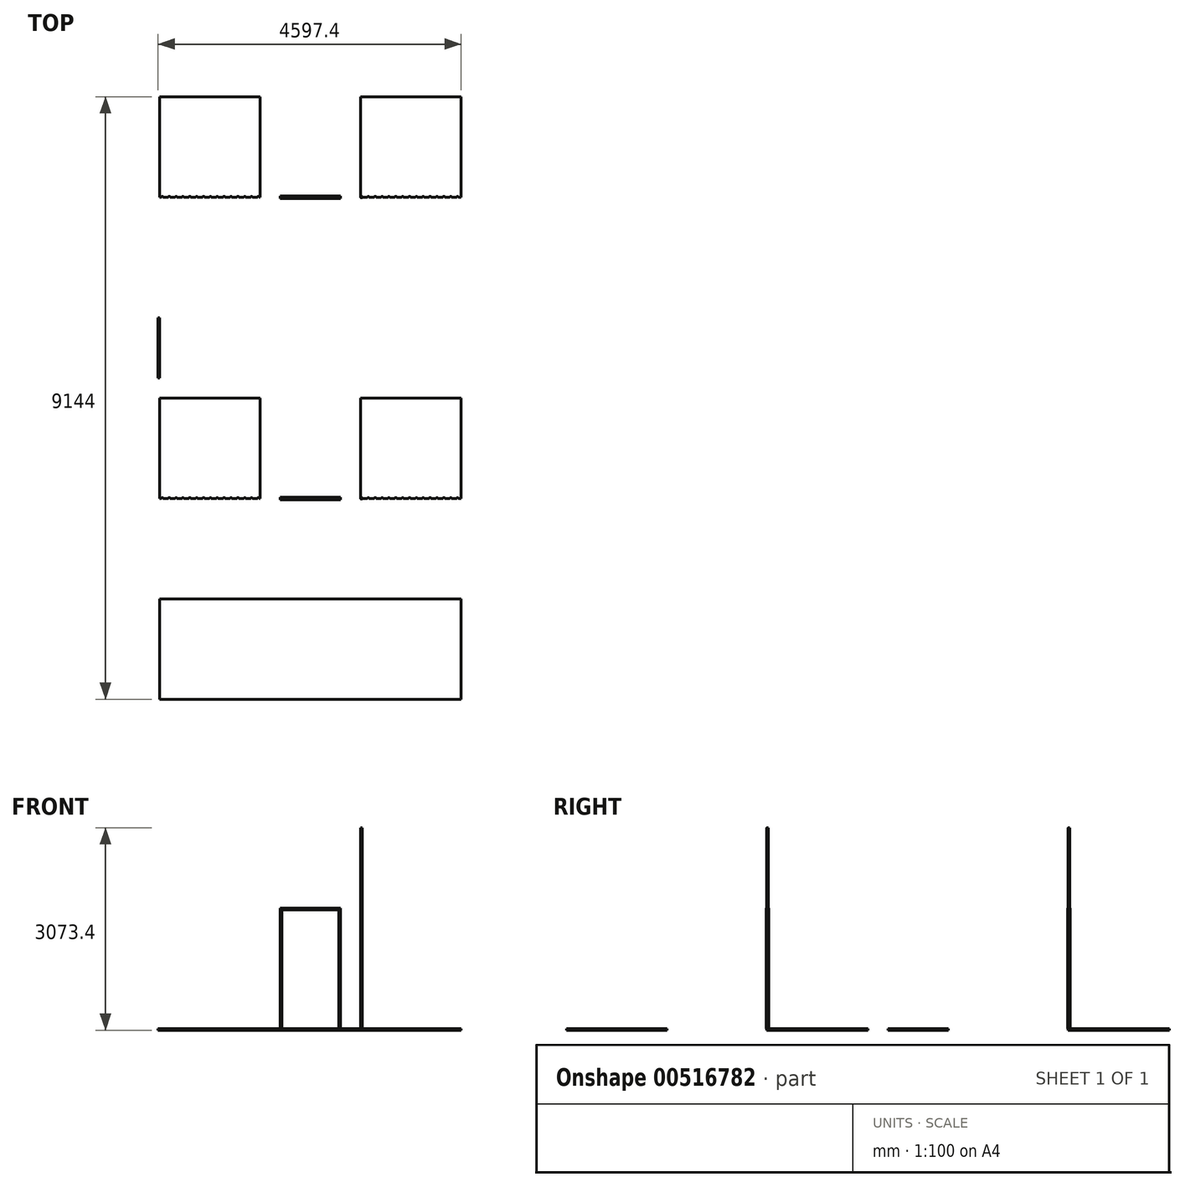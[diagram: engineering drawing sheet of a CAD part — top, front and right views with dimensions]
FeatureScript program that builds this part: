
annotation { "Feature Type Name" : "Feature", "Feature Type Description" : "" }
export const myFeature = defineFeature(function(context is Context, id is Id, definition is map)
    precondition{}
    {
        {
            var Q0;
            Q0=qCreatedBy(makeId("Top.planeOp"),FACE);
            var sketch = newSketch(context, id + "F0", { "sketchPlane" : qUnion([Q0])});
            skLineSegment(sketch, "E0.bottom", {"start": v(-766.53, 731.63) * mm, "end": v(757.47, 731.63) * mm});
            skLineSegment(sketch, "E0.top", {"start": v(-766.53, -792.37) * mm, "end": v(757.47, -792.37) * mm});
            skLineSegment(sketch, "E0.left", {"start": v(-766.53, 731.63) * mm, "end": v(-766.53, -792.37) * mm});
            skLineSegment(sketch, "E0.right", {"start": v(757.47, 731.63) * mm, "end": v(757.47, -792.37) * mm});
            skLineSegment(sketch, "E1.0.1.1", {"start": v(-766.53, 2255.63) * mm, "end": v(-766.53, 731.63) * mm});
            skLineSegment(sketch, "E1.0.1.2", {"start": v(757.47, 2255.63) * mm, "end": v(757.47, 731.63) * mm});
            skLineSegment(sketch, "E1.0.1.3", {"start": v(-766.53, 2255.63) * mm, "end": v(757.47, 2255.63) * mm});
            skLineSegment(sketch, "E1.0.2.0", {"start": v(-766.53, 2255.63) * mm, "end": v(757.47, 2255.63) * mm});
            skLineSegment(sketch, "E1.0.2.1", {"start": v(-766.53, 3779.63) * mm, "end": v(-766.53, 2255.63) * mm});
            skLineSegment(sketch, "E1.0.2.2", {"start": v(757.47, 3779.63) * mm, "end": v(757.47, 2255.63) * mm});
            skLineSegment(sketch, "E1.0.2.3", {"start": v(-766.53, 3779.63) * mm, "end": v(757.47, 3779.63) * mm});
            skLineSegment(sketch, "E1.0.3.0", {"start": v(-766.53, 3779.63) * mm, "end": v(757.47, 3779.63) * mm});
            skLineSegment(sketch, "E1.0.3.1", {"start": v(-766.53, 5303.63) * mm, "end": v(-766.53, 3779.63) * mm});
            skLineSegment(sketch, "E1.0.3.2", {"start": v(757.47, 5303.63) * mm, "end": v(757.47, 3779.63) * mm});
            skLineSegment(sketch, "E1.0.3.3", {"start": v(-766.53, 5303.63) * mm, "end": v(757.47, 5303.63) * mm});
            skLineSegment(sketch, "E1.0.4.0", {"start": v(-766.53, 5303.63) * mm, "end": v(757.47, 5303.63) * mm});
            skLineSegment(sketch, "E1.0.4.1", {"start": v(-766.53, 6827.63) * mm, "end": v(-766.53, 5303.63) * mm});
            skLineSegment(sketch, "E1.0.4.2", {"start": v(757.47, 6827.63) * mm, "end": v(757.47, 5303.63) * mm});
            skLineSegment(sketch, "E1.0.4.3", {"start": v(-766.53, 6827.63) * mm, "end": v(757.47, 6827.63) * mm});
            skLineSegment(sketch, "E1.0.5.0", {"start": v(-766.53, 6827.63) * mm, "end": v(757.47, 6827.63) * mm});
            skLineSegment(sketch, "E1.0.5.1", {"start": v(-766.53, 8351.63) * mm, "end": v(-766.53, 6827.63) * mm});
            skLineSegment(sketch, "E1.0.5.2", {"start": v(757.47, 8351.63) * mm, "end": v(757.47, 6827.63) * mm});
            skLineSegment(sketch, "E1.0.5.3", {"start": v(-766.53, 8351.63) * mm, "end": v(757.47, 8351.63) * mm});
            skLineSegment(sketch, "E1.0.6.0", {"start": v(-766.53, 8351.63) * mm, "end": v(757.47, 8351.63) * mm});
            skLineSegment(sketch, "E1.0.6.1", {"start": v(-766.53, 9875.63) * mm, "end": v(-766.53, 8351.63) * mm});
            skLineSegment(sketch, "E1.0.6.2", {"start": v(757.47, 9875.63) * mm, "end": v(757.47, 8351.63) * mm});
            skLineSegment(sketch, "E1.0.6.3", {"start": v(-766.53, 9875.63) * mm, "end": v(757.47, 9875.63) * mm});
            skLineSegment(sketch, "E1.1.0.0", {"start": v(757.47, -792.37) * mm, "end": v(2281.47, -792.37) * mm});
            skLineSegment(sketch, "E1.1.0.2", {"start": v(2281.47, 731.63) * mm, "end": v(2281.47, -792.37) * mm});
            skLineSegment(sketch, "E1.1.0.3", {"start": v(757.47, 731.63) * mm, "end": v(2281.47, 731.63) * mm});
            skLineSegment(sketch, "E1.1.1.0", {"start": v(757.47, 731.63) * mm, "end": v(2281.47, 731.63) * mm});
            skLineSegment(sketch, "E1.1.1.1", {"start": v(757.47, 2255.63) * mm, "end": v(757.47, 731.63) * mm});
            skLineSegment(sketch, "E1.1.1.2", {"start": v(2281.47, 2255.63) * mm, "end": v(2281.47, 731.63) * mm});
            skLineSegment(sketch, "E1.1.1.3", {"start": v(757.47, 2255.63) * mm, "end": v(2281.47, 2255.63) * mm});
            skLineSegment(sketch, "E1.1.2.0", {"start": v(757.47, 2255.63) * mm, "end": v(2281.47, 2255.63) * mm});
            skLineSegment(sketch, "E1.1.2.1", {"start": v(757.47, 3779.63) * mm, "end": v(757.47, 2255.63) * mm});
            skLineSegment(sketch, "E1.1.2.2", {"start": v(2281.47, 3779.63) * mm, "end": v(2281.47, 2255.63) * mm});
            skLineSegment(sketch, "E1.1.2.3", {"start": v(757.47, 3779.63) * mm, "end": v(2281.47, 3779.63) * mm});
            skLineSegment(sketch, "E1.1.3.0", {"start": v(757.47, 3779.63) * mm, "end": v(2281.47, 3779.63) * mm});
            skLineSegment(sketch, "E1.1.3.1", {"start": v(757.47, 5303.63) * mm, "end": v(757.47, 3779.63) * mm});
            skLineSegment(sketch, "E1.1.3.2", {"start": v(2281.47, 5303.63) * mm, "end": v(2281.47, 3779.63) * mm});
            skLineSegment(sketch, "E1.1.3.3", {"start": v(757.47, 5303.63) * mm, "end": v(2281.47, 5303.63) * mm});
            skLineSegment(sketch, "E1.1.4.0", {"start": v(757.47, 5303.63) * mm, "end": v(2281.47, 5303.63) * mm});
            skLineSegment(sketch, "E1.1.4.1", {"start": v(757.47, 6827.63) * mm, "end": v(757.47, 5303.63) * mm});
            skLineSegment(sketch, "E1.1.4.2", {"start": v(2281.47, 6827.63) * mm, "end": v(2281.47, 5303.63) * mm});
            skLineSegment(sketch, "E1.1.4.3", {"start": v(757.47, 6827.63) * mm, "end": v(2281.47, 6827.63) * mm});
            skLineSegment(sketch, "E1.1.5.0", {"start": v(757.47, 6827.63) * mm, "end": v(2281.47, 6827.63) * mm});
            skLineSegment(sketch, "E1.1.5.1", {"start": v(757.47, 8351.63) * mm, "end": v(757.47, 6827.63) * mm});
            skLineSegment(sketch, "E1.1.5.2", {"start": v(2281.47, 8351.63) * mm, "end": v(2281.47, 6827.63) * mm});
            skLineSegment(sketch, "E1.1.5.3", {"start": v(757.47, 8351.63) * mm, "end": v(2281.47, 8351.63) * mm});
            skLineSegment(sketch, "E1.1.6.0", {"start": v(757.47, 8351.63) * mm, "end": v(2281.47, 8351.63) * mm});
            skLineSegment(sketch, "E1.1.6.1", {"start": v(757.47, 9875.63) * mm, "end": v(757.47, 8351.63) * mm});
            skLineSegment(sketch, "E1.1.6.2", {"start": v(2281.47, 9875.63) * mm, "end": v(2281.47, 8351.63) * mm});
            skLineSegment(sketch, "E1.1.6.3", {"start": v(757.47, 9875.63) * mm, "end": v(2281.47, 9875.63) * mm});
            skLineSegment(sketch, "E1.2.0.0", {"start": v(2281.47, -792.37) * mm, "end": v(3805.47, -792.37) * mm});
            skLineSegment(sketch, "E1.2.0.1", {"start": v(2281.47, 731.63) * mm, "end": v(2281.47, -792.37) * mm});
            skLineSegment(sketch, "E1.2.0.2", {"start": v(3805.47, 731.63) * mm, "end": v(3805.47, -792.37) * mm});
            skLineSegment(sketch, "E1.2.0.3", {"start": v(2281.47, 731.63) * mm, "end": v(3805.47, 731.63) * mm});
            skLineSegment(sketch, "E1.2.1.0", {"start": v(2281.47, 731.63) * mm, "end": v(3805.47, 731.63) * mm});
            skLineSegment(sketch, "E1.2.1.1", {"start": v(2281.47, 2255.63) * mm, "end": v(2281.47, 731.63) * mm});
            skLineSegment(sketch, "E1.2.1.2", {"start": v(3805.47, 2255.63) * mm, "end": v(3805.47, 731.63) * mm});
            skLineSegment(sketch, "E1.2.1.3", {"start": v(2281.47, 2255.63) * mm, "end": v(3805.47, 2255.63) * mm});
            skLineSegment(sketch, "E1.2.2.0", {"start": v(2281.47, 2255.63) * mm, "end": v(3805.47, 2255.63) * mm});
            skLineSegment(sketch, "E1.2.2.1", {"start": v(2281.47, 3779.63) * mm, "end": v(2281.47, 2255.63) * mm});
            skLineSegment(sketch, "E1.2.2.2", {"start": v(3805.47, 3779.63) * mm, "end": v(3805.47, 2255.63) * mm});
            skLineSegment(sketch, "E1.2.2.3", {"start": v(2281.47, 3779.63) * mm, "end": v(3805.47, 3779.63) * mm});
            skLineSegment(sketch, "E1.2.3.0", {"start": v(2281.47, 3779.63) * mm, "end": v(3805.47, 3779.63) * mm});
            skLineSegment(sketch, "E1.2.3.1", {"start": v(2281.47, 5303.63) * mm, "end": v(2281.47, 3779.63) * mm});
            skLineSegment(sketch, "E1.2.3.2", {"start": v(3805.47, 5303.63) * mm, "end": v(3805.47, 3779.63) * mm});
            skLineSegment(sketch, "E1.2.3.3", {"start": v(2281.47, 5303.63) * mm, "end": v(3805.47, 5303.63) * mm});
            skLineSegment(sketch, "E1.2.4.0", {"start": v(2281.47, 5303.63) * mm, "end": v(3805.47, 5303.63) * mm});
            skLineSegment(sketch, "E1.2.4.1", {"start": v(2281.47, 6827.63) * mm, "end": v(2281.47, 5303.63) * mm});
            skLineSegment(sketch, "E1.2.4.2", {"start": v(3805.47, 6827.63) * mm, "end": v(3805.47, 5303.63) * mm});
            skLineSegment(sketch, "E1.2.4.3", {"start": v(2281.47, 6827.63) * mm, "end": v(3805.47, 6827.63) * mm});
            skLineSegment(sketch, "E1.2.5.0", {"start": v(2281.47, 6827.63) * mm, "end": v(3805.47, 6827.63) * mm});
            skLineSegment(sketch, "E1.2.5.1", {"start": v(2281.47, 8351.63) * mm, "end": v(2281.47, 6827.63) * mm});
            skLineSegment(sketch, "E1.2.5.2", {"start": v(3805.47, 8351.63) * mm, "end": v(3805.47, 6827.63) * mm});
            skLineSegment(sketch, "E1.2.5.3", {"start": v(2281.47, 8351.63) * mm, "end": v(3805.47, 8351.63) * mm});
            skLineSegment(sketch, "E1.2.6.0", {"start": v(2281.47, 8351.63) * mm, "end": v(3805.47, 8351.63) * mm});
            skLineSegment(sketch, "E1.2.6.1", {"start": v(2281.47, 9875.63) * mm, "end": v(2281.47, 8351.63) * mm});
            skLineSegment(sketch, "E1.2.6.2", {"start": v(3805.47, 9875.63) * mm, "end": v(3805.47, 8351.63) * mm});
            skLineSegment(sketch, "E1.2.6.3", {"start": v(2281.47, 9875.63) * mm, "end": v(3805.47, 9875.63) * mm});
            skLineSegment(sketch, "E1.direction1", {"start": v(-766.53, -792.37) * mm, "end": v(757.47, -792.37) * mm, "construction": true});
            skLineSegment(sketch, "E1.direction2", {"start": v(-766.53, -792.37) * mm, "end": v(-766.53, 731.63) * mm, "construction": true});
            skCircle(sketch, "E2", {"center": v(-728.43, 2255.63) * mm, "radius": 12.7 * mm});
            skCircle(sketch, "E3.0.1.0", {"center": v(-728.43, 6827.63) * mm, "radius": 12.7 * mm});
            skCircle(sketch, "E3.1.0.0", {"center": v(-624.29, 2255.63) * mm, "radius": 12.7 * mm});
            skCircle(sketch, "E3.1.1.0", {"center": v(-624.29, 6827.63) * mm, "radius": 12.7 * mm});
            skCircle(sketch, "E3.2.0.0", {"center": v(-520.15, 2255.63) * mm, "radius": 12.7 * mm});
            skCircle(sketch, "E3.2.1.0", {"center": v(-520.15, 6827.63) * mm, "radius": 12.7 * mm});
            skCircle(sketch, "E3.3.0.0", {"center": v(-416, 2255.63) * mm, "radius": 12.7 * mm});
            skCircle(sketch, "E3.3.1.0", {"center": v(-416, 6827.63) * mm, "radius": 12.7 * mm});
            skCircle(sketch, "E3.4.0.0", {"center": v(-311.87, 2255.63) * mm, "radius": 12.7 * mm});
            skCircle(sketch, "E3.4.1.0", {"center": v(-311.87, 6827.63) * mm, "radius": 12.7 * mm});
            skCircle(sketch, "E3.5.0.0", {"center": v(-207.73, 2255.63) * mm, "radius": 12.7 * mm});
            skCircle(sketch, "E3.5.1.0", {"center": v(-207.73, 6827.63) * mm, "radius": 12.7 * mm});
            skCircle(sketch, "E3.6.0.0", {"center": v(-103.59, 2255.63) * mm, "radius": 12.7 * mm});
            skCircle(sketch, "E3.6.1.0", {"center": v(-103.59, 6827.63) * mm, "radius": 12.7 * mm});
            skCircle(sketch, "E3.7.0.0", {"center": v(0.55, 2255.63) * mm, "radius": 12.7 * mm});
            skCircle(sketch, "E3.7.1.0", {"center": v(0.55, 6827.63) * mm, "radius": 12.7 * mm});
            skCircle(sketch, "E3.8.0.0", {"center": v(104.7, 2255.63) * mm, "radius": 12.7 * mm});
            skCircle(sketch, "E3.8.1.0", {"center": v(104.7, 6827.63) * mm, "radius": 12.7 * mm});
            skCircle(sketch, "E3.9.0.0", {"center": v(208.83, 2255.63) * mm, "radius": 12.7 * mm});
            skCircle(sketch, "E3.9.1.0", {"center": v(208.83, 6827.63) * mm, "radius": 12.7 * mm});
            skCircle(sketch, "E3.10.0.0", {"center": v(312.97, 2255.63) * mm, "radius": 12.7 * mm});
            skCircle(sketch, "E3.10.1.0", {"center": v(312.97, 6827.63) * mm, "radius": 12.7 * mm});
            skCircle(sketch, "E3.11.0.0", {"center": v(417.11, 2255.63) * mm, "radius": 12.7 * mm});
            skCircle(sketch, "E3.11.1.0", {"center": v(417.11, 6827.63) * mm, "radius": 12.7 * mm});
            skCircle(sketch, "E3.12.0.0", {"center": v(521.25, 2255.63) * mm, "radius": 12.7 * mm});
            skCircle(sketch, "E3.12.1.0", {"center": v(521.25, 6827.63) * mm, "radius": 12.7 * mm});
            skCircle(sketch, "E3.13.0.0", {"center": v(625.4, 2255.63) * mm, "radius": 12.7 * mm});
            skCircle(sketch, "E3.13.1.0", {"center": v(625.4, 6827.63) * mm, "radius": 12.7 * mm});
            skCircle(sketch, "E3.14.0.0", {"center": v(729.53, 2255.63) * mm, "radius": 12.7 * mm});
            skCircle(sketch, "E3.14.1.0", {"center": v(729.53, 6827.63) * mm, "radius": 12.7 * mm});
            skCircle(sketch, "E3.15.0.0", {"center": v(833.67, 2255.63) * mm, "radius": 12.7 * mm});
            skCircle(sketch, "E3.15.1.0", {"center": v(833.67, 6827.63) * mm, "radius": 12.7 * mm});
            skCircle(sketch, "E3.16.0.0", {"center": v(937.81, 2255.63) * mm, "radius": 12.7 * mm});
            skCircle(sketch, "E3.16.1.0", {"center": v(937.81, 6827.63) * mm, "radius": 12.7 * mm});
            skCircle(sketch, "E3.17.0.0", {"center": v(1041.95, 2255.63) * mm, "radius": 12.7 * mm});
            skCircle(sketch, "E3.17.1.0", {"center": v(1041.95, 6827.63) * mm, "radius": 12.7 * mm});
            skCircle(sketch, "E3.18.0.0", {"center": v(1146.1, 2255.63) * mm, "radius": 12.7 * mm});
            skCircle(sketch, "E3.18.1.0", {"center": v(1146.1, 6827.63) * mm, "radius": 12.7 * mm});
            skCircle(sketch, "E3.19.0.0", {"center": v(1250.23, 2255.63) * mm, "radius": 12.7 * mm});
            skCircle(sketch, "E3.19.1.0", {"center": v(1250.23, 6827.63) * mm, "radius": 12.7 * mm});
            skCircle(sketch, "E3.20.0.0", {"center": v(1354.37, 2255.63) * mm, "radius": 12.7 * mm});
            skCircle(sketch, "E3.20.1.0", {"center": v(1354.37, 6827.63) * mm, "radius": 12.7 * mm});
            skCircle(sketch, "E3.21.0.0", {"center": v(1458.51, 2255.63) * mm, "radius": 12.7 * mm});
            skCircle(sketch, "E3.21.1.0", {"center": v(1458.51, 6827.63) * mm, "radius": 12.7 * mm});
            skCircle(sketch, "E3.22.0.0", {"center": v(1562.65, 2255.63) * mm, "radius": 12.7 * mm});
            skCircle(sketch, "E3.22.1.0", {"center": v(1562.65, 6827.63) * mm, "radius": 12.7 * mm});
            skCircle(sketch, "E3.23.0.0", {"center": v(1666.8, 2255.63) * mm, "radius": 12.7 * mm});
            skCircle(sketch, "E3.23.1.0", {"center": v(1666.8, 6827.63) * mm, "radius": 12.7 * mm});
            skCircle(sketch, "E3.24.0.0", {"center": v(1770.93, 2255.63) * mm, "radius": 12.7 * mm});
            skCircle(sketch, "E3.24.1.0", {"center": v(1770.93, 6827.63) * mm, "radius": 12.7 * mm});
            skCircle(sketch, "E3.25.0.0", {"center": v(1875.07, 2255.63) * mm, "radius": 12.7 * mm});
            skCircle(sketch, "E3.25.1.0", {"center": v(1875.07, 6827.63) * mm, "radius": 12.7 * mm});
            skCircle(sketch, "E3.26.0.0", {"center": v(1979.21, 2255.63) * mm, "radius": 12.7 * mm});
            skCircle(sketch, "E3.26.1.0", {"center": v(1979.21, 6827.63) * mm, "radius": 12.7 * mm});
            skCircle(sketch, "E3.27.0.0", {"center": v(2083.35, 2255.63) * mm, "radius": 12.7 * mm});
            skCircle(sketch, "E3.27.1.0", {"center": v(2083.35, 6827.63) * mm, "radius": 12.7 * mm});
            skCircle(sketch, "E3.28.0.0", {"center": v(2187.5, 2255.63) * mm, "radius": 12.7 * mm});
            skCircle(sketch, "E3.28.1.0", {"center": v(2187.5, 6827.63) * mm, "radius": 12.7 * mm});
            skCircle(sketch, "E3.29.0.0", {"center": v(2291.63, 2255.63) * mm, "radius": 12.7 * mm});
            skCircle(sketch, "E3.29.1.0", {"center": v(2291.63, 6827.63) * mm, "radius": 12.7 * mm});
            skCircle(sketch, "E3.30.0.0", {"center": v(2395.77, 2255.63) * mm, "radius": 12.7 * mm});
            skCircle(sketch, "E3.30.1.0", {"center": v(2395.77, 6827.63) * mm, "radius": 12.7 * mm});
            skCircle(sketch, "E3.31.0.0", {"center": v(2499.91, 2255.63) * mm, "radius": 12.7 * mm});
            skCircle(sketch, "E3.31.1.0", {"center": v(2499.91, 6827.63) * mm, "radius": 12.7 * mm});
            skCircle(sketch, "E3.32.0.0", {"center": v(2604.05, 2255.63) * mm, "radius": 12.7 * mm});
            skCircle(sketch, "E3.32.1.0", {"center": v(2604.05, 6827.63) * mm, "radius": 12.7 * mm});
            skCircle(sketch, "E3.33.0.0", {"center": v(2708.2, 2255.63) * mm, "radius": 12.7 * mm});
            skCircle(sketch, "E3.33.1.0", {"center": v(2708.2, 6827.63) * mm, "radius": 12.7 * mm});
            skCircle(sketch, "E3.34.0.0", {"center": v(2812.33, 2255.63) * mm, "radius": 12.7 * mm});
            skCircle(sketch, "E3.34.1.0", {"center": v(2812.33, 6827.63) * mm, "radius": 12.7 * mm});
            skCircle(sketch, "E3.35.0.0", {"center": v(2916.47, 2255.63) * mm, "radius": 12.7 * mm});
            skCircle(sketch, "E3.35.1.0", {"center": v(2916.47, 6827.63) * mm, "radius": 12.7 * mm});
            skCircle(sketch, "E3.36.0.0", {"center": v(3020.61, 2255.63) * mm, "radius": 12.7 * mm});
            skCircle(sketch, "E3.36.1.0", {"center": v(3020.61, 6827.63) * mm, "radius": 12.7 * mm});
            skCircle(sketch, "E3.37.0.0", {"center": v(3124.75, 2255.63) * mm, "radius": 12.7 * mm});
            skCircle(sketch, "E3.37.1.0", {"center": v(3124.75, 6827.63) * mm, "radius": 12.7 * mm});
            skCircle(sketch, "E3.38.0.0", {"center": v(3228.9, 2255.63) * mm, "radius": 12.7 * mm});
            skCircle(sketch, "E3.38.1.0", {"center": v(3228.9, 6827.63) * mm, "radius": 12.7 * mm});
            skCircle(sketch, "E3.39.0.0", {"center": v(3333.03, 2255.63) * mm, "radius": 12.7 * mm});
            skCircle(sketch, "E3.39.1.0", {"center": v(3333.03, 6827.63) * mm, "radius": 12.7 * mm});
            skCircle(sketch, "E3.40.0.0", {"center": v(3437.17, 2255.63) * mm, "radius": 12.7 * mm});
            skCircle(sketch, "E3.40.1.0", {"center": v(3437.17, 6827.63) * mm, "radius": 12.7 * mm});
            skCircle(sketch, "E3.41.0.0", {"center": v(3541.31, 2255.63) * mm, "radius": 12.7 * mm});
            skCircle(sketch, "E3.41.1.0", {"center": v(3541.31, 6827.63) * mm, "radius": 12.7 * mm});
            skCircle(sketch, "E3.42.0.0", {"center": v(3645.45, 2255.63) * mm, "radius": 12.7 * mm});
            skCircle(sketch, "E3.42.1.0", {"center": v(3645.45, 6827.63) * mm, "radius": 12.7 * mm});
            skCircle(sketch, "E3.43.0.0", {"center": v(3749.6, 2255.63) * mm, "radius": 12.7 * mm});
            skCircle(sketch, "E3.43.1.0", {"center": v(3749.6, 6827.63) * mm, "radius": 12.7 * mm});
            skLineSegment(sketch, "E3.direction1", {"start": v(-728.43, 2255.63) * mm, "end": v(-624.29, 2255.63) * mm, "construction": true});
            skLineSegment(sketch, "E3.direction2", {"start": v(-728.43, 2255.63) * mm, "end": v(-728.43, 6827.63) * mm, "construction": true});
            skSolve(sketch);
        }
        {
            var Q0;
            {var subQ38=sQuery(id+"F0.wireOp",EDGE,"E1.1.4.0");Q0=makeQuery(id+"F0.imprint","IMPRINT",FACE,{"disambiguationData":[TD([[makeQuery(id+"F0.imprint","IMPRINT",EDGE,{"derivedFrom":subQ38}),1.0]])]});}
            var Q1;
            {var subQ8=sQuery(id+"F0.wireOp",EDGE,"E1.1.5.1");Q1=makeQuery(id+"F0.imprint","IMPRINT",FACE,{"disambiguationData":[TD([[makeQuery(id+"F0.imprint","IMPRINT",EDGE,{"derivedFrom":subQ8}),1.0]])]});}
            var Q2;
            {var subQ11=sQuery(id+"F0.wireOp",EDGE,"E1.2.5.2");Q2=makeQuery(id+"F0.imprint","IMPRINT",FACE,{"disambiguationData":[TD([[makeQuery(id+"F0.imprint","IMPRINT",EDGE,{"derivedFrom":subQ11}),-1.0]])]});}
            var Q3;
            Q3=makeQuery(id+"F0.imprint","IMPRINT",FACE,{"disambiguationData":[TD([[makeQuery(id+"F0.imprint","IMPRINT",EDGE,{"derivedFrom":sQuery(id+"F0.wireOp",EDGE,"E1.2.3.0")}),1.0]])]});
            var Q4;
            {var subQ18=sQuery(id+"F0.wireOp",EDGE,"E1.1.1.0");Q4=makeQuery(id+"F0.imprint","IMPRINT",FACE,{"disambiguationData":[TD([[makeQuery(id+"F0.imprint","IMPRINT",EDGE,{"derivedFrom":subQ18}),1.0]])]});}
            var Q5;
            {var subQ35=sQuery(id+"F0.wireOp",EDGE,"E1.2.4.0");Q5=makeQuery(id+"F0.imprint","IMPRINT",FACE,{"disambiguationData":[TD([[makeQuery(id+"F0.imprint","IMPRINT",EDGE,{"derivedFrom":subQ35}),1.0]])]});}
            var Q6;
            Q6=makeQuery(id+"F0.imprint","IMPRINT",FACE,{"disambiguationData":[TD([[makeQuery(id+"F0.imprint","IMPRINT",EDGE,{"derivedFrom":sQuery(id+"F0.wireOp",EDGE,"E0.top")}),1.0]])]});
            var Q7;
            Q7=makeQuery(id+"F0.imprint","IMPRINT",FACE,{"disambiguationData":[TD([[makeQuery(id+"F0.imprint","IMPRINT",EDGE,{"derivedFrom":sQuery(id+"F0.wireOp",EDGE,"E1.0.6.0")}),1.0]])]});
            var Q8;
            Q8=makeQuery(id+"F0.imprint","IMPRINT",FACE,{"disambiguationData":[TD([[makeQuery(id+"F0.imprint","IMPRINT",EDGE,{"derivedFrom":sQuery(id+"F0.wireOp",EDGE,"E1.2.0.0")}),1.0]])]});
            var Q9;
            Q9=makeQuery(id+"F0.imprint","IMPRINT",FACE,{"disambiguationData":[TD([[makeQuery(id+"F0.imprint","IMPRINT",EDGE,{"derivedFrom":sQuery(id+"F0.wireOp",EDGE,"E1.2.6.0")}),1.0]])]});
            var Q10;
            Q10=makeQuery(id+"F0.imprint","IMPRINT",FACE,{"disambiguationData":[TD([[makeQuery(id+"F0.imprint","IMPRINT",EDGE,{"derivedFrom":sQuery(id+"F0.wireOp",EDGE,"E0.bottom")}),1.0]])]});
            var Q11;
            {var subQ30=sQuery(id+"F0.wireOp",EDGE,"E1.0.2.1");Q11=makeQuery(id+"F0.imprint","IMPRINT",FACE,{"disambiguationData":[TD([[makeQuery(id+"F0.imprint","IMPRINT",EDGE,{"derivedFrom":subQ30}),1.0]])]});}
            var Q12;
            Q12=makeQuery(id+"F0.imprint","IMPRINT",FACE,{"disambiguationData":[TD([[makeQuery(id+"F0.imprint","IMPRINT",EDGE,{"derivedFrom":sQuery(id+"F0.wireOp",EDGE,"E1.0.3.0")}),1.0]])]});
            var Q13;
            Q13=makeQuery(id+"F0.imprint","IMPRINT",FACE,{"disambiguationData":[TD([[makeQuery(id+"F0.imprint","IMPRINT",EDGE,{"derivedFrom":sQuery(id+"F0.wireOp",EDGE,"E1.0.4.0")}),1.0]])]});
            var Q14;
            {var subQ39=sQuery(id+"F0.wireOp",EDGE,"E1.0.5.1");Q14=makeQuery(id+"F0.imprint","IMPRINT",FACE,{"disambiguationData":[TD([[makeQuery(id+"F0.imprint","IMPRINT",EDGE,{"derivedFrom":subQ39}),1.0]])]});}
            var Q15;
            Q15=makeQuery(id+"F0.imprint","IMPRINT",FACE,{"disambiguationData":[TD([[makeQuery(id+"F0.imprint","IMPRINT",EDGE,{"derivedFrom":sQuery(id+"F0.wireOp",EDGE,"E1.1.0.0")}),1.0]])]});
            var Q16;
            Q16=makeQuery(id+"F0.imprint","IMPRINT",FACE,{"disambiguationData":[TD([[makeQuery(id+"F0.imprint","IMPRINT",EDGE,{"derivedFrom":sQuery(id+"F0.wireOp",EDGE,"E1.1.6.0")}),1.0]])]});
            var Q17;
            {var subQ34=sQuery(id+"F0.wireOp",EDGE,"E1.2.1.0");Q17=makeQuery(id+"F0.imprint","IMPRINT",FACE,{"disambiguationData":[TD([[makeQuery(id+"F0.imprint","IMPRINT",EDGE,{"derivedFrom":subQ34}),1.0]])]});}
            var Q18;
            {var subQ5=sQuery(id+"F0.wireOp",EDGE,"E1.2.2.2");Q18=makeQuery(id+"F0.imprint","IMPRINT",FACE,{"disambiguationData":[TD([[makeQuery(id+"F0.imprint","IMPRINT",EDGE,{"derivedFrom":subQ5}),-1.0]])]});}
            var Q19;
            {var subQ0=sQuery(id+"F0.wireOp",EDGE,"E1.1.2.1");Q19=makeQuery(id+"F0.imprint","IMPRINT",FACE,{"disambiguationData":[TD([[makeQuery(id+"F0.imprint","IMPRINT",EDGE,{"derivedFrom":subQ0}),1.0]])]});}
            var Q20;
            Q20=makeQuery(id+"F0.imprint","IMPRINT",FACE,{"disambiguationData":[TD([[makeQuery(id+"F0.imprint","IMPRINT",EDGE,{"derivedFrom":sQuery(id+"F0.wireOp",EDGE,"E1.1.3.0")}),1.0]])]});
            var Q21;
            {var subQ0=sQuery(id+"F0.wireOp",EDGE,"E3.39.0.0");var subQ1=sQuery(id+"F0.wireOp",EDGE,"E1.2.2.0");var subQ2=makeQuery(id+"F0.imprint","INTERSECT",VERTEX,{"disambiguationData":[OD(0.0)],"derivedFrom":[subQ1,subQ0]});Q21=makeQuery(id+"F0.imprint","IMPRINT",FACE,{"disambiguationData":[TD([[makeQuery(id+"F0.imprint","IMPRINT",EDGE,{"disambiguationData":[TD([[subQ2,-1.0]])],"derivedFrom":subQ1}),-1.0]])]});}
            var Q22;
            {var subQ0=sQuery(id+"F0.wireOp",EDGE,"E3.33.1.0");var subQ1=sQuery(id+"F0.wireOp",EDGE,"E1.2.5.0");var subQ2=makeQuery(id+"F0.imprint","INTERSECT",VERTEX,{"disambiguationData":[OD(0.0)],"derivedFrom":[subQ1,subQ0]});Q22=makeQuery(id+"F0.imprint","IMPRINT",FACE,{"disambiguationData":[TD([[makeQuery(id+"F0.imprint","IMPRINT",EDGE,{"disambiguationData":[TD([[subQ2,-1.0]])],"derivedFrom":subQ1}),-1.0]])]});}
            var Q23;
            {var subQ0=sQuery(id+"F0.wireOp",EDGE,"E3.41.1.0");var subQ1=sQuery(id+"F0.wireOp",EDGE,"E1.2.5.0");var subQ2=makeQuery(id+"F0.imprint","INTERSECT",VERTEX,{"disambiguationData":[OD(0.0)],"derivedFrom":[subQ1,subQ0]});Q23=makeQuery(id+"F0.imprint","IMPRINT",FACE,{"disambiguationData":[TD([[makeQuery(id+"F0.imprint","IMPRINT",EDGE,{"disambiguationData":[TD([[subQ2,-1.0]])],"derivedFrom":subQ1}),-1.0]])]});}
            var Q24;
            {var subQ0=sQuery(id+"F0.wireOp",EDGE,"E3.35.0.0");var subQ1=sQuery(id+"F0.wireOp",EDGE,"E1.2.2.0");var subQ2=makeQuery(id+"F0.imprint","INTERSECT",VERTEX,{"disambiguationData":[OD(0.0)],"derivedFrom":[subQ1,subQ0]});Q24=makeQuery(id+"F0.imprint","IMPRINT",FACE,{"disambiguationData":[TD([[makeQuery(id+"F0.imprint","IMPRINT",EDGE,{"disambiguationData":[TD([[subQ2,-1.0]])],"derivedFrom":subQ1}),1.0]])]});}
            var Q25;
            {var subQ0=sQuery(id+"F0.wireOp",EDGE,"E3.32.0.0");var subQ1=sQuery(id+"F0.wireOp",EDGE,"E1.2.2.0");var subQ2=makeQuery(id+"F0.imprint","INTERSECT",VERTEX,{"disambiguationData":[OD(0.0)],"derivedFrom":[subQ1,subQ0]});Q25=makeQuery(id+"F0.imprint","IMPRINT",FACE,{"disambiguationData":[TD([[makeQuery(id+"F0.imprint","IMPRINT",EDGE,{"disambiguationData":[TD([[subQ2,-1.0]])],"derivedFrom":subQ1}),1.0]])]});}
            var Q26;
            {var subQ0=sQuery(id+"F0.wireOp",EDGE,"E3.37.1.0");var subQ1=sQuery(id+"F0.wireOp",EDGE,"E1.2.5.0");var subQ2=makeQuery(id+"F0.imprint","INTERSECT",VERTEX,{"disambiguationData":[OD(0.0)],"derivedFrom":[subQ1,subQ0]});Q26=makeQuery(id+"F0.imprint","IMPRINT",FACE,{"disambiguationData":[TD([[makeQuery(id+"F0.imprint","IMPRINT",EDGE,{"disambiguationData":[TD([[subQ2,-1.0]])],"derivedFrom":subQ1}),1.0]])]});}
            var Q27;
            {var subQ0=sQuery(id+"F0.wireOp",EDGE,"E3.38.1.0");var subQ1=sQuery(id+"F0.wireOp",EDGE,"E1.2.5.0");var subQ2=makeQuery(id+"F0.imprint","INTERSECT",VERTEX,{"disambiguationData":[OD(0.0)],"derivedFrom":[subQ1,subQ0]});Q27=makeQuery(id+"F0.imprint","IMPRINT",FACE,{"disambiguationData":[TD([[makeQuery(id+"F0.imprint","IMPRINT",EDGE,{"disambiguationData":[TD([[subQ2,-1.0]])],"derivedFrom":subQ1}),1.0]])]});}
            var Q28;
            {var subQ0=sQuery(id+"F0.wireOp",EDGE,"E3.35.1.0");var subQ1=sQuery(id+"F0.wireOp",EDGE,"E1.2.5.0");var subQ2=makeQuery(id+"F0.imprint","INTERSECT",VERTEX,{"disambiguationData":[OD(0.0)],"derivedFrom":[subQ1,subQ0]});Q28=makeQuery(id+"F0.imprint","IMPRINT",FACE,{"disambiguationData":[TD([[makeQuery(id+"F0.imprint","IMPRINT",EDGE,{"disambiguationData":[TD([[subQ2,-1.0]])],"derivedFrom":subQ1}),1.0]])]});}
            var Q29;
            {var subQ0=sQuery(id+"F0.wireOp",EDGE,"E3.34.0.0");var subQ1=sQuery(id+"F0.wireOp",EDGE,"E1.2.2.0");var subQ2=makeQuery(id+"F0.imprint","INTERSECT",VERTEX,{"disambiguationData":[OD(0.0)],"derivedFrom":[subQ1,subQ0]});Q29=makeQuery(id+"F0.imprint","IMPRINT",FACE,{"disambiguationData":[TD([[makeQuery(id+"F0.imprint","IMPRINT",EDGE,{"disambiguationData":[TD([[subQ2,-1.0]])],"derivedFrom":subQ1}),-1.0]])]});}
            var Q30;
            {var subQ0=sQuery(id+"F0.wireOp",EDGE,"E3.33.0.0");var subQ1=sQuery(id+"F0.wireOp",EDGE,"E1.2.2.0");var subQ2=makeQuery(id+"F0.imprint","INTERSECT",VERTEX,{"disambiguationData":[OD(0.0)],"derivedFrom":[subQ1,subQ0]});Q30=makeQuery(id+"F0.imprint","IMPRINT",FACE,{"disambiguationData":[TD([[makeQuery(id+"F0.imprint","IMPRINT",EDGE,{"disambiguationData":[TD([[subQ2,-1.0]])],"derivedFrom":subQ1}),1.0]])]});}
            var Q31;
            {var subQ0=sQuery(id+"F0.wireOp",EDGE,"E3.41.0.0");var subQ1=sQuery(id+"F0.wireOp",EDGE,"E1.2.2.0");var subQ2=makeQuery(id+"F0.imprint","INTERSECT",VERTEX,{"disambiguationData":[OD(0.0)],"derivedFrom":[subQ1,subQ0]});Q31=makeQuery(id+"F0.imprint","IMPRINT",FACE,{"disambiguationData":[TD([[makeQuery(id+"F0.imprint","IMPRINT",EDGE,{"disambiguationData":[TD([[subQ2,-1.0]])],"derivedFrom":subQ1}),1.0]])]});}
            var Q32;
            {var subQ0=sQuery(id+"F0.wireOp",EDGE,"E3.37.0.0");var subQ1=sQuery(id+"F0.wireOp",EDGE,"E1.2.2.0");var subQ2=makeQuery(id+"F0.imprint","INTERSECT",VERTEX,{"disambiguationData":[OD(0.0)],"derivedFrom":[subQ1,subQ0]});Q32=makeQuery(id+"F0.imprint","IMPRINT",FACE,{"disambiguationData":[TD([[makeQuery(id+"F0.imprint","IMPRINT",EDGE,{"disambiguationData":[TD([[subQ2,-1.0]])],"derivedFrom":subQ1}),1.0]])]});}
            var Q33;
            {var subQ0=sQuery(id+"F0.wireOp",EDGE,"E3.39.1.0");var subQ1=sQuery(id+"F0.wireOp",EDGE,"E1.2.5.0");var subQ2=makeQuery(id+"F0.imprint","INTERSECT",VERTEX,{"disambiguationData":[OD(0.0)],"derivedFrom":[subQ1,subQ0]});Q33=makeQuery(id+"F0.imprint","IMPRINT",FACE,{"disambiguationData":[TD([[makeQuery(id+"F0.imprint","IMPRINT",EDGE,{"disambiguationData":[TD([[subQ2,-1.0]])],"derivedFrom":subQ1}),1.0]])]});}
            var Q34;
            {var subQ0=sQuery(id+"F0.wireOp",EDGE,"E3.38.0.0");var subQ1=sQuery(id+"F0.wireOp",EDGE,"E1.2.2.0");var subQ2=makeQuery(id+"F0.imprint","INTERSECT",VERTEX,{"disambiguationData":[OD(0.0)],"derivedFrom":[subQ1,subQ0]});Q34=makeQuery(id+"F0.imprint","IMPRINT",FACE,{"disambiguationData":[TD([[makeQuery(id+"F0.imprint","IMPRINT",EDGE,{"disambiguationData":[TD([[subQ2,-1.0]])],"derivedFrom":subQ1}),1.0]])]});}
            var Q35;
            {var subQ0=sQuery(id+"F0.wireOp",EDGE,"E3.32.1.0");var subQ1=sQuery(id+"F0.wireOp",EDGE,"E1.2.5.0");var subQ2=makeQuery(id+"F0.imprint","INTERSECT",VERTEX,{"disambiguationData":[OD(0.0)],"derivedFrom":[subQ1,subQ0]});Q35=makeQuery(id+"F0.imprint","IMPRINT",FACE,{"disambiguationData":[TD([[makeQuery(id+"F0.imprint","IMPRINT",EDGE,{"disambiguationData":[TD([[subQ2,-1.0]])],"derivedFrom":subQ1}),-1.0]])]});}
            var Q36;
            {var subQ0=sQuery(id+"F0.wireOp",EDGE,"E3.20.1.0");var subQ1=sQuery(id+"F0.wireOp",EDGE,"E1.1.5.0");var subQ2=makeQuery(id+"F0.imprint","INTERSECT",VERTEX,{"disambiguationData":[OD(0.0)],"derivedFrom":[subQ1,subQ0]});Q36=makeQuery(id+"F0.imprint","IMPRINT",FACE,{"disambiguationData":[TD([[makeQuery(id+"F0.imprint","IMPRINT",EDGE,{"disambiguationData":[TD([[subQ2,-1.0]])],"derivedFrom":subQ1}),1.0]])]});}
            var Q37;
            {var subQ0=sQuery(id+"F0.wireOp",EDGE,"E3.26.1.0");var subQ1=sQuery(id+"F0.wireOp",EDGE,"E1.1.5.0");var subQ2=makeQuery(id+"F0.imprint","INTERSECT",VERTEX,{"disambiguationData":[OD(0.0)],"derivedFrom":[subQ1,subQ0]});Q37=makeQuery(id+"F0.imprint","IMPRINT",FACE,{"disambiguationData":[TD([[makeQuery(id+"F0.imprint","IMPRINT",EDGE,{"disambiguationData":[TD([[subQ2,-1.0]])],"derivedFrom":subQ1}),1.0]])]});}
            var Q38;
            {var subQ0=sQuery(id+"F0.wireOp",EDGE,"E3.42.1.0");var subQ1=sQuery(id+"F0.wireOp",EDGE,"E1.2.5.0");var subQ2=makeQuery(id+"F0.imprint","INTERSECT",VERTEX,{"disambiguationData":[OD(0.0)],"derivedFrom":[subQ1,subQ0]});Q38=makeQuery(id+"F0.imprint","IMPRINT",FACE,{"disambiguationData":[TD([[makeQuery(id+"F0.imprint","IMPRINT",EDGE,{"disambiguationData":[TD([[subQ2,-1.0]])],"derivedFrom":subQ1}),1.0]])]});}
            var Q39;
            {var subQ0=sQuery(id+"F0.wireOp",EDGE,"E3.26.0.0");var subQ1=sQuery(id+"F0.wireOp",EDGE,"E1.1.2.0");var subQ2=makeQuery(id+"F0.imprint","INTERSECT",VERTEX,{"disambiguationData":[OD(0.0)],"derivedFrom":[subQ1,subQ0]});Q39=makeQuery(id+"F0.imprint","IMPRINT",FACE,{"disambiguationData":[TD([[makeQuery(id+"F0.imprint","IMPRINT",EDGE,{"disambiguationData":[TD([[subQ2,-1.0]])],"derivedFrom":subQ1}),1.0]])]});}
            var Q40;
            {var subQ0=sQuery(id+"F0.wireOp",EDGE,"E3.32.0.0");var subQ1=sQuery(id+"F0.wireOp",EDGE,"E1.2.2.0");var subQ2=makeQuery(id+"F0.imprint","INTERSECT",VERTEX,{"disambiguationData":[OD(0.0)],"derivedFrom":[subQ1,subQ0]});Q40=makeQuery(id+"F0.imprint","IMPRINT",FACE,{"disambiguationData":[TD([[makeQuery(id+"F0.imprint","IMPRINT",EDGE,{"disambiguationData":[TD([[subQ2,-1.0]])],"derivedFrom":subQ1}),-1.0]])]});}
            var Q41;
            {var subQ0=sQuery(id+"F0.wireOp",EDGE,"E3.37.1.0");var subQ1=sQuery(id+"F0.wireOp",EDGE,"E1.2.5.0");var subQ2=makeQuery(id+"F0.imprint","INTERSECT",VERTEX,{"disambiguationData":[OD(0.0)],"derivedFrom":[subQ1,subQ0]});Q41=makeQuery(id+"F0.imprint","IMPRINT",FACE,{"disambiguationData":[TD([[makeQuery(id+"F0.imprint","IMPRINT",EDGE,{"disambiguationData":[TD([[subQ2,-1.0]])],"derivedFrom":subQ1}),-1.0]])]});}
            var Q42;
            {var subQ0=sQuery(id+"F0.wireOp",EDGE,"E3.35.1.0");var subQ1=sQuery(id+"F0.wireOp",EDGE,"E1.2.5.0");var subQ2=makeQuery(id+"F0.imprint","INTERSECT",VERTEX,{"disambiguationData":[OD(0.0)],"derivedFrom":[subQ1,subQ0]});Q42=makeQuery(id+"F0.imprint","IMPRINT",FACE,{"disambiguationData":[TD([[makeQuery(id+"F0.imprint","IMPRINT",EDGE,{"disambiguationData":[TD([[subQ2,-1.0]])],"derivedFrom":subQ1}),-1.0]])]});}
            var Q43;
            {var subQ0=sQuery(id+"F0.wireOp",EDGE,"E3.33.0.0");var subQ1=sQuery(id+"F0.wireOp",EDGE,"E1.2.2.0");var subQ2=makeQuery(id+"F0.imprint","INTERSECT",VERTEX,{"disambiguationData":[OD(0.0)],"derivedFrom":[subQ1,subQ0]});Q43=makeQuery(id+"F0.imprint","IMPRINT",FACE,{"disambiguationData":[TD([[makeQuery(id+"F0.imprint","IMPRINT",EDGE,{"disambiguationData":[TD([[subQ2,-1.0]])],"derivedFrom":subQ1}),-1.0]])]});}
            var Q44;
            {var subQ0=sQuery(id+"F0.wireOp",EDGE,"E3.35.0.0");var subQ1=sQuery(id+"F0.wireOp",EDGE,"E1.2.2.0");var subQ2=makeQuery(id+"F0.imprint","INTERSECT",VERTEX,{"disambiguationData":[OD(0.0)],"derivedFrom":[subQ1,subQ0]});Q44=makeQuery(id+"F0.imprint","IMPRINT",FACE,{"disambiguationData":[TD([[makeQuery(id+"F0.imprint","IMPRINT",EDGE,{"disambiguationData":[TD([[subQ2,-1.0]])],"derivedFrom":subQ1}),-1.0]])]});}
            var Q45;
            {var subQ0=sQuery(id+"F0.wireOp",EDGE,"E3.21.0.0");var subQ1=sQuery(id+"F0.wireOp",EDGE,"E1.1.2.0");var subQ2=makeQuery(id+"F0.imprint","INTERSECT",VERTEX,{"disambiguationData":[OD(0.0)],"derivedFrom":[subQ1,subQ0]});Q45=makeQuery(id+"F0.imprint","IMPRINT",FACE,{"disambiguationData":[TD([[makeQuery(id+"F0.imprint","IMPRINT",EDGE,{"disambiguationData":[TD([[subQ2,-1.0]])],"derivedFrom":subQ1}),1.0]])]});}
            var Q46;
            {var subQ0=sQuery(id+"F0.wireOp",EDGE,"E3.23.1.0");var subQ1=sQuery(id+"F0.wireOp",EDGE,"E1.1.5.0");var subQ2=makeQuery(id+"F0.imprint","INTERSECT",VERTEX,{"disambiguationData":[OD(0.0)],"derivedFrom":[subQ1,subQ0]});Q46=makeQuery(id+"F0.imprint","IMPRINT",FACE,{"disambiguationData":[TD([[makeQuery(id+"F0.imprint","IMPRINT",EDGE,{"disambiguationData":[TD([[subQ2,-1.0]])],"derivedFrom":subQ1}),1.0]])]});}
            var Q47;
            {var subQ0=sQuery(id+"F0.wireOp",EDGE,"E3.12.0.0");var subQ1=sQuery(id+"F0.wireOp",EDGE,"E1.0.2.0");var subQ2=makeQuery(id+"F0.imprint","INTERSECT",VERTEX,{"disambiguationData":[OD(0.0)],"derivedFrom":[subQ1,subQ0]});Q47=makeQuery(id+"F0.imprint","IMPRINT",FACE,{"disambiguationData":[TD([[makeQuery(id+"F0.imprint","IMPRINT",EDGE,{"disambiguationData":[TD([[subQ2,-1.0]])],"derivedFrom":subQ1}),-1.0]])]});}
            var Q48;
            {var subQ0=sQuery(id+"F0.wireOp",EDGE,"E3.22.0.0");var subQ1=sQuery(id+"F0.wireOp",EDGE,"E1.1.2.0");var subQ2=makeQuery(id+"F0.imprint","INTERSECT",VERTEX,{"disambiguationData":[OD(0.0)],"derivedFrom":[subQ1,subQ0]});Q48=makeQuery(id+"F0.imprint","IMPRINT",FACE,{"disambiguationData":[TD([[makeQuery(id+"F0.imprint","IMPRINT",EDGE,{"disambiguationData":[TD([[subQ2,-1.0]])],"derivedFrom":subQ1}),1.0]])]});}
            var Q49;
            {var subQ0=sQuery(id+"F0.wireOp",EDGE,"E3.7.1.0");var subQ1=sQuery(id+"F0.wireOp",EDGE,"E1.0.5.0");var subQ2=makeQuery(id+"F0.imprint","INTERSECT",VERTEX,{"disambiguationData":[OD(0.0)],"derivedFrom":[subQ1,subQ0]});Q49=makeQuery(id+"F0.imprint","IMPRINT",FACE,{"disambiguationData":[TD([[makeQuery(id+"F0.imprint","IMPRINT",EDGE,{"disambiguationData":[TD([[subQ2,-1.0]])],"derivedFrom":subQ1}),1.0]])]});}
            var Q50;
            {var subQ0=sQuery(id+"F0.wireOp",EDGE,"E3.18.0.0");var subQ1=sQuery(id+"F0.wireOp",EDGE,"E1.1.2.0");var subQ2=makeQuery(id+"F0.imprint","INTERSECT",VERTEX,{"disambiguationData":[OD(0.0)],"derivedFrom":[subQ1,subQ0]});Q50=makeQuery(id+"F0.imprint","IMPRINT",FACE,{"disambiguationData":[TD([[makeQuery(id+"F0.imprint","IMPRINT",EDGE,{"disambiguationData":[TD([[subQ2,-1.0]])],"derivedFrom":subQ1}),1.0]])]});}
            var Q51;
            {var subQ0=sQuery(id+"F0.wireOp",EDGE,"E3.38.1.0");var subQ1=sQuery(id+"F0.wireOp",EDGE,"E1.2.5.0");var subQ2=makeQuery(id+"F0.imprint","INTERSECT",VERTEX,{"disambiguationData":[OD(0.0)],"derivedFrom":[subQ1,subQ0]});Q51=makeQuery(id+"F0.imprint","IMPRINT",FACE,{"disambiguationData":[TD([[makeQuery(id+"F0.imprint","IMPRINT",EDGE,{"disambiguationData":[TD([[subQ2,-1.0]])],"derivedFrom":subQ1}),-1.0]])]});}
            var Q52;
            {var subQ0=sQuery(id+"F0.wireOp",EDGE,"E3.25.0.0");var subQ1=sQuery(id+"F0.wireOp",EDGE,"E1.1.2.0");var subQ2=makeQuery(id+"F0.imprint","INTERSECT",VERTEX,{"disambiguationData":[OD(0.0)],"derivedFrom":[subQ1,subQ0]});Q52=makeQuery(id+"F0.imprint","IMPRINT",FACE,{"disambiguationData":[TD([[makeQuery(id+"F0.imprint","IMPRINT",EDGE,{"disambiguationData":[TD([[subQ2,-1.0]])],"derivedFrom":subQ1}),1.0]])]});}
            var Q53;
            {var subQ0=sQuery(id+"F0.wireOp",EDGE,"E3.7.0.0");var subQ1=sQuery(id+"F0.wireOp",EDGE,"E1.0.2.0");var subQ2=makeQuery(id+"F0.imprint","INTERSECT",VERTEX,{"disambiguationData":[OD(0.0)],"derivedFrom":[subQ1,subQ0]});Q53=makeQuery(id+"F0.imprint","IMPRINT",FACE,{"disambiguationData":[TD([[makeQuery(id+"F0.imprint","IMPRINT",EDGE,{"disambiguationData":[TD([[subQ2,-1.0]])],"derivedFrom":subQ1}),-1.0]])]});}
            var Q54;
            {var subQ0=sQuery(id+"F0.wireOp",EDGE,"E3.9.0.0");var subQ1=sQuery(id+"F0.wireOp",EDGE,"E1.0.2.0");var subQ2=makeQuery(id+"F0.imprint","INTERSECT",VERTEX,{"disambiguationData":[OD(0.0)],"derivedFrom":[subQ1,subQ0]});Q54=makeQuery(id+"F0.imprint","IMPRINT",FACE,{"disambiguationData":[TD([[makeQuery(id+"F0.imprint","IMPRINT",EDGE,{"disambiguationData":[TD([[subQ2,-1.0]])],"derivedFrom":subQ1}),1.0]])]});}
            var Q55;
            {var subQ0=sQuery(id+"F0.wireOp",EDGE,"E3.10.1.0");var subQ1=sQuery(id+"F0.wireOp",EDGE,"E1.0.5.0");var subQ2=makeQuery(id+"F0.imprint","INTERSECT",VERTEX,{"disambiguationData":[OD(0.0)],"derivedFrom":[subQ1,subQ0]});Q55=makeQuery(id+"F0.imprint","IMPRINT",FACE,{"disambiguationData":[TD([[makeQuery(id+"F0.imprint","IMPRINT",EDGE,{"disambiguationData":[TD([[subQ2,-1.0]])],"derivedFrom":subQ1}),1.0]])]});}
            var Q56;
            {var subQ0=sQuery(id+"F0.wireOp",EDGE,"E3.43.1.0");var subQ1=sQuery(id+"F0.wireOp",EDGE,"E1.2.5.0");var subQ2=makeQuery(id+"F0.imprint","INTERSECT",VERTEX,{"disambiguationData":[OD(0.0)],"derivedFrom":[subQ1,subQ0]});Q56=makeQuery(id+"F0.imprint","IMPRINT",FACE,{"disambiguationData":[TD([[makeQuery(id+"F0.imprint","IMPRINT",EDGE,{"disambiguationData":[TD([[subQ2,-1.0]])],"derivedFrom":subQ1}),-1.0]])]});}
            var Q57;
            {var subQ0=sQuery(id+"F0.wireOp",EDGE,"E3.25.1.0");var subQ1=sQuery(id+"F0.wireOp",EDGE,"E1.1.5.0");var subQ2=makeQuery(id+"F0.imprint","INTERSECT",VERTEX,{"disambiguationData":[OD(0.0)],"derivedFrom":[subQ1,subQ0]});Q57=makeQuery(id+"F0.imprint","IMPRINT",FACE,{"disambiguationData":[TD([[makeQuery(id+"F0.imprint","IMPRINT",EDGE,{"disambiguationData":[TD([[subQ2,-1.0]])],"derivedFrom":subQ1}),1.0]])]});}
            var Q58;
            {var subQ0=sQuery(id+"F0.wireOp",EDGE,"E3.43.0.0");var subQ1=sQuery(id+"F0.wireOp",EDGE,"E1.2.2.0");var subQ2=makeQuery(id+"F0.imprint","INTERSECT",VERTEX,{"disambiguationData":[OD(0.0)],"derivedFrom":[subQ1,subQ0]});Q58=makeQuery(id+"F0.imprint","IMPRINT",FACE,{"disambiguationData":[TD([[makeQuery(id+"F0.imprint","IMPRINT",EDGE,{"disambiguationData":[TD([[subQ2,-1.0]])],"derivedFrom":subQ1}),1.0]])]});}
            var Q59;
            {var subQ0=sQuery(id+"F0.wireOp",EDGE,"E3.9.1.0");var subQ1=sQuery(id+"F0.wireOp",EDGE,"E1.0.5.0");var subQ2=makeQuery(id+"F0.imprint","INTERSECT",VERTEX,{"disambiguationData":[OD(0.0)],"derivedFrom":[subQ1,subQ0]});Q59=makeQuery(id+"F0.imprint","IMPRINT",FACE,{"disambiguationData":[TD([[makeQuery(id+"F0.imprint","IMPRINT",EDGE,{"disambiguationData":[TD([[subQ2,-1.0]])],"derivedFrom":subQ1}),1.0]])]});}
            var Q60;
            {var subQ0=sQuery(id+"F0.wireOp",EDGE,"E3.23.0.0");var subQ1=sQuery(id+"F0.wireOp",EDGE,"E1.1.2.0");var subQ2=makeQuery(id+"F0.imprint","INTERSECT",VERTEX,{"disambiguationData":[OD(0.0)],"derivedFrom":[subQ1,subQ0]});Q60=makeQuery(id+"F0.imprint","IMPRINT",FACE,{"disambiguationData":[TD([[makeQuery(id+"F0.imprint","IMPRINT",EDGE,{"disambiguationData":[TD([[subQ2,-1.0]])],"derivedFrom":subQ1}),1.0]])]});}
            var Q61;
            {var subQ0=sQuery(id+"F0.wireOp",EDGE,"E3.40.0.0");var subQ1=sQuery(id+"F0.wireOp",EDGE,"E1.2.2.0");var subQ2=makeQuery(id+"F0.imprint","INTERSECT",VERTEX,{"disambiguationData":[OD(0.0)],"derivedFrom":[subQ1,subQ0]});Q61=makeQuery(id+"F0.imprint","IMPRINT",FACE,{"disambiguationData":[TD([[makeQuery(id+"F0.imprint","IMPRINT",EDGE,{"disambiguationData":[TD([[subQ2,-1.0]])],"derivedFrom":subQ1}),1.0]])]});}
            var Q62;
            {var subQ0=sQuery(id+"F0.wireOp",EDGE,"E3.18.1.0");var subQ1=sQuery(id+"F0.wireOp",EDGE,"E1.1.5.0");var subQ2=makeQuery(id+"F0.imprint","INTERSECT",VERTEX,{"disambiguationData":[OD(0.0)],"derivedFrom":[subQ1,subQ0]});Q62=makeQuery(id+"F0.imprint","IMPRINT",FACE,{"disambiguationData":[TD([[makeQuery(id+"F0.imprint","IMPRINT",EDGE,{"disambiguationData":[TD([[subQ2,-1.0]])],"derivedFrom":subQ1}),1.0]])]});}
            var Q63;
            {var subQ0=sQuery(id+"F0.wireOp",EDGE,"E3.34.1.0");var subQ1=sQuery(id+"F0.wireOp",EDGE,"E1.2.5.0");var subQ2=makeQuery(id+"F0.imprint","INTERSECT",VERTEX,{"disambiguationData":[OD(0.0)],"derivedFrom":[subQ1,subQ0]});Q63=makeQuery(id+"F0.imprint","IMPRINT",FACE,{"disambiguationData":[TD([[makeQuery(id+"F0.imprint","IMPRINT",EDGE,{"disambiguationData":[TD([[subQ2,-1.0]])],"derivedFrom":subQ1}),1.0]])]});}
            var Q64;
            {var subQ0=sQuery(id+"F0.wireOp",EDGE,"E3.10.0.0");var subQ1=sQuery(id+"F0.wireOp",EDGE,"E1.0.2.0");var subQ2=makeQuery(id+"F0.imprint","INTERSECT",VERTEX,{"disambiguationData":[OD(0.0)],"derivedFrom":[subQ1,subQ0]});Q64=makeQuery(id+"F0.imprint","IMPRINT",FACE,{"disambiguationData":[TD([[makeQuery(id+"F0.imprint","IMPRINT",EDGE,{"disambiguationData":[TD([[subQ2,-1.0]])],"derivedFrom":subQ1}),1.0]])]});}
            var Q65;
            {var subQ0=sQuery(id+"F0.wireOp",EDGE,"E3.11.1.0");var subQ1=sQuery(id+"F0.wireOp",EDGE,"E1.0.5.0");var subQ2=makeQuery(id+"F0.imprint","INTERSECT",VERTEX,{"disambiguationData":[OD(0.0)],"derivedFrom":[subQ1,subQ0]});Q65=makeQuery(id+"F0.imprint","IMPRINT",FACE,{"disambiguationData":[TD([[makeQuery(id+"F0.imprint","IMPRINT",EDGE,{"disambiguationData":[TD([[subQ2,-1.0]])],"derivedFrom":subQ1}),1.0]])]});}
            var Q66;
            {var subQ0=sQuery(id+"F0.wireOp",EDGE,"E3.3.1.0");var subQ1=sQuery(id+"F0.wireOp",EDGE,"E1.0.5.0");var subQ2=makeQuery(id+"F0.imprint","INTERSECT",VERTEX,{"disambiguationData":[OD(0.0)],"derivedFrom":[subQ1,subQ0]});Q66=makeQuery(id+"F0.imprint","IMPRINT",FACE,{"disambiguationData":[TD([[makeQuery(id+"F0.imprint","IMPRINT",EDGE,{"disambiguationData":[TD([[subQ2,-1.0]])],"derivedFrom":subQ1}),1.0]])]});}
            var Q67;
            {var subQ0=sQuery(id+"F0.wireOp",EDGE,"E3.21.1.0");var subQ1=sQuery(id+"F0.wireOp",EDGE,"E1.1.5.0");var subQ2=makeQuery(id+"F0.imprint","INTERSECT",VERTEX,{"disambiguationData":[OD(0.0)],"derivedFrom":[subQ1,subQ0]});Q67=makeQuery(id+"F0.imprint","IMPRINT",FACE,{"disambiguationData":[TD([[makeQuery(id+"F0.imprint","IMPRINT",EDGE,{"disambiguationData":[TD([[subQ2,-1.0]])],"derivedFrom":subQ1}),1.0]])]});}
            var Q68;
            {var subQ0=sQuery(id+"F0.wireOp",EDGE,"E3.39.1.0");var subQ1=sQuery(id+"F0.wireOp",EDGE,"E1.2.5.0");var subQ2=makeQuery(id+"F0.imprint","INTERSECT",VERTEX,{"disambiguationData":[OD(0.0)],"derivedFrom":[subQ1,subQ0]});Q68=makeQuery(id+"F0.imprint","IMPRINT",FACE,{"disambiguationData":[TD([[makeQuery(id+"F0.imprint","IMPRINT",EDGE,{"disambiguationData":[TD([[subQ2,-1.0]])],"derivedFrom":subQ1}),-1.0]])]});}
            var Q69;
            {var subQ0=sQuery(id+"F0.wireOp",EDGE,"E3.37.0.0");var subQ1=sQuery(id+"F0.wireOp",EDGE,"E1.2.2.0");var subQ2=makeQuery(id+"F0.imprint","INTERSECT",VERTEX,{"disambiguationData":[OD(0.0)],"derivedFrom":[subQ1,subQ0]});Q69=makeQuery(id+"F0.imprint","IMPRINT",FACE,{"disambiguationData":[TD([[makeQuery(id+"F0.imprint","IMPRINT",EDGE,{"disambiguationData":[TD([[subQ2,-1.0]])],"derivedFrom":subQ1}),-1.0]])]});}
            var Q70;
            {var subQ0=sQuery(id+"F0.wireOp",EDGE,"E3.40.1.0");var subQ1=sQuery(id+"F0.wireOp",EDGE,"E1.2.5.0");var subQ2=makeQuery(id+"F0.imprint","INTERSECT",VERTEX,{"disambiguationData":[OD(0.0)],"derivedFrom":[subQ1,subQ0]});Q70=makeQuery(id+"F0.imprint","IMPRINT",FACE,{"disambiguationData":[TD([[makeQuery(id+"F0.imprint","IMPRINT",EDGE,{"disambiguationData":[TD([[subQ2,-1.0]])],"derivedFrom":subQ1}),1.0]])]});}
            var Q71;
            {var subQ0=sQuery(id+"F0.wireOp",EDGE,"E3.32.1.0");var subQ1=sQuery(id+"F0.wireOp",EDGE,"E1.2.5.0");var subQ2=makeQuery(id+"F0.imprint","INTERSECT",VERTEX,{"disambiguationData":[OD(0.0)],"derivedFrom":[subQ1,subQ0]});Q71=makeQuery(id+"F0.imprint","IMPRINT",FACE,{"disambiguationData":[TD([[makeQuery(id+"F0.imprint","IMPRINT",EDGE,{"disambiguationData":[TD([[subQ2,-1.0]])],"derivedFrom":subQ1}),1.0]])]});}
            var Q72;
            {var subQ0=sQuery(id+"F0.wireOp",EDGE,"E3.3.0.0");var subQ1=sQuery(id+"F0.wireOp",EDGE,"E1.0.2.0");var subQ2=makeQuery(id+"F0.imprint","INTERSECT",VERTEX,{"disambiguationData":[OD(0.0)],"derivedFrom":[subQ1,subQ0]});Q72=makeQuery(id+"F0.imprint","IMPRINT",FACE,{"disambiguationData":[TD([[makeQuery(id+"F0.imprint","IMPRINT",EDGE,{"disambiguationData":[TD([[subQ2,-1.0]])],"derivedFrom":subQ1}),1.0]])]});}
            var Q73;
            {var subQ0=sQuery(id+"F0.wireOp",EDGE,"E3.4.0.0");var subQ1=sQuery(id+"F0.wireOp",EDGE,"E1.0.2.0");var subQ2=makeQuery(id+"F0.imprint","INTERSECT",VERTEX,{"disambiguationData":[OD(0.0)],"derivedFrom":[subQ1,subQ0]});Q73=makeQuery(id+"F0.imprint","IMPRINT",FACE,{"disambiguationData":[TD([[makeQuery(id+"F0.imprint","IMPRINT",EDGE,{"disambiguationData":[TD([[subQ2,-1.0]])],"derivedFrom":subQ1}),1.0]])]});}
            var Q74;
            {var subQ0=sQuery(id+"F0.wireOp",EDGE,"E3.5.0.0");var subQ1=sQuery(id+"F0.wireOp",EDGE,"E1.0.2.0");var subQ2=makeQuery(id+"F0.imprint","INTERSECT",VERTEX,{"disambiguationData":[OD(0.0)],"derivedFrom":[subQ1,subQ0]});Q74=makeQuery(id+"F0.imprint","IMPRINT",FACE,{"disambiguationData":[TD([[makeQuery(id+"F0.imprint","IMPRINT",EDGE,{"disambiguationData":[TD([[subQ2,-1.0]])],"derivedFrom":subQ1}),1.0]])]});}
            var Q75;
            {var subQ0=sQuery(id+"F0.wireOp",EDGE,"E3.4.1.0");var subQ1=sQuery(id+"F0.wireOp",EDGE,"E1.0.5.0");var subQ2=makeQuery(id+"F0.imprint","INTERSECT",VERTEX,{"disambiguationData":[OD(0.0)],"derivedFrom":[subQ1,subQ0]});Q75=makeQuery(id+"F0.imprint","IMPRINT",FACE,{"disambiguationData":[TD([[makeQuery(id+"F0.imprint","IMPRINT",EDGE,{"disambiguationData":[TD([[subQ2,-1.0]])],"derivedFrom":subQ1}),1.0]])]});}
            var Q76;
            {var subQ0=sQuery(id+"F0.wireOp",EDGE,"E3.22.1.0");var subQ1=sQuery(id+"F0.wireOp",EDGE,"E1.1.5.0");var subQ2=makeQuery(id+"F0.imprint","INTERSECT",VERTEX,{"disambiguationData":[OD(0.0)],"derivedFrom":[subQ1,subQ0]});Q76=makeQuery(id+"F0.imprint","IMPRINT",FACE,{"disambiguationData":[TD([[makeQuery(id+"F0.imprint","IMPRINT",EDGE,{"disambiguationData":[TD([[subQ2,-1.0]])],"derivedFrom":subQ1}),1.0]])]});}
            var Q77;
            {var subQ0=sQuery(id+"F0.wireOp",EDGE,"E3.20.0.0");var subQ1=sQuery(id+"F0.wireOp",EDGE,"E1.1.2.0");var subQ2=makeQuery(id+"F0.imprint","INTERSECT",VERTEX,{"disambiguationData":[OD(0.0)],"derivedFrom":[subQ1,subQ0]});Q77=makeQuery(id+"F0.imprint","IMPRINT",FACE,{"disambiguationData":[TD([[makeQuery(id+"F0.imprint","IMPRINT",EDGE,{"disambiguationData":[TD([[subQ2,-1.0]])],"derivedFrom":subQ1}),1.0]])]});}
            var Q78;
            {var subQ0=sQuery(id+"F0.wireOp",EDGE,"E3.38.0.0");var subQ1=sQuery(id+"F0.wireOp",EDGE,"E1.2.2.0");var subQ2=makeQuery(id+"F0.imprint","INTERSECT",VERTEX,{"disambiguationData":[OD(0.0)],"derivedFrom":[subQ1,subQ0]});Q78=makeQuery(id+"F0.imprint","IMPRINT",FACE,{"disambiguationData":[TD([[makeQuery(id+"F0.imprint","IMPRINT",EDGE,{"disambiguationData":[TD([[subQ2,-1.0]])],"derivedFrom":subQ1}),-1.0]])]});}
            var Q79;
            {var subQ0=sQuery(id+"F0.wireOp",EDGE,"E3.5.1.0");var subQ1=sQuery(id+"F0.wireOp",EDGE,"E1.0.5.0");var subQ2=makeQuery(id+"F0.imprint","INTERSECT",VERTEX,{"disambiguationData":[OD(0.0)],"derivedFrom":[subQ1,subQ0]});Q79=makeQuery(id+"F0.imprint","IMPRINT",FACE,{"disambiguationData":[TD([[makeQuery(id+"F0.imprint","IMPRINT",EDGE,{"disambiguationData":[TD([[subQ2,-1.0]])],"derivedFrom":subQ1}),1.0]])]});}
            var Q80;
            {var subQ0=sQuery(id+"F0.wireOp",EDGE,"E3.8.1.0");var subQ1=sQuery(id+"F0.wireOp",EDGE,"E1.0.5.0");var subQ2=makeQuery(id+"F0.imprint","INTERSECT",VERTEX,{"disambiguationData":[OD(0.0)],"derivedFrom":[subQ1,subQ0]});Q80=makeQuery(id+"F0.imprint","IMPRINT",FACE,{"disambiguationData":[TD([[makeQuery(id+"F0.imprint","IMPRINT",EDGE,{"disambiguationData":[TD([[subQ2,-1.0]])],"derivedFrom":subQ1}),1.0]])]});}
            var Q81;
            {var subQ0=sQuery(id+"F0.wireOp",EDGE,"E3.42.0.0");var subQ1=sQuery(id+"F0.wireOp",EDGE,"E1.2.2.0");var subQ2=makeQuery(id+"F0.imprint","INTERSECT",VERTEX,{"disambiguationData":[OD(0.0)],"derivedFrom":[subQ1,subQ0]});Q81=makeQuery(id+"F0.imprint","IMPRINT",FACE,{"disambiguationData":[TD([[makeQuery(id+"F0.imprint","IMPRINT",EDGE,{"disambiguationData":[TD([[subQ2,-1.0]])],"derivedFrom":subQ1}),1.0]])]});}
            var Q82;
            {var subQ0=sQuery(id+"F0.wireOp",EDGE,"E3.33.1.0");var subQ1=sQuery(id+"F0.wireOp",EDGE,"E1.2.5.0");var subQ2=makeQuery(id+"F0.imprint","INTERSECT",VERTEX,{"disambiguationData":[OD(0.0)],"derivedFrom":[subQ1,subQ0]});Q82=makeQuery(id+"F0.imprint","IMPRINT",FACE,{"disambiguationData":[TD([[makeQuery(id+"F0.imprint","IMPRINT",EDGE,{"disambiguationData":[TD([[subQ2,-1.0]])],"derivedFrom":subQ1}),1.0]])]});}
            var Q83;
            {var subQ0=sQuery(id+"F0.wireOp",EDGE,"E3.42.1.0");var subQ1=sQuery(id+"F0.wireOp",EDGE,"E1.2.5.0");var subQ2=makeQuery(id+"F0.imprint","INTERSECT",VERTEX,{"disambiguationData":[OD(0.0)],"derivedFrom":[subQ1,subQ0]});Q83=makeQuery(id+"F0.imprint","IMPRINT",FACE,{"disambiguationData":[TD([[makeQuery(id+"F0.imprint","IMPRINT",EDGE,{"disambiguationData":[TD([[subQ2,-1.0]])],"derivedFrom":subQ1}),-1.0]])]});}
            var Q84;
            {var subQ0=sQuery(id+"F0.wireOp",EDGE,"E3.9.0.0");var subQ1=sQuery(id+"F0.wireOp",EDGE,"E1.0.2.0");var subQ2=makeQuery(id+"F0.imprint","INTERSECT",VERTEX,{"disambiguationData":[OD(0.0)],"derivedFrom":[subQ1,subQ0]});Q84=makeQuery(id+"F0.imprint","IMPRINT",FACE,{"disambiguationData":[TD([[makeQuery(id+"F0.imprint","IMPRINT",EDGE,{"disambiguationData":[TD([[subQ2,-1.0]])],"derivedFrom":subQ1}),-1.0]])]});}
            var Q85;
            {var subQ0=sQuery(id+"F0.wireOp",EDGE,"E3.40.0.0");var subQ1=sQuery(id+"F0.wireOp",EDGE,"E1.2.2.0");var subQ2=makeQuery(id+"F0.imprint","INTERSECT",VERTEX,{"disambiguationData":[OD(0.0)],"derivedFrom":[subQ1,subQ0]});Q85=makeQuery(id+"F0.imprint","IMPRINT",FACE,{"disambiguationData":[TD([[makeQuery(id+"F0.imprint","IMPRINT",EDGE,{"disambiguationData":[TD([[subQ2,-1.0]])],"derivedFrom":subQ1}),-1.0]])]});}
            var Q86;
            {var subQ0=sQuery(id+"F0.wireOp",EDGE,"E3.34.1.0");var subQ1=sQuery(id+"F0.wireOp",EDGE,"E1.2.5.0");var subQ2=makeQuery(id+"F0.imprint","INTERSECT",VERTEX,{"disambiguationData":[OD(0.0)],"derivedFrom":[subQ1,subQ0]});Q86=makeQuery(id+"F0.imprint","IMPRINT",FACE,{"disambiguationData":[TD([[makeQuery(id+"F0.imprint","IMPRINT",EDGE,{"disambiguationData":[TD([[subQ2,-1.0]])],"derivedFrom":subQ1}),-1.0]])]});}
            var Q87;
            {var subQ0=sQuery(id+"F0.wireOp",EDGE,"E3.17.0.0");var subQ1=sQuery(id+"F0.wireOp",EDGE,"E1.1.2.0");var subQ2=makeQuery(id+"F0.imprint","INTERSECT",VERTEX,{"disambiguationData":[OD(0.0)],"derivedFrom":[subQ1,subQ0]});Q87=makeQuery(id+"F0.imprint","IMPRINT",FACE,{"disambiguationData":[TD([[makeQuery(id+"F0.imprint","IMPRINT",EDGE,{"disambiguationData":[TD([[subQ2,-1.0]])],"derivedFrom":subQ1}),1.0]])]});}
            var Q88;
            {var subQ0=sQuery(id+"F0.wireOp",EDGE,"E3.43.0.0");var subQ1=sQuery(id+"F0.wireOp",EDGE,"E1.2.2.0");var subQ2=makeQuery(id+"F0.imprint","INTERSECT",VERTEX,{"disambiguationData":[OD(0.0)],"derivedFrom":[subQ1,subQ0]});Q88=makeQuery(id+"F0.imprint","IMPRINT",FACE,{"disambiguationData":[TD([[makeQuery(id+"F0.imprint","IMPRINT",EDGE,{"disambiguationData":[TD([[subQ2,-1.0]])],"derivedFrom":subQ1}),-1.0]])]});}
            var Q89;
            {var subQ0=sQuery(id+"F0.wireOp",EDGE,"E3.1.1.0");var subQ1=sQuery(id+"F0.wireOp",EDGE,"E1.0.5.0");var subQ2=makeQuery(id+"F0.imprint","INTERSECT",VERTEX,{"disambiguationData":[OD(0.0)],"derivedFrom":[subQ1,subQ0]});Q89=makeQuery(id+"F0.imprint","IMPRINT",FACE,{"disambiguationData":[TD([[makeQuery(id+"F0.imprint","IMPRINT",EDGE,{"disambiguationData":[TD([[subQ2,-1.0]])],"derivedFrom":subQ1}),1.0]])]});}
            var Q90;
            {var subQ0=sQuery(id+"F0.wireOp",EDGE,"E3.9.1.0");var subQ1=sQuery(id+"F0.wireOp",EDGE,"E1.0.5.0");var subQ2=makeQuery(id+"F0.imprint","INTERSECT",VERTEX,{"disambiguationData":[OD(0.0)],"derivedFrom":[subQ1,subQ0]});Q90=makeQuery(id+"F0.imprint","IMPRINT",FACE,{"disambiguationData":[TD([[makeQuery(id+"F0.imprint","IMPRINT",EDGE,{"disambiguationData":[TD([[subQ2,-1.0]])],"derivedFrom":subQ1}),-1.0]])]});}
            var Q91;
            {var subQ0=sQuery(id+"F0.wireOp",EDGE,"E3.42.0.0");var subQ1=sQuery(id+"F0.wireOp",EDGE,"E1.2.2.0");var subQ2=makeQuery(id+"F0.imprint","INTERSECT",VERTEX,{"disambiguationData":[OD(0.0)],"derivedFrom":[subQ1,subQ0]});Q91=makeQuery(id+"F0.imprint","IMPRINT",FACE,{"disambiguationData":[TD([[makeQuery(id+"F0.imprint","IMPRINT",EDGE,{"disambiguationData":[TD([[subQ2,-1.0]])],"derivedFrom":subQ1}),-1.0]])]});}
            var Q92;
            {var subQ0=sQuery(id+"F0.wireOp",EDGE,"E3.21.0.0");var subQ1=sQuery(id+"F0.wireOp",EDGE,"E1.1.2.0");var subQ2=makeQuery(id+"F0.imprint","INTERSECT",VERTEX,{"disambiguationData":[OD(0.0)],"derivedFrom":[subQ1,subQ0]});Q92=makeQuery(id+"F0.imprint","IMPRINT",FACE,{"disambiguationData":[TD([[makeQuery(id+"F0.imprint","IMPRINT",EDGE,{"disambiguationData":[TD([[subQ2,-1.0]])],"derivedFrom":subQ1}),-1.0]])]});}
            var Q93;
            {var subQ0=sQuery(id+"F0.wireOp",EDGE,"E3.22.0.0");var subQ1=sQuery(id+"F0.wireOp",EDGE,"E1.1.2.0");var subQ2=makeQuery(id+"F0.imprint","INTERSECT",VERTEX,{"disambiguationData":[OD(0.0)],"derivedFrom":[subQ1,subQ0]});Q93=makeQuery(id+"F0.imprint","IMPRINT",FACE,{"disambiguationData":[TD([[makeQuery(id+"F0.imprint","IMPRINT",EDGE,{"disambiguationData":[TD([[subQ2,-1.0]])],"derivedFrom":subQ1}),-1.0]])]});}
            var Q94;
            {var subQ0=sQuery(id+"F0.wireOp",EDGE,"E3.10.1.0");var subQ1=sQuery(id+"F0.wireOp",EDGE,"E1.0.5.0");var subQ2=makeQuery(id+"F0.imprint","INTERSECT",VERTEX,{"disambiguationData":[OD(0.0)],"derivedFrom":[subQ1,subQ0]});Q94=makeQuery(id+"F0.imprint","IMPRINT",FACE,{"disambiguationData":[TD([[makeQuery(id+"F0.imprint","IMPRINT",EDGE,{"disambiguationData":[TD([[subQ2,-1.0]])],"derivedFrom":subQ1}),-1.0]])]});}
            var Q95;
            {var subQ0=sQuery(id+"F0.wireOp",EDGE,"E3.8.0.0");var subQ1=sQuery(id+"F0.wireOp",EDGE,"E1.0.2.0");var subQ2=makeQuery(id+"F0.imprint","INTERSECT",VERTEX,{"disambiguationData":[OD(0.0)],"derivedFrom":[subQ1,subQ0]});Q95=makeQuery(id+"F0.imprint","IMPRINT",FACE,{"disambiguationData":[TD([[makeQuery(id+"F0.imprint","IMPRINT",EDGE,{"disambiguationData":[TD([[subQ2,-1.0]])],"derivedFrom":subQ1}),1.0]])]});}
            var Q96;
            {var subQ0=sQuery(id+"F0.wireOp",EDGE,"E3.5.1.0");var subQ1=sQuery(id+"F0.wireOp",EDGE,"E1.0.5.0");var subQ2=makeQuery(id+"F0.imprint","INTERSECT",VERTEX,{"disambiguationData":[OD(0.0)],"derivedFrom":[subQ1,subQ0]});Q96=makeQuery(id+"F0.imprint","IMPRINT",FACE,{"disambiguationData":[TD([[makeQuery(id+"F0.imprint","IMPRINT",EDGE,{"disambiguationData":[TD([[subQ2,-1.0]])],"derivedFrom":subQ1}),-1.0]])]});}
            var Q97;
            {var subQ0=sQuery(id+"F0.wireOp",EDGE,"E3.24.0.0");var subQ1=sQuery(id+"F0.wireOp",EDGE,"E1.1.2.0");var subQ2=makeQuery(id+"F0.imprint","INTERSECT",VERTEX,{"disambiguationData":[OD(0.0)],"derivedFrom":[subQ1,subQ0]});Q97=makeQuery(id+"F0.imprint","IMPRINT",FACE,{"disambiguationData":[TD([[makeQuery(id+"F0.imprint","IMPRINT",EDGE,{"disambiguationData":[TD([[subQ2,-1.0]])],"derivedFrom":subQ1}),1.0]])]});}
            var Q98;
            {var subQ0=sQuery(id+"F0.wireOp",EDGE,"E3.36.0.0");var subQ1=sQuery(id+"F0.wireOp",EDGE,"E1.2.2.0");var subQ2=makeQuery(id+"F0.imprint","INTERSECT",VERTEX,{"disambiguationData":[OD(0.0)],"derivedFrom":[subQ1,subQ0]});Q98=makeQuery(id+"F0.imprint","IMPRINT",FACE,{"disambiguationData":[TD([[makeQuery(id+"F0.imprint","IMPRINT",EDGE,{"disambiguationData":[TD([[subQ2,-1.0]])],"derivedFrom":subQ1}),1.0]])]});}
            var Q99;
            {var subQ0=sQuery(id+"F0.wireOp",EDGE,"E3.6.1.0");var subQ1=sQuery(id+"F0.wireOp",EDGE,"E1.0.5.0");var subQ2=makeQuery(id+"F0.imprint","INTERSECT",VERTEX,{"disambiguationData":[OD(0.0)],"derivedFrom":[subQ1,subQ0]});Q99=makeQuery(id+"F0.imprint","IMPRINT",FACE,{"disambiguationData":[TD([[makeQuery(id+"F0.imprint","IMPRINT",EDGE,{"disambiguationData":[TD([[subQ2,-1.0]])],"derivedFrom":subQ1}),1.0]])]});}
            var Q100;
            {var subQ0=sQuery(id+"F0.wireOp",EDGE,"E3.23.1.0");var subQ1=sQuery(id+"F0.wireOp",EDGE,"E1.1.5.0");var subQ2=makeQuery(id+"F0.imprint","INTERSECT",VERTEX,{"disambiguationData":[OD(0.0)],"derivedFrom":[subQ1,subQ0]});Q100=makeQuery(id+"F0.imprint","IMPRINT",FACE,{"disambiguationData":[TD([[makeQuery(id+"F0.imprint","IMPRINT",EDGE,{"disambiguationData":[TD([[subQ2,-1.0]])],"derivedFrom":subQ1}),-1.0]])]});}
            var Q101;
            {var subQ0=sQuery(id+"F0.wireOp",EDGE,"E3.43.1.0");var subQ1=sQuery(id+"F0.wireOp",EDGE,"E1.2.5.0");var subQ2=makeQuery(id+"F0.imprint","INTERSECT",VERTEX,{"disambiguationData":[OD(0.0)],"derivedFrom":[subQ1,subQ0]});Q101=makeQuery(id+"F0.imprint","IMPRINT",FACE,{"disambiguationData":[TD([[makeQuery(id+"F0.imprint","IMPRINT",EDGE,{"disambiguationData":[TD([[subQ2,-1.0]])],"derivedFrom":subQ1}),1.0]])]});}
            var Q102;
            {var subQ0=sQuery(id+"F0.wireOp",EDGE,"E3.17.1.0");var subQ1=sQuery(id+"F0.wireOp",EDGE,"E1.1.5.0");var subQ2=makeQuery(id+"F0.imprint","INTERSECT",VERTEX,{"disambiguationData":[OD(0.0)],"derivedFrom":[subQ1,subQ0]});Q102=makeQuery(id+"F0.imprint","IMPRINT",FACE,{"disambiguationData":[TD([[makeQuery(id+"F0.imprint","IMPRINT",EDGE,{"disambiguationData":[TD([[subQ2,-1.0]])],"derivedFrom":subQ1}),1.0]])]});}
            var Q103;
            {var subQ0=sQuery(id+"F0.wireOp",EDGE,"E3.41.0.0");var subQ1=sQuery(id+"F0.wireOp",EDGE,"E1.2.2.0");var subQ2=makeQuery(id+"F0.imprint","INTERSECT",VERTEX,{"disambiguationData":[OD(0.0)],"derivedFrom":[subQ1,subQ0]});Q103=makeQuery(id+"F0.imprint","IMPRINT",FACE,{"disambiguationData":[TD([[makeQuery(id+"F0.imprint","IMPRINT",EDGE,{"disambiguationData":[TD([[subQ2,-1.0]])],"derivedFrom":subQ1}),-1.0]])]});}
            var Q104;
            {var subQ0=sQuery(id+"F0.wireOp",EDGE,"E3.18.1.0");var subQ1=sQuery(id+"F0.wireOp",EDGE,"E1.1.5.0");var subQ2=makeQuery(id+"F0.imprint","INTERSECT",VERTEX,{"disambiguationData":[OD(0.0)],"derivedFrom":[subQ1,subQ0]});Q104=makeQuery(id+"F0.imprint","IMPRINT",FACE,{"disambiguationData":[TD([[makeQuery(id+"F0.imprint","IMPRINT",EDGE,{"disambiguationData":[TD([[subQ2,-1.0]])],"derivedFrom":subQ1}),-1.0]])]});}
            var Q105;
            {var subQ0=sQuery(id+"F0.wireOp",EDGE,"E3.26.1.0");var subQ1=sQuery(id+"F0.wireOp",EDGE,"E1.1.5.0");var subQ2=makeQuery(id+"F0.imprint","INTERSECT",VERTEX,{"disambiguationData":[OD(0.0)],"derivedFrom":[subQ1,subQ0]});Q105=makeQuery(id+"F0.imprint","IMPRINT",FACE,{"disambiguationData":[TD([[makeQuery(id+"F0.imprint","IMPRINT",EDGE,{"disambiguationData":[TD([[subQ2,-1.0]])],"derivedFrom":subQ1}),-1.0]])]});}
            var Q106;
            {var subQ0=sQuery(id+"F0.wireOp",EDGE,"E3.7.1.0");var subQ1=sQuery(id+"F0.wireOp",EDGE,"E1.0.5.0");var subQ2=makeQuery(id+"F0.imprint","INTERSECT",VERTEX,{"disambiguationData":[OD(0.0)],"derivedFrom":[subQ1,subQ0]});Q106=makeQuery(id+"F0.imprint","IMPRINT",FACE,{"disambiguationData":[TD([[makeQuery(id+"F0.imprint","IMPRINT",EDGE,{"disambiguationData":[TD([[subQ2,-1.0]])],"derivedFrom":subQ1}),-1.0]])]});}
            var Q107;
            {var subQ0=sQuery(id+"F0.wireOp",EDGE,"E3.36.1.0");var subQ1=sQuery(id+"F0.wireOp",EDGE,"E1.2.5.0");var subQ2=makeQuery(id+"F0.imprint","INTERSECT",VERTEX,{"disambiguationData":[OD(0.0)],"derivedFrom":[subQ1,subQ0]});Q107=makeQuery(id+"F0.imprint","IMPRINT",FACE,{"disambiguationData":[TD([[makeQuery(id+"F0.imprint","IMPRINT",EDGE,{"disambiguationData":[TD([[subQ2,-1.0]])],"derivedFrom":subQ1}),-1.0]])]});}
            var Q108;
            {var subQ0=sQuery(id+"F0.wireOp",EDGE,"E3.24.1.0");var subQ1=sQuery(id+"F0.wireOp",EDGE,"E1.1.5.0");var subQ2=makeQuery(id+"F0.imprint","INTERSECT",VERTEX,{"disambiguationData":[OD(0.0)],"derivedFrom":[subQ1,subQ0]});Q108=makeQuery(id+"F0.imprint","IMPRINT",FACE,{"disambiguationData":[TD([[makeQuery(id+"F0.imprint","IMPRINT",EDGE,{"disambiguationData":[TD([[subQ2,-1.0]])],"derivedFrom":subQ1}),-1.0]])]});}
            var Q109;
            {var subQ0=sQuery(id+"F0.wireOp",EDGE,"E3.26.0.0");var subQ1=sQuery(id+"F0.wireOp",EDGE,"E1.1.2.0");var subQ2=makeQuery(id+"F0.imprint","INTERSECT",VERTEX,{"disambiguationData":[OD(0.0)],"derivedFrom":[subQ1,subQ0]});Q109=makeQuery(id+"F0.imprint","IMPRINT",FACE,{"disambiguationData":[TD([[makeQuery(id+"F0.imprint","IMPRINT",EDGE,{"disambiguationData":[TD([[subQ2,-1.0]])],"derivedFrom":subQ1}),-1.0]])]});}
            var Q110;
            {var subQ0=sQuery(id+"F0.wireOp",EDGE,"E3.18.0.0");var subQ1=sQuery(id+"F0.wireOp",EDGE,"E1.1.2.0");var subQ2=makeQuery(id+"F0.imprint","INTERSECT",VERTEX,{"disambiguationData":[OD(0.0)],"derivedFrom":[subQ1,subQ0]});Q110=makeQuery(id+"F0.imprint","IMPRINT",FACE,{"disambiguationData":[TD([[makeQuery(id+"F0.imprint","IMPRINT",EDGE,{"disambiguationData":[TD([[subQ2,-1.0]])],"derivedFrom":subQ1}),-1.0]])]});}
            var Q111;
            {var subQ0=sQuery(id+"F0.wireOp",EDGE,"E3.20.1.0");var subQ1=sQuery(id+"F0.wireOp",EDGE,"E1.1.5.0");var subQ2=makeQuery(id+"F0.imprint","INTERSECT",VERTEX,{"disambiguationData":[OD(0.0)],"derivedFrom":[subQ1,subQ0]});Q111=makeQuery(id+"F0.imprint","IMPRINT",FACE,{"disambiguationData":[TD([[makeQuery(id+"F0.imprint","IMPRINT",EDGE,{"disambiguationData":[TD([[subQ2,-1.0]])],"derivedFrom":subQ1}),-1.0]])]});}
            var Q112;
            {var subQ0=sQuery(id+"F0.wireOp",EDGE,"E3.11.1.0");var subQ1=sQuery(id+"F0.wireOp",EDGE,"E1.0.5.0");var subQ2=makeQuery(id+"F0.imprint","INTERSECT",VERTEX,{"disambiguationData":[OD(0.0)],"derivedFrom":[subQ1,subQ0]});Q112=makeQuery(id+"F0.imprint","IMPRINT",FACE,{"disambiguationData":[TD([[makeQuery(id+"F0.imprint","IMPRINT",EDGE,{"disambiguationData":[TD([[subQ2,-1.0]])],"derivedFrom":subQ1}),-1.0]])]});}
            var Q113;
            {var subQ0=sQuery(id+"F0.wireOp",EDGE,"E3.3.1.0");var subQ1=sQuery(id+"F0.wireOp",EDGE,"E1.0.5.0");var subQ2=makeQuery(id+"F0.imprint","INTERSECT",VERTEX,{"disambiguationData":[OD(0.0)],"derivedFrom":[subQ1,subQ0]});Q113=makeQuery(id+"F0.imprint","IMPRINT",FACE,{"disambiguationData":[TD([[makeQuery(id+"F0.imprint","IMPRINT",EDGE,{"disambiguationData":[TD([[subQ2,-1.0]])],"derivedFrom":subQ1}),-1.0]])]});}
            var Q114;
            {var subQ0=sQuery(id+"F0.wireOp",EDGE,"E3.10.0.0");var subQ1=sQuery(id+"F0.wireOp",EDGE,"E1.0.2.0");var subQ2=makeQuery(id+"F0.imprint","INTERSECT",VERTEX,{"disambiguationData":[OD(0.0)],"derivedFrom":[subQ1,subQ0]});Q114=makeQuery(id+"F0.imprint","IMPRINT",FACE,{"disambiguationData":[TD([[makeQuery(id+"F0.imprint","IMPRINT",EDGE,{"disambiguationData":[TD([[subQ2,-1.0]])],"derivedFrom":subQ1}),-1.0]])]});}
            var Q115;
            {var subQ0=sQuery(id+"F0.wireOp",EDGE,"E3.7.0.0");var subQ1=sQuery(id+"F0.wireOp",EDGE,"E1.0.2.0");var subQ2=makeQuery(id+"F0.imprint","INTERSECT",VERTEX,{"disambiguationData":[OD(0.0)],"derivedFrom":[subQ1,subQ0]});Q115=makeQuery(id+"F0.imprint","IMPRINT",FACE,{"disambiguationData":[TD([[makeQuery(id+"F0.imprint","IMPRINT",EDGE,{"disambiguationData":[TD([[subQ2,-1.0]])],"derivedFrom":subQ1}),1.0]])]});}
            var Q116;
            {var subQ0=sQuery(id+"F0.wireOp",EDGE,"E3.3.0.0");var subQ1=sQuery(id+"F0.wireOp",EDGE,"E1.0.2.0");var subQ2=makeQuery(id+"F0.imprint","INTERSECT",VERTEX,{"disambiguationData":[OD(0.0)],"derivedFrom":[subQ1,subQ0]});Q116=makeQuery(id+"F0.imprint","IMPRINT",FACE,{"disambiguationData":[TD([[makeQuery(id+"F0.imprint","IMPRINT",EDGE,{"disambiguationData":[TD([[subQ2,-1.0]])],"derivedFrom":subQ1}),-1.0]])]});}
            var Q117;
            {var subQ0=sQuery(id+"F0.wireOp",EDGE,"E3.4.0.0");var subQ1=sQuery(id+"F0.wireOp",EDGE,"E1.0.2.0");var subQ2=makeQuery(id+"F0.imprint","INTERSECT",VERTEX,{"disambiguationData":[OD(0.0)],"derivedFrom":[subQ1,subQ0]});Q117=makeQuery(id+"F0.imprint","IMPRINT",FACE,{"disambiguationData":[TD([[makeQuery(id+"F0.imprint","IMPRINT",EDGE,{"disambiguationData":[TD([[subQ2,-1.0]])],"derivedFrom":subQ1}),-1.0]])]});}
            var Q118;
            {var subQ0=sQuery(id+"F0.wireOp",EDGE,"E3.5.0.0");var subQ1=sQuery(id+"F0.wireOp",EDGE,"E1.0.2.0");var subQ2=makeQuery(id+"F0.imprint","INTERSECT",VERTEX,{"disambiguationData":[OD(0.0)],"derivedFrom":[subQ1,subQ0]});Q118=makeQuery(id+"F0.imprint","IMPRINT",FACE,{"disambiguationData":[TD([[makeQuery(id+"F0.imprint","IMPRINT",EDGE,{"disambiguationData":[TD([[subQ2,-1.0]])],"derivedFrom":subQ1}),-1.0]])]});}
            var Q119;
            {var subQ0=sQuery(id+"F0.wireOp",EDGE,"E3.11.0.0");var subQ1=sQuery(id+"F0.wireOp",EDGE,"E1.0.2.0");var subQ2=makeQuery(id+"F0.imprint","INTERSECT",VERTEX,{"disambiguationData":[OD(0.0)],"derivedFrom":[subQ1,subQ0]});Q119=makeQuery(id+"F0.imprint","IMPRINT",FACE,{"disambiguationData":[TD([[makeQuery(id+"F0.imprint","IMPRINT",EDGE,{"disambiguationData":[TD([[subQ2,-1.0]])],"derivedFrom":subQ1}),1.0]])]});}
            var Q120;
            {var subQ0=sQuery(id+"F0.wireOp",EDGE,"E3.21.1.0");var subQ1=sQuery(id+"F0.wireOp",EDGE,"E1.1.5.0");var subQ2=makeQuery(id+"F0.imprint","INTERSECT",VERTEX,{"disambiguationData":[OD(0.0)],"derivedFrom":[subQ1,subQ0]});Q120=makeQuery(id+"F0.imprint","IMPRINT",FACE,{"disambiguationData":[TD([[makeQuery(id+"F0.imprint","IMPRINT",EDGE,{"disambiguationData":[TD([[subQ2,-1.0]])],"derivedFrom":subQ1}),-1.0]])]});}
            var Q121;
            {var subQ0=sQuery(id+"F0.wireOp",EDGE,"E3.4.1.0");var subQ1=sQuery(id+"F0.wireOp",EDGE,"E1.0.5.0");var subQ2=makeQuery(id+"F0.imprint","INTERSECT",VERTEX,{"disambiguationData":[OD(0.0)],"derivedFrom":[subQ1,subQ0]});Q121=makeQuery(id+"F0.imprint","IMPRINT",FACE,{"disambiguationData":[TD([[makeQuery(id+"F0.imprint","IMPRINT",EDGE,{"disambiguationData":[TD([[subQ2,-1.0]])],"derivedFrom":subQ1}),-1.0]])]});}
            var Q122;
            {var subQ0=sQuery(id+"F0.wireOp",EDGE,"E3.40.1.0");var subQ1=sQuery(id+"F0.wireOp",EDGE,"E1.2.5.0");var subQ2=makeQuery(id+"F0.imprint","INTERSECT",VERTEX,{"disambiguationData":[OD(0.0)],"derivedFrom":[subQ1,subQ0]});Q122=makeQuery(id+"F0.imprint","IMPRINT",FACE,{"disambiguationData":[TD([[makeQuery(id+"F0.imprint","IMPRINT",EDGE,{"disambiguationData":[TD([[subQ2,-1.0]])],"derivedFrom":subQ1}),-1.0]])]});}
            var Q123;
            {var subQ0=sQuery(id+"F0.wireOp",EDGE,"E3.20.0.0");var subQ1=sQuery(id+"F0.wireOp",EDGE,"E1.1.2.0");var subQ2=makeQuery(id+"F0.imprint","INTERSECT",VERTEX,{"disambiguationData":[OD(0.0)],"derivedFrom":[subQ1,subQ0]});Q123=makeQuery(id+"F0.imprint","IMPRINT",FACE,{"disambiguationData":[TD([[makeQuery(id+"F0.imprint","IMPRINT",EDGE,{"disambiguationData":[TD([[subQ2,-1.0]])],"derivedFrom":subQ1}),-1.0]])]});}
            var Q124;
            {var subQ0=sQuery(id+"F0.wireOp",EDGE,"E3.34.0.0");var subQ1=sQuery(id+"F0.wireOp",EDGE,"E1.2.2.0");var subQ2=makeQuery(id+"F0.imprint","INTERSECT",VERTEX,{"disambiguationData":[OD(0.0)],"derivedFrom":[subQ1,subQ0]});Q124=makeQuery(id+"F0.imprint","IMPRINT",FACE,{"disambiguationData":[TD([[makeQuery(id+"F0.imprint","IMPRINT",EDGE,{"disambiguationData":[TD([[subQ2,-1.0]])],"derivedFrom":subQ1}),1.0]])]});}
            var Q125;
            {var subQ0=sQuery(id+"F0.wireOp",EDGE,"E3.36.0.0");var subQ1=sQuery(id+"F0.wireOp",EDGE,"E1.2.2.0");var subQ2=makeQuery(id+"F0.imprint","INTERSECT",VERTEX,{"disambiguationData":[OD(0.0)],"derivedFrom":[subQ1,subQ0]});Q125=makeQuery(id+"F0.imprint","IMPRINT",FACE,{"disambiguationData":[TD([[makeQuery(id+"F0.imprint","IMPRINT",EDGE,{"disambiguationData":[TD([[subQ2,-1.0]])],"derivedFrom":subQ1}),-1.0]])]});}
            var Q126;
            {var subQ0=sQuery(id+"F0.wireOp",EDGE,"E3.1.1.0");var subQ1=sQuery(id+"F0.wireOp",EDGE,"E1.0.5.0");var subQ2=makeQuery(id+"F0.imprint","INTERSECT",VERTEX,{"disambiguationData":[OD(0.0)],"derivedFrom":[subQ1,subQ0]});Q126=makeQuery(id+"F0.imprint","IMPRINT",FACE,{"disambiguationData":[TD([[makeQuery(id+"F0.imprint","IMPRINT",EDGE,{"disambiguationData":[TD([[subQ2,-1.0]])],"derivedFrom":subQ1}),-1.0]])]});}
            var Q127;
            {var subQ0=sQuery(id+"F0.wireOp",EDGE,"E3.24.1.0");var subQ1=sQuery(id+"F0.wireOp",EDGE,"E1.1.5.0");var subQ2=makeQuery(id+"F0.imprint","INTERSECT",VERTEX,{"disambiguationData":[OD(0.0)],"derivedFrom":[subQ1,subQ0]});Q127=makeQuery(id+"F0.imprint","IMPRINT",FACE,{"disambiguationData":[TD([[makeQuery(id+"F0.imprint","IMPRINT",EDGE,{"disambiguationData":[TD([[subQ2,-1.0]])],"derivedFrom":subQ1}),1.0]])]});}
            var Q128;
            {var subQ0=sQuery(id+"F0.wireOp",EDGE,"E3.6.1.0");var subQ1=sQuery(id+"F0.wireOp",EDGE,"E1.0.5.0");var subQ2=makeQuery(id+"F0.imprint","INTERSECT",VERTEX,{"disambiguationData":[OD(0.0)],"derivedFrom":[subQ1,subQ0]});Q128=makeQuery(id+"F0.imprint","IMPRINT",FACE,{"disambiguationData":[TD([[makeQuery(id+"F0.imprint","IMPRINT",EDGE,{"disambiguationData":[TD([[subQ2,-1.0]])],"derivedFrom":subQ1}),-1.0]])]});}
            var Q129;
            {var subQ0=sQuery(id+"F0.wireOp",EDGE,"E3.19.1.0");var subQ1=sQuery(id+"F0.wireOp",EDGE,"E1.1.5.0");var subQ2=makeQuery(id+"F0.imprint","INTERSECT",VERTEX,{"disambiguationData":[OD(0.0)],"derivedFrom":[subQ1,subQ0]});Q129=makeQuery(id+"F0.imprint","IMPRINT",FACE,{"disambiguationData":[TD([[makeQuery(id+"F0.imprint","IMPRINT",EDGE,{"disambiguationData":[TD([[subQ2,-1.0]])],"derivedFrom":subQ1}),1.0]])]});}
            var Q130;
            {var subQ0=sQuery(id+"F0.wireOp",EDGE,"E3.24.0.0");var subQ1=sQuery(id+"F0.wireOp",EDGE,"E1.1.2.0");var subQ2=makeQuery(id+"F0.imprint","INTERSECT",VERTEX,{"disambiguationData":[OD(0.0)],"derivedFrom":[subQ1,subQ0]});Q130=makeQuery(id+"F0.imprint","IMPRINT",FACE,{"disambiguationData":[TD([[makeQuery(id+"F0.imprint","IMPRINT",EDGE,{"disambiguationData":[TD([[subQ2,-1.0]])],"derivedFrom":subQ1}),-1.0]])]});}
            var Q131;
            {var subQ0=sQuery(id+"F0.wireOp",EDGE,"E3.8.0.0");var subQ1=sQuery(id+"F0.wireOp",EDGE,"E1.0.2.0");var subQ2=makeQuery(id+"F0.imprint","INTERSECT",VERTEX,{"disambiguationData":[OD(0.0)],"derivedFrom":[subQ1,subQ0]});Q131=makeQuery(id+"F0.imprint","IMPRINT",FACE,{"disambiguationData":[TD([[makeQuery(id+"F0.imprint","IMPRINT",EDGE,{"disambiguationData":[TD([[subQ2,-1.0]])],"derivedFrom":subQ1}),-1.0]])]});}
            var Q132;
            {var subQ0=sQuery(id+"F0.wireOp",EDGE,"E3.17.0.0");var subQ1=sQuery(id+"F0.wireOp",EDGE,"E1.1.2.0");var subQ2=makeQuery(id+"F0.imprint","INTERSECT",VERTEX,{"disambiguationData":[OD(0.0)],"derivedFrom":[subQ1,subQ0]});Q132=makeQuery(id+"F0.imprint","IMPRINT",FACE,{"disambiguationData":[TD([[makeQuery(id+"F0.imprint","IMPRINT",EDGE,{"disambiguationData":[TD([[subQ2,-1.0]])],"derivedFrom":subQ1}),-1.0]])]});}
            var Q133;
            {var subQ0=sQuery(id+"F0.wireOp",EDGE,"E3.8.1.0");var subQ1=sQuery(id+"F0.wireOp",EDGE,"E1.0.5.0");var subQ2=makeQuery(id+"F0.imprint","INTERSECT",VERTEX,{"disambiguationData":[OD(0.0)],"derivedFrom":[subQ1,subQ0]});Q133=makeQuery(id+"F0.imprint","IMPRINT",FACE,{"disambiguationData":[TD([[makeQuery(id+"F0.imprint","IMPRINT",EDGE,{"disambiguationData":[TD([[subQ2,-1.0]])],"derivedFrom":subQ1}),-1.0]])]});}
            var Q134;
            {var subQ0=sQuery(id+"F0.wireOp",EDGE,"E3.0.1.0");var subQ1=sQuery(id+"F0.wireOp",EDGE,"E1.0.5.0");var subQ2=makeQuery(id+"F0.imprint","INTERSECT",VERTEX,{"disambiguationData":[OD(0.0)],"derivedFrom":[subQ1,subQ0]});Q134=makeQuery(id+"F0.imprint","IMPRINT",FACE,{"disambiguationData":[TD([[makeQuery(id+"F0.imprint","IMPRINT",EDGE,{"disambiguationData":[TD([[subQ2,-1.0]])],"derivedFrom":subQ1}),-1.0]])]});}
            var Q135;
            {var subQ0=sQuery(id+"F0.wireOp",EDGE,"E3.19.0.0");var subQ1=sQuery(id+"F0.wireOp",EDGE,"E1.1.2.0");var subQ2=makeQuery(id+"F0.imprint","INTERSECT",VERTEX,{"disambiguationData":[OD(0.0)],"derivedFrom":[subQ1,subQ0]});Q135=makeQuery(id+"F0.imprint","IMPRINT",FACE,{"disambiguationData":[TD([[makeQuery(id+"F0.imprint","IMPRINT",EDGE,{"disambiguationData":[TD([[subQ2,-1.0]])],"derivedFrom":subQ1}),1.0]])]});}
            var Q136;
            {var subQ0=sQuery(id+"F0.wireOp",EDGE,"E3.6.0.0");var subQ1=sQuery(id+"F0.wireOp",EDGE,"E1.0.2.0");var subQ2=makeQuery(id+"F0.imprint","INTERSECT",VERTEX,{"disambiguationData":[OD(0.0)],"derivedFrom":[subQ1,subQ0]});Q136=makeQuery(id+"F0.imprint","IMPRINT",FACE,{"disambiguationData":[TD([[makeQuery(id+"F0.imprint","IMPRINT",EDGE,{"disambiguationData":[TD([[subQ2,-1.0]])],"derivedFrom":subQ1}),1.0]])]});}
            var Q137;
            {var subQ0=sQuery(id+"F0.wireOp",EDGE,"E3.1.0.0");var subQ1=sQuery(id+"F0.wireOp",EDGE,"E1.0.2.0");var subQ2=makeQuery(id+"F0.imprint","INTERSECT",VERTEX,{"disambiguationData":[OD(0.0)],"derivedFrom":[subQ1,subQ0]});Q137=makeQuery(id+"F0.imprint","IMPRINT",FACE,{"disambiguationData":[TD([[makeQuery(id+"F0.imprint","IMPRINT",EDGE,{"disambiguationData":[TD([[subQ2,-1.0]])],"derivedFrom":subQ1}),1.0]])]});}
            var Q138;
            {var subQ0=sQuery(id+"F0.wireOp",EDGE,"E3.12.1.0");var subQ1=sQuery(id+"F0.wireOp",EDGE,"E1.0.5.0");var subQ2=makeQuery(id+"F0.imprint","INTERSECT",VERTEX,{"disambiguationData":[OD(0.0)],"derivedFrom":[subQ1,subQ0]});Q138=makeQuery(id+"F0.imprint","IMPRINT",FACE,{"disambiguationData":[TD([[makeQuery(id+"F0.imprint","IMPRINT",EDGE,{"disambiguationData":[TD([[subQ2,-1.0]])],"derivedFrom":subQ1}),1.0]])]});}
            var Q139;
            {var subQ0=sQuery(id+"F0.wireOp",EDGE,"E3.11.0.0");var subQ1=sQuery(id+"F0.wireOp",EDGE,"E1.0.2.0");var subQ2=makeQuery(id+"F0.imprint","INTERSECT",VERTEX,{"disambiguationData":[OD(0.0)],"derivedFrom":[subQ1,subQ0]});Q139=makeQuery(id+"F0.imprint","IMPRINT",FACE,{"disambiguationData":[TD([[makeQuery(id+"F0.imprint","IMPRINT",EDGE,{"disambiguationData":[TD([[subQ2,-1.0]])],"derivedFrom":subQ1}),-1.0]])]});}
            var Q140;
            {var subQ0=sQuery(id+"F0.wireOp",EDGE,"E3.17.1.0");var subQ1=sQuery(id+"F0.wireOp",EDGE,"E1.1.5.0");var subQ2=makeQuery(id+"F0.imprint","INTERSECT",VERTEX,{"disambiguationData":[OD(0.0)],"derivedFrom":[subQ1,subQ0]});Q140=makeQuery(id+"F0.imprint","IMPRINT",FACE,{"disambiguationData":[TD([[makeQuery(id+"F0.imprint","IMPRINT",EDGE,{"disambiguationData":[TD([[subQ2,-1.0]])],"derivedFrom":subQ1}),-1.0]])]});}
            var Q141;
            {var subQ0=sQuery(id+"F0.wireOp",EDGE,"E3.23.0.0");var subQ1=sQuery(id+"F0.wireOp",EDGE,"E1.1.2.0");var subQ2=makeQuery(id+"F0.imprint","INTERSECT",VERTEX,{"disambiguationData":[OD(0.0)],"derivedFrom":[subQ1,subQ0]});Q141=makeQuery(id+"F0.imprint","IMPRINT",FACE,{"disambiguationData":[TD([[makeQuery(id+"F0.imprint","IMPRINT",EDGE,{"disambiguationData":[TD([[subQ2,-1.0]])],"derivedFrom":subQ1}),-1.0]])]});}
            var Q142;
            {var subQ0=sQuery(id+"F0.wireOp",EDGE,"E3.22.1.0");var subQ1=sQuery(id+"F0.wireOp",EDGE,"E1.1.5.0");var subQ2=makeQuery(id+"F0.imprint","INTERSECT",VERTEX,{"disambiguationData":[OD(0.0)],"derivedFrom":[subQ1,subQ0]});Q142=makeQuery(id+"F0.imprint","IMPRINT",FACE,{"disambiguationData":[TD([[makeQuery(id+"F0.imprint","IMPRINT",EDGE,{"disambiguationData":[TD([[subQ2,-1.0]])],"derivedFrom":subQ1}),-1.0]])]});}
            var Q143;
            {var subQ0=sQuery(id+"F0.wireOp",EDGE,"E3.36.1.0");var subQ1=sQuery(id+"F0.wireOp",EDGE,"E1.2.5.0");var subQ2=makeQuery(id+"F0.imprint","INTERSECT",VERTEX,{"disambiguationData":[OD(0.0)],"derivedFrom":[subQ1,subQ0]});Q143=makeQuery(id+"F0.imprint","IMPRINT",FACE,{"disambiguationData":[TD([[makeQuery(id+"F0.imprint","IMPRINT",EDGE,{"disambiguationData":[TD([[subQ2,-1.0]])],"derivedFrom":subQ1}),1.0]])]});}
            var Q144;
            {var subQ0=sQuery(id+"F0.wireOp",EDGE,"E3.41.1.0");var subQ1=sQuery(id+"F0.wireOp",EDGE,"E1.2.5.0");var subQ2=makeQuery(id+"F0.imprint","INTERSECT",VERTEX,{"disambiguationData":[OD(0.0)],"derivedFrom":[subQ1,subQ0]});Q144=makeQuery(id+"F0.imprint","IMPRINT",FACE,{"disambiguationData":[TD([[makeQuery(id+"F0.imprint","IMPRINT",EDGE,{"disambiguationData":[TD([[subQ2,-1.0]])],"derivedFrom":subQ1}),1.0]])]});}
            var Q145;
            {var subQ0=sQuery(id+"F0.wireOp",EDGE,"E3.39.0.0");var subQ1=sQuery(id+"F0.wireOp",EDGE,"E1.2.2.0");var subQ2=makeQuery(id+"F0.imprint","INTERSECT",VERTEX,{"disambiguationData":[OD(0.0)],"derivedFrom":[subQ1,subQ0]});Q145=makeQuery(id+"F0.imprint","IMPRINT",FACE,{"disambiguationData":[TD([[makeQuery(id+"F0.imprint","IMPRINT",EDGE,{"disambiguationData":[TD([[subQ2,-1.0]])],"derivedFrom":subQ1}),1.0]])]});}
            var Q146;
            {var subQ0=sQuery(id+"F0.wireOp",EDGE,"E3.25.0.0");var subQ1=sQuery(id+"F0.wireOp",EDGE,"E1.1.2.0");var subQ2=makeQuery(id+"F0.imprint","INTERSECT",VERTEX,{"disambiguationData":[OD(0.0)],"derivedFrom":[subQ1,subQ0]});Q146=makeQuery(id+"F0.imprint","IMPRINT",FACE,{"disambiguationData":[TD([[makeQuery(id+"F0.imprint","IMPRINT",EDGE,{"disambiguationData":[TD([[subQ2,-1.0]])],"derivedFrom":subQ1}),-1.0]])]});}
            var Q147;
            {var subQ0=sQuery(id+"F0.wireOp",EDGE,"E3.2.1.0");var subQ1=sQuery(id+"F0.wireOp",EDGE,"E1.0.5.0");var subQ2=makeQuery(id+"F0.imprint","INTERSECT",VERTEX,{"disambiguationData":[OD(0.0)],"derivedFrom":[subQ1,subQ0]});Q147=makeQuery(id+"F0.imprint","IMPRINT",FACE,{"disambiguationData":[TD([[makeQuery(id+"F0.imprint","IMPRINT",EDGE,{"disambiguationData":[TD([[subQ2,-1.0]])],"derivedFrom":subQ1}),1.0]])]});}
            var Q148;
            {var subQ0=sQuery(id+"F0.wireOp",EDGE,"E3.19.1.0");var subQ1=sQuery(id+"F0.wireOp",EDGE,"E1.1.5.0");var subQ2=makeQuery(id+"F0.imprint","INTERSECT",VERTEX,{"disambiguationData":[OD(0.0)],"derivedFrom":[subQ1,subQ0]});Q148=makeQuery(id+"F0.imprint","IMPRINT",FACE,{"disambiguationData":[TD([[makeQuery(id+"F0.imprint","IMPRINT",EDGE,{"disambiguationData":[TD([[subQ2,-1.0]])],"derivedFrom":subQ1}),-1.0]])]});}
            var Q149;
            {var subQ0=sQuery(id+"F0.wireOp",EDGE,"E3.6.0.0");var subQ1=sQuery(id+"F0.wireOp",EDGE,"E1.0.2.0");var subQ2=makeQuery(id+"F0.imprint","INTERSECT",VERTEX,{"disambiguationData":[OD(0.0)],"derivedFrom":[subQ1,subQ0]});Q149=makeQuery(id+"F0.imprint","IMPRINT",FACE,{"disambiguationData":[TD([[makeQuery(id+"F0.imprint","IMPRINT",EDGE,{"disambiguationData":[TD([[subQ2,-1.0]])],"derivedFrom":subQ1}),-1.0]])]});}
            var Q150;
            {var subQ0=sQuery(id+"F0.wireOp",EDGE,"E3.1.0.0");var subQ1=sQuery(id+"F0.wireOp",EDGE,"E1.0.2.0");var subQ2=makeQuery(id+"F0.imprint","INTERSECT",VERTEX,{"disambiguationData":[OD(0.0)],"derivedFrom":[subQ1,subQ0]});Q150=makeQuery(id+"F0.imprint","IMPRINT",FACE,{"disambiguationData":[TD([[makeQuery(id+"F0.imprint","IMPRINT",EDGE,{"disambiguationData":[TD([[subQ2,-1.0]])],"derivedFrom":subQ1}),-1.0]])]});}
            var Q151;
            {var subQ0=sQuery(id+"F0.wireOp",EDGE,"E3.19.0.0");var subQ1=sQuery(id+"F0.wireOp",EDGE,"E1.1.2.0");var subQ2=makeQuery(id+"F0.imprint","INTERSECT",VERTEX,{"disambiguationData":[OD(0.0)],"derivedFrom":[subQ1,subQ0]});Q151=makeQuery(id+"F0.imprint","IMPRINT",FACE,{"disambiguationData":[TD([[makeQuery(id+"F0.imprint","IMPRINT",EDGE,{"disambiguationData":[TD([[subQ2,-1.0]])],"derivedFrom":subQ1}),-1.0]])]});}
            var Q152;
            {var subQ0=sQuery(id+"F0.wireOp",EDGE,"E3.12.1.0");var subQ1=sQuery(id+"F0.wireOp",EDGE,"E1.0.5.0");var subQ2=makeQuery(id+"F0.imprint","INTERSECT",VERTEX,{"disambiguationData":[OD(0.0)],"derivedFrom":[subQ1,subQ0]});Q152=makeQuery(id+"F0.imprint","IMPRINT",FACE,{"disambiguationData":[TD([[makeQuery(id+"F0.imprint","IMPRINT",EDGE,{"disambiguationData":[TD([[subQ2,-1.0]])],"derivedFrom":subQ1}),-1.0]])]});}
            var Q153;
            {var subQ0=sQuery(id+"F0.wireOp",EDGE,"E3.0.1.0");var subQ1=sQuery(id+"F0.wireOp",EDGE,"E1.0.5.0");var subQ2=makeQuery(id+"F0.imprint","INTERSECT",VERTEX,{"disambiguationData":[OD(0.0)],"derivedFrom":[subQ1,subQ0]});Q153=makeQuery(id+"F0.imprint","IMPRINT",FACE,{"disambiguationData":[TD([[makeQuery(id+"F0.imprint","IMPRINT",EDGE,{"disambiguationData":[TD([[subQ2,-1.0]])],"derivedFrom":subQ1}),1.0]])]});}
            var Q154;
            {var subQ0=sQuery(id+"F0.wireOp",EDGE,"E3.12.0.0");var subQ1=sQuery(id+"F0.wireOp",EDGE,"E1.0.2.0");var subQ2=makeQuery(id+"F0.imprint","INTERSECT",VERTEX,{"disambiguationData":[OD(0.0)],"derivedFrom":[subQ1,subQ0]});Q154=makeQuery(id+"F0.imprint","IMPRINT",FACE,{"disambiguationData":[TD([[makeQuery(id+"F0.imprint","IMPRINT",EDGE,{"disambiguationData":[TD([[subQ2,-1.0]])],"derivedFrom":subQ1}),1.0]])]});}
            var Q155;
            {var subQ0=sQuery(id+"F0.wireOp",EDGE,"E3.25.1.0");var subQ1=sQuery(id+"F0.wireOp",EDGE,"E1.1.5.0");var subQ2=makeQuery(id+"F0.imprint","INTERSECT",VERTEX,{"disambiguationData":[OD(0.0)],"derivedFrom":[subQ1,subQ0]});Q155=makeQuery(id+"F0.imprint","IMPRINT",FACE,{"disambiguationData":[TD([[makeQuery(id+"F0.imprint","IMPRINT",EDGE,{"disambiguationData":[TD([[subQ2,-1.0]])],"derivedFrom":subQ1}),-1.0]])]});}
            var Q156;
            {var subQ0=sQuery(id+"F0.wireOp",EDGE,"E3.27.1.0");var subQ1=sQuery(id+"F0.wireOp",EDGE,"E1.1.5.0");var subQ2=makeQuery(id+"F0.imprint","INTERSECT",VERTEX,{"disambiguationData":[OD(0.0)],"derivedFrom":[subQ1,subQ0]});Q156=makeQuery(id+"F0.imprint","IMPRINT",FACE,{"disambiguationData":[TD([[makeQuery(id+"F0.imprint","IMPRINT",EDGE,{"disambiguationData":[TD([[subQ2,-1.0]])],"derivedFrom":subQ1}),1.0]])]});}
            var Q157;
            {var subQ0=sQuery(id+"F0.wireOp",EDGE,"E3.31.0.0");var subQ1=sQuery(id+"F0.wireOp",EDGE,"E1.2.2.0");var subQ2=makeQuery(id+"F0.imprint","INTERSECT",VERTEX,{"disambiguationData":[OD(0.0)],"derivedFrom":[subQ1,subQ0]});Q157=makeQuery(id+"F0.imprint","IMPRINT",FACE,{"disambiguationData":[TD([[makeQuery(id+"F0.imprint","IMPRINT",EDGE,{"disambiguationData":[TD([[subQ2,-1.0]])],"derivedFrom":subQ1}),-1.0]])]});}
            var Q158;
            {var subQ0=sQuery(id+"F0.wireOp",EDGE,"E3.2.1.0");var subQ1=sQuery(id+"F0.wireOp",EDGE,"E1.0.5.0");var subQ2=makeQuery(id+"F0.imprint","INTERSECT",VERTEX,{"disambiguationData":[OD(0.0)],"derivedFrom":[subQ1,subQ0]});Q158=makeQuery(id+"F0.imprint","IMPRINT",FACE,{"disambiguationData":[TD([[makeQuery(id+"F0.imprint","IMPRINT",EDGE,{"disambiguationData":[TD([[subQ2,-1.0]])],"derivedFrom":subQ1}),-1.0]])]});}
            var Q159;
            {var subQ0=sQuery(id+"F0.wireOp",EDGE,"E3.15.1.0");var subQ1=sQuery(id+"F0.wireOp",EDGE,"E1.1.5.0");var subQ2=makeQuery(id+"F0.imprint","INTERSECT",VERTEX,{"disambiguationData":[OD(0.0)],"derivedFrom":[subQ1,subQ0]});Q159=makeQuery(id+"F0.imprint","IMPRINT",FACE,{"disambiguationData":[TD([[makeQuery(id+"F0.imprint","IMPRINT",EDGE,{"disambiguationData":[TD([[subQ2,-1.0]])],"derivedFrom":subQ1}),-1.0]])]});}
            var Q160;
            {var subQ0=sQuery(id+"F0.wireOp",EDGE,"E3.13.1.0");var subQ1=sQuery(id+"F0.wireOp",EDGE,"E1.0.5.0");var subQ2=makeQuery(id+"F0.imprint","INTERSECT",VERTEX,{"disambiguationData":[OD(0.0)],"derivedFrom":[subQ1,subQ0]});Q160=makeQuery(id+"F0.imprint","IMPRINT",FACE,{"disambiguationData":[TD([[makeQuery(id+"F0.imprint","IMPRINT",EDGE,{"disambiguationData":[TD([[subQ2,-1.0]])],"derivedFrom":subQ1}),-1.0]])]});}
            var Q161;
            {var subQ0=sQuery(id+"F0.wireOp",EDGE,"E3.13.0.0");var subQ1=sQuery(id+"F0.wireOp",EDGE,"E1.0.2.0");var subQ2=makeQuery(id+"F0.imprint","INTERSECT",VERTEX,{"disambiguationData":[OD(0.0)],"derivedFrom":[subQ1,subQ0]});Q161=makeQuery(id+"F0.imprint","IMPRINT",FACE,{"disambiguationData":[TD([[makeQuery(id+"F0.imprint","IMPRINT",EDGE,{"disambiguationData":[TD([[subQ2,-1.0]])],"derivedFrom":subQ1}),1.0]])]});}
            var Q162;
            {var subQ0=sQuery(id+"F0.wireOp",EDGE,"E3.16.0.0");var subQ1=sQuery(id+"F0.wireOp",EDGE,"E1.1.2.0");var subQ2=makeQuery(id+"F0.imprint","INTERSECT",VERTEX,{"disambiguationData":[OD(0.0)],"derivedFrom":[subQ1,subQ0]});Q162=makeQuery(id+"F0.imprint","IMPRINT",FACE,{"disambiguationData":[TD([[makeQuery(id+"F0.imprint","IMPRINT",EDGE,{"disambiguationData":[TD([[subQ2,-1.0]])],"derivedFrom":subQ1}),1.0]])]});}
            var Q163;
            {var subQ0=sQuery(id+"F0.wireOp",EDGE,"E3.14.1.0");var subQ1=sQuery(id+"F0.wireOp",EDGE,"E1.0.5.0");var subQ2=makeQuery(id+"F0.imprint","INTERSECT",VERTEX,{"disambiguationData":[OD(0.0)],"derivedFrom":[subQ1,subQ0]});Q163=makeQuery(id+"F0.imprint","IMPRINT",FACE,{"disambiguationData":[TD([[makeQuery(id+"F0.imprint","IMPRINT",EDGE,{"disambiguationData":[TD([[subQ2,-1.0]])],"derivedFrom":subQ1}),1.0]])]});}
            var Q164;
            {var subQ0=sQuery(id+"F0.wireOp",EDGE,"E3.16.1.0");var subQ1=sQuery(id+"F0.wireOp",EDGE,"E1.1.5.0");var subQ2=makeQuery(id+"F0.imprint","INTERSECT",VERTEX,{"disambiguationData":[OD(0.0)],"derivedFrom":[subQ1,subQ0]});Q164=makeQuery(id+"F0.imprint","IMPRINT",FACE,{"disambiguationData":[TD([[makeQuery(id+"F0.imprint","IMPRINT",EDGE,{"disambiguationData":[TD([[subQ2,-1.0]])],"derivedFrom":subQ1}),-1.0]])]});}
            var Q165;
            {var subQ0=sQuery(id+"F0.wireOp",EDGE,"E3.15.0.0");var subQ1=sQuery(id+"F0.wireOp",EDGE,"E1.1.2.0");var subQ2=makeQuery(id+"F0.imprint","INTERSECT",VERTEX,{"disambiguationData":[OD(0.0)],"derivedFrom":[subQ1,subQ0]});Q165=makeQuery(id+"F0.imprint","IMPRINT",FACE,{"disambiguationData":[TD([[makeQuery(id+"F0.imprint","IMPRINT",EDGE,{"disambiguationData":[TD([[subQ2,-1.0]])],"derivedFrom":subQ1}),1.0]])]});}
            var Q166;
            {var subQ0=sQuery(id+"F0.wireOp",EDGE,"E3.14.0.0");var subQ1=sQuery(id+"F0.wireOp",EDGE,"E1.0.2.0");var subQ2=makeQuery(id+"F0.imprint","INTERSECT",VERTEX,{"disambiguationData":[OD(0.0)],"derivedFrom":[subQ1,subQ0]});Q166=makeQuery(id+"F0.imprint","IMPRINT",FACE,{"disambiguationData":[TD([[makeQuery(id+"F0.imprint","IMPRINT",EDGE,{"disambiguationData":[TD([[subQ2,-1.0]])],"derivedFrom":subQ1}),1.0]])]});}
            var Q167;
            {var subQ0=sQuery(id+"F0.wireOp",EDGE,"E3.31.1.0");var subQ1=sQuery(id+"F0.wireOp",EDGE,"E1.2.5.0");var subQ2=makeQuery(id+"F0.imprint","INTERSECT",VERTEX,{"disambiguationData":[OD(0.0)],"derivedFrom":[subQ1,subQ0]});Q167=makeQuery(id+"F0.imprint","IMPRINT",FACE,{"disambiguationData":[TD([[makeQuery(id+"F0.imprint","IMPRINT",EDGE,{"disambiguationData":[TD([[subQ2,-1.0]])],"derivedFrom":subQ1}),1.0]])]});}
            var Q168;
            {var subQ0=sQuery(id+"F0.wireOp",EDGE,"E3.27.0.0");var subQ1=sQuery(id+"F0.wireOp",EDGE,"E1.1.2.0");var subQ2=makeQuery(id+"F0.imprint","INTERSECT",VERTEX,{"disambiguationData":[OD(0.0)],"derivedFrom":[subQ1,subQ0]});Q168=makeQuery(id+"F0.imprint","IMPRINT",FACE,{"disambiguationData":[TD([[makeQuery(id+"F0.imprint","IMPRINT",EDGE,{"disambiguationData":[TD([[subQ2,-1.0]])],"derivedFrom":subQ1}),1.0]])]});}
            var Q169;
            {var subQ0=sQuery(id+"F0.wireOp",EDGE,"E2");var subQ1=sQuery(id+"F0.wireOp",EDGE,"E1.0.2.0");var subQ2=makeQuery(id+"F0.imprint","INTERSECT",VERTEX,{"disambiguationData":[OD(0.0)],"derivedFrom":[subQ1,subQ0]});Q169=makeQuery(id+"F0.imprint","IMPRINT",FACE,{"disambiguationData":[TD([[makeQuery(id+"F0.imprint","IMPRINT",EDGE,{"disambiguationData":[TD([[subQ2,-1.0]])],"derivedFrom":subQ1}),1.0]])]});}
            var Q170;
            {var subQ0=sQuery(id+"F0.wireOp",EDGE,"E3.2.0.0");var subQ1=sQuery(id+"F0.wireOp",EDGE,"E1.0.2.0");var subQ2=makeQuery(id+"F0.imprint","INTERSECT",VERTEX,{"disambiguationData":[OD(0.0)],"derivedFrom":[subQ1,subQ0]});Q170=makeQuery(id+"F0.imprint","IMPRINT",FACE,{"disambiguationData":[TD([[makeQuery(id+"F0.imprint","IMPRINT",EDGE,{"disambiguationData":[TD([[subQ2,-1.0]])],"derivedFrom":subQ1}),1.0]])]});}
            var Q171;
            {var subQ1=sQuery(id+"F0.wireOp",EDGE,"E1.2.2.0");var subQ3=sQuery(id+"F0.wireOp",EDGE,"E3.29.0.0");var subQ4=makeQuery(id+"F0.imprint","INTERSECT",VERTEX,{"derivedFrom":[subQ1,subQ3]});Q171=makeQuery(id+"F0.imprint","IMPRINT",FACE,{"disambiguationData":[TD([[makeQuery(id+"F0.imprint","IMPRINT",EDGE,{"disambiguationData":[TD([[subQ4,-1.0]])],"derivedFrom":subQ3}),1.0]])]});}
            var Q172;
            {var subQ1=sQuery(id+"F0.wireOp",EDGE,"E1.2.4.1");var subQ3=sQuery(id+"F0.wireOp",EDGE,"E3.29.1.0");var subQ4=makeQuery(id+"F0.imprint","INTERSECT",VERTEX,{"derivedFrom":[subQ1,subQ3]});Q172=makeQuery(id+"F0.imprint","IMPRINT",FACE,{"disambiguationData":[TD([[makeQuery(id+"F0.imprint","IMPRINT",EDGE,{"disambiguationData":[TD([[subQ4,-1.0]])],"derivedFrom":subQ3}),1.0]])]});}
            var Q173;
            {var subQ0=sQuery(id+"F0.wireOp",EDGE,"E3.16.0.0");var subQ1=sQuery(id+"F0.wireOp",EDGE,"E1.1.2.0");var subQ2=makeQuery(id+"F0.imprint","INTERSECT",VERTEX,{"disambiguationData":[OD(0.0)],"derivedFrom":[subQ1,subQ0]});Q173=makeQuery(id+"F0.imprint","IMPRINT",FACE,{"disambiguationData":[TD([[makeQuery(id+"F0.imprint","IMPRINT",EDGE,{"disambiguationData":[TD([[subQ2,-1.0]])],"derivedFrom":subQ1}),-1.0]])]});}
            var Q174;
            {var subQ0=sQuery(id+"F0.wireOp",EDGE,"E3.15.1.0");var subQ1=sQuery(id+"F0.wireOp",EDGE,"E1.1.5.0");var subQ2=makeQuery(id+"F0.imprint","INTERSECT",VERTEX,{"disambiguationData":[OD(0.0)],"derivedFrom":[subQ1,subQ0]});Q174=makeQuery(id+"F0.imprint","IMPRINT",FACE,{"disambiguationData":[TD([[makeQuery(id+"F0.imprint","IMPRINT",EDGE,{"disambiguationData":[TD([[subQ2,-1.0]])],"derivedFrom":subQ1}),1.0]])]});}
            var Q175;
            {var subQ0=sQuery(id+"F0.wireOp",EDGE,"E3.16.1.0");var subQ1=sQuery(id+"F0.wireOp",EDGE,"E1.1.5.0");var subQ2=makeQuery(id+"F0.imprint","INTERSECT",VERTEX,{"disambiguationData":[OD(0.0)],"derivedFrom":[subQ1,subQ0]});Q175=makeQuery(id+"F0.imprint","IMPRINT",FACE,{"disambiguationData":[TD([[makeQuery(id+"F0.imprint","IMPRINT",EDGE,{"disambiguationData":[TD([[subQ2,-1.0]])],"derivedFrom":subQ1}),1.0]])]});}
            var Q176;
            {var subQ0=sQuery(id+"F0.wireOp",EDGE,"E3.13.0.0");var subQ1=sQuery(id+"F0.wireOp",EDGE,"E1.0.2.0");var subQ2=makeQuery(id+"F0.imprint","INTERSECT",VERTEX,{"disambiguationData":[OD(0.0)],"derivedFrom":[subQ1,subQ0]});Q176=makeQuery(id+"F0.imprint","IMPRINT",FACE,{"disambiguationData":[TD([[makeQuery(id+"F0.imprint","IMPRINT",EDGE,{"disambiguationData":[TD([[subQ2,-1.0]])],"derivedFrom":subQ1}),-1.0]])]});}
            var Q177;
            {var subQ1=sQuery(id+"F0.wireOp",EDGE,"E1.1.2.0");var subQ3=sQuery(id+"F0.wireOp",EDGE,"E3.29.0.0");var subQ4=makeQuery(id+"F0.imprint","INTERSECT",VERTEX,{"derivedFrom":[subQ1,subQ3]});Q177=makeQuery(id+"F0.imprint","IMPRINT",FACE,{"disambiguationData":[TD([[makeQuery(id+"F0.imprint","IMPRINT",EDGE,{"disambiguationData":[TD([[subQ4,-1.0]])],"derivedFrom":subQ3}),1.0]])]});}
            var Q178;
            {var subQ0=sQuery(id+"F0.wireOp",EDGE,"E3.14.1.0");var subQ1=sQuery(id+"F0.wireOp",EDGE,"E1.0.5.0");var subQ2=makeQuery(id+"F0.imprint","INTERSECT",VERTEX,{"disambiguationData":[OD(0.0)],"derivedFrom":[subQ1,subQ0]});Q178=makeQuery(id+"F0.imprint","IMPRINT",FACE,{"disambiguationData":[TD([[makeQuery(id+"F0.imprint","IMPRINT",EDGE,{"disambiguationData":[TD([[subQ2,-1.0]])],"derivedFrom":subQ1}),-1.0]])]});}
            var Q179;
            {var subQ0=sQuery(id+"F0.wireOp",EDGE,"E3.27.1.0");var subQ1=sQuery(id+"F0.wireOp",EDGE,"E1.1.5.0");var subQ2=makeQuery(id+"F0.imprint","INTERSECT",VERTEX,{"disambiguationData":[OD(0.0)],"derivedFrom":[subQ1,subQ0]});Q179=makeQuery(id+"F0.imprint","IMPRINT",FACE,{"disambiguationData":[TD([[makeQuery(id+"F0.imprint","IMPRINT",EDGE,{"disambiguationData":[TD([[subQ2,-1.0]])],"derivedFrom":subQ1}),-1.0]])]});}
            var Q180;
            {var subQ0=sQuery(id+"F0.wireOp",EDGE,"E3.14.0.0");var subQ1=sQuery(id+"F0.wireOp",EDGE,"E1.0.2.0");var subQ2=makeQuery(id+"F0.imprint","INTERSECT",VERTEX,{"disambiguationData":[OD(0.0)],"derivedFrom":[subQ1,subQ0]});Q180=makeQuery(id+"F0.imprint","IMPRINT",FACE,{"disambiguationData":[TD([[makeQuery(id+"F0.imprint","IMPRINT",EDGE,{"disambiguationData":[TD([[subQ2,-1.0]])],"derivedFrom":subQ1}),-1.0]])]});}
            var Q181;
            {var subQ0=sQuery(id+"F0.wireOp",EDGE,"E3.31.1.0");var subQ1=sQuery(id+"F0.wireOp",EDGE,"E1.2.5.0");var subQ2=makeQuery(id+"F0.imprint","INTERSECT",VERTEX,{"disambiguationData":[OD(0.0)],"derivedFrom":[subQ1,subQ0]});Q181=makeQuery(id+"F0.imprint","IMPRINT",FACE,{"disambiguationData":[TD([[makeQuery(id+"F0.imprint","IMPRINT",EDGE,{"disambiguationData":[TD([[subQ2,-1.0]])],"derivedFrom":subQ1}),-1.0]])]});}
            var Q182;
            {var subQ0=sQuery(id+"F0.wireOp",EDGE,"E2");var subQ1=sQuery(id+"F0.wireOp",EDGE,"E1.0.2.0");var subQ2=makeQuery(id+"F0.imprint","INTERSECT",VERTEX,{"disambiguationData":[OD(0.0)],"derivedFrom":[subQ1,subQ0]});Q182=makeQuery(id+"F0.imprint","IMPRINT",FACE,{"disambiguationData":[TD([[makeQuery(id+"F0.imprint","IMPRINT",EDGE,{"disambiguationData":[TD([[subQ2,-1.0]])],"derivedFrom":subQ1}),-1.0]])]});}
            var Q183;
            {var subQ1=sQuery(id+"F0.wireOp",EDGE,"E1.2.1.1");var subQ3=sQuery(id+"F0.wireOp",EDGE,"E3.29.0.0");var subQ4=makeQuery(id+"F0.imprint","INTERSECT",VERTEX,{"derivedFrom":[subQ1,subQ3]});Q183=makeQuery(id+"F0.imprint","IMPRINT",FACE,{"disambiguationData":[TD([[makeQuery(id+"F0.imprint","IMPRINT",EDGE,{"disambiguationData":[TD([[subQ4,-1.0]])],"derivedFrom":subQ3}),1.0]])]});}
            var Q184;
            {var subQ0=sQuery(id+"F0.wireOp",EDGE,"E3.2.0.0");var subQ1=sQuery(id+"F0.wireOp",EDGE,"E1.0.2.0");var subQ2=makeQuery(id+"F0.imprint","INTERSECT",VERTEX,{"disambiguationData":[OD(0.0)],"derivedFrom":[subQ1,subQ0]});Q184=makeQuery(id+"F0.imprint","IMPRINT",FACE,{"disambiguationData":[TD([[makeQuery(id+"F0.imprint","IMPRINT",EDGE,{"disambiguationData":[TD([[subQ2,-1.0]])],"derivedFrom":subQ1}),-1.0]])]});}
            var Q185;
            {var subQ0=sQuery(id+"F0.wireOp",EDGE,"E3.27.0.0");var subQ1=sQuery(id+"F0.wireOp",EDGE,"E1.1.2.0");var subQ2=makeQuery(id+"F0.imprint","INTERSECT",VERTEX,{"disambiguationData":[OD(0.0)],"derivedFrom":[subQ1,subQ0]});Q185=makeQuery(id+"F0.imprint","IMPRINT",FACE,{"disambiguationData":[TD([[makeQuery(id+"F0.imprint","IMPRINT",EDGE,{"disambiguationData":[TD([[subQ2,-1.0]])],"derivedFrom":subQ1}),-1.0]])]});}
            var Q186;
            {var subQ0=sQuery(id+"F0.wireOp",EDGE,"E3.13.1.0");var subQ1=sQuery(id+"F0.wireOp",EDGE,"E1.0.5.0");var subQ2=makeQuery(id+"F0.imprint","INTERSECT",VERTEX,{"disambiguationData":[OD(0.0)],"derivedFrom":[subQ1,subQ0]});Q186=makeQuery(id+"F0.imprint","IMPRINT",FACE,{"disambiguationData":[TD([[makeQuery(id+"F0.imprint","IMPRINT",EDGE,{"disambiguationData":[TD([[subQ2,-1.0]])],"derivedFrom":subQ1}),1.0]])]});}
            var Q187;
            {var subQ0=sQuery(id+"F0.wireOp",EDGE,"E3.31.0.0");var subQ1=sQuery(id+"F0.wireOp",EDGE,"E1.2.2.0");var subQ2=makeQuery(id+"F0.imprint","INTERSECT",VERTEX,{"disambiguationData":[OD(0.0)],"derivedFrom":[subQ1,subQ0]});Q187=makeQuery(id+"F0.imprint","IMPRINT",FACE,{"disambiguationData":[TD([[makeQuery(id+"F0.imprint","IMPRINT",EDGE,{"disambiguationData":[TD([[subQ2,-1.0]])],"derivedFrom":subQ1}),1.0]])]});}
            var Q188;
            {var subQ0=sQuery(id+"F0.wireOp",EDGE,"E3.15.0.0");var subQ1=sQuery(id+"F0.wireOp",EDGE,"E1.1.2.0");var subQ2=makeQuery(id+"F0.imprint","INTERSECT",VERTEX,{"disambiguationData":[OD(0.0)],"derivedFrom":[subQ1,subQ0]});Q188=makeQuery(id+"F0.imprint","IMPRINT",FACE,{"disambiguationData":[TD([[makeQuery(id+"F0.imprint","IMPRINT",EDGE,{"disambiguationData":[TD([[subQ2,-1.0]])],"derivedFrom":subQ1}),-1.0]])]});}
            var Q189;
            {var subQ1=sQuery(id+"F0.wireOp",EDGE,"E1.2.5.0");var subQ3=sQuery(id+"F0.wireOp",EDGE,"E3.29.1.0");var subQ4=makeQuery(id+"F0.imprint","INTERSECT",VERTEX,{"derivedFrom":[subQ1,subQ3]});Q189=makeQuery(id+"F0.imprint","IMPRINT",FACE,{"disambiguationData":[TD([[makeQuery(id+"F0.imprint","IMPRINT",EDGE,{"disambiguationData":[TD([[subQ4,-1.0]])],"derivedFrom":subQ3}),1.0]])]});}
            var Q190;
            {var subQ1=sQuery(id+"F0.wireOp",EDGE,"E1.1.2.0");var subQ3=sQuery(id+"F0.wireOp",EDGE,"E3.29.0.0");var subQ4=makeQuery(id+"F0.imprint","INTERSECT",VERTEX,{"derivedFrom":[subQ1,subQ3]});Q190=makeQuery(id+"F0.imprint","IMPRINT",FACE,{"disambiguationData":[TD([[makeQuery(id+"F0.imprint","IMPRINT",EDGE,{"disambiguationData":[TD([[subQ4,1.0]])],"derivedFrom":subQ3}),1.0]])]});}
            var Q191;
            {var subQ0=sQuery(id+"F0.wireOp",EDGE,"E3.30.0.0");var subQ1=sQuery(id+"F0.wireOp",EDGE,"E1.2.2.0");var subQ2=makeQuery(id+"F0.imprint","INTERSECT",VERTEX,{"disambiguationData":[OD(0.0)],"derivedFrom":[subQ1,subQ0]});Q191=makeQuery(id+"F0.imprint","IMPRINT",FACE,{"disambiguationData":[TD([[makeQuery(id+"F0.imprint","IMPRINT",EDGE,{"disambiguationData":[TD([[subQ2,-1.0]])],"derivedFrom":subQ1}),1.0]])]});}
            var Q192;
            {var subQ1=sQuery(id+"F0.wireOp",EDGE,"E1.1.5.0");var subQ3=sQuery(id+"F0.wireOp",EDGE,"E3.29.1.0");var subQ4=makeQuery(id+"F0.imprint","INTERSECT",VERTEX,{"derivedFrom":[subQ1,subQ3]});Q192=makeQuery(id+"F0.imprint","IMPRINT",FACE,{"disambiguationData":[TD([[makeQuery(id+"F0.imprint","IMPRINT",EDGE,{"disambiguationData":[TD([[subQ4,-1.0]])],"derivedFrom":subQ3}),1.0]])]});}
            var Q193;
            {var subQ0=sQuery(id+"F0.wireOp",EDGE,"E3.30.1.0");var subQ1=sQuery(id+"F0.wireOp",EDGE,"E1.2.5.0");var subQ2=makeQuery(id+"F0.imprint","INTERSECT",VERTEX,{"disambiguationData":[OD(0.0)],"derivedFrom":[subQ1,subQ0]});Q193=makeQuery(id+"F0.imprint","IMPRINT",FACE,{"disambiguationData":[TD([[makeQuery(id+"F0.imprint","IMPRINT",EDGE,{"disambiguationData":[TD([[subQ2,-1.0]])],"derivedFrom":subQ1}),1.0]])]});}
            var Q194;
            {var subQ0=sQuery(id+"F0.wireOp",EDGE,"E3.30.0.0");var subQ1=sQuery(id+"F0.wireOp",EDGE,"E1.2.2.0");var subQ2=makeQuery(id+"F0.imprint","INTERSECT",VERTEX,{"disambiguationData":[OD(0.0)],"derivedFrom":[subQ1,subQ0]});Q194=makeQuery(id+"F0.imprint","IMPRINT",FACE,{"disambiguationData":[TD([[makeQuery(id+"F0.imprint","IMPRINT",EDGE,{"disambiguationData":[TD([[subQ2,-1.0]])],"derivedFrom":subQ1}),-1.0]])]});}
            var Q195;
            {var subQ0=sQuery(id+"F0.wireOp",EDGE,"E3.28.0.0");var subQ1=sQuery(id+"F0.wireOp",EDGE,"E1.1.2.0");var subQ2=makeQuery(id+"F0.imprint","INTERSECT",VERTEX,{"disambiguationData":[OD(0.0)],"derivedFrom":[subQ1,subQ0]});Q195=makeQuery(id+"F0.imprint","IMPRINT",FACE,{"disambiguationData":[TD([[makeQuery(id+"F0.imprint","IMPRINT",EDGE,{"disambiguationData":[TD([[subQ2,-1.0]])],"derivedFrom":subQ1}),1.0]])]});}
            var Q196;
            {var subQ0=sQuery(id+"F0.wireOp",EDGE,"E3.30.1.0");var subQ1=sQuery(id+"F0.wireOp",EDGE,"E1.2.5.0");var subQ2=makeQuery(id+"F0.imprint","INTERSECT",VERTEX,{"disambiguationData":[OD(0.0)],"derivedFrom":[subQ1,subQ0]});Q196=makeQuery(id+"F0.imprint","IMPRINT",FACE,{"disambiguationData":[TD([[makeQuery(id+"F0.imprint","IMPRINT",EDGE,{"disambiguationData":[TD([[subQ2,-1.0]])],"derivedFrom":subQ1}),-1.0]])]});}
            var Q197;
            {var subQ1=sQuery(id+"F0.wireOp",EDGE,"E1.1.5.0");var subQ3=sQuery(id+"F0.wireOp",EDGE,"E3.29.1.0");var subQ4=makeQuery(id+"F0.imprint","INTERSECT",VERTEX,{"derivedFrom":[subQ1,subQ3]});Q197=makeQuery(id+"F0.imprint","IMPRINT",FACE,{"disambiguationData":[TD([[makeQuery(id+"F0.imprint","IMPRINT",EDGE,{"disambiguationData":[TD([[subQ4,1.0]])],"derivedFrom":subQ3}),1.0]])]});}
            var Q198;
            {var subQ0=sQuery(id+"F0.wireOp",EDGE,"E3.28.0.0");var subQ1=sQuery(id+"F0.wireOp",EDGE,"E1.1.2.0");var subQ2=makeQuery(id+"F0.imprint","INTERSECT",VERTEX,{"disambiguationData":[OD(0.0)],"derivedFrom":[subQ1,subQ0]});Q198=makeQuery(id+"F0.imprint","IMPRINT",FACE,{"disambiguationData":[TD([[makeQuery(id+"F0.imprint","IMPRINT",EDGE,{"disambiguationData":[TD([[subQ2,-1.0]])],"derivedFrom":subQ1}),-1.0]])]});}
            var Q199;
            {var subQ0=sQuery(id+"F0.wireOp",EDGE,"E3.28.1.0");var subQ1=sQuery(id+"F0.wireOp",EDGE,"E1.1.5.0");var subQ2=makeQuery(id+"F0.imprint","INTERSECT",VERTEX,{"disambiguationData":[OD(0.0)],"derivedFrom":[subQ1,subQ0]});Q199=makeQuery(id+"F0.imprint","IMPRINT",FACE,{"disambiguationData":[TD([[makeQuery(id+"F0.imprint","IMPRINT",EDGE,{"disambiguationData":[TD([[subQ2,-1.0]])],"derivedFrom":subQ1}),1.0]])]});}
            var Q200;
            {var subQ0=sQuery(id+"F0.wireOp",EDGE,"E3.28.1.0");var subQ1=sQuery(id+"F0.wireOp",EDGE,"E1.1.5.0");var subQ2=makeQuery(id+"F0.imprint","INTERSECT",VERTEX,{"disambiguationData":[OD(0.0)],"derivedFrom":[subQ1,subQ0]});Q200=makeQuery(id+"F0.imprint","IMPRINT",FACE,{"disambiguationData":[TD([[makeQuery(id+"F0.imprint","IMPRINT",EDGE,{"disambiguationData":[TD([[subQ2,-1.0]])],"derivedFrom":subQ1}),-1.0]])]});}
            extrude(context, id + "F1", {"entities" : qUnion([Q0, Q1, Q2, Q3, Q4, Q5, Q6, Q7, Q8, Q9, Q10, Q11, Q12, Q13, Q14, Q15, Q16, Q17, Q18, Q19, Q20, Q21, Q22, Q23, Q24, Q25, Q26, Q27, Q28, Q29, Q30, Q31, Q32, Q33, Q34, Q35, Q36, Q37, Q38, Q39, Q40, Q41, Q42, Q43, Q44, Q45, Q46, Q47, Q48, Q49, Q50, Q51, Q52, Q53, Q54, Q55, Q56, Q57, Q58, Q59, Q60, Q61, Q62, Q63, Q64, Q65, Q66, Q67, Q68, Q69, Q70, Q71, Q72, Q73, Q74, Q75, Q76, Q77, Q78, Q79, Q80, Q81, Q82, Q83, Q84, Q85, Q86, Q87, Q88, Q89, Q90, Q91, Q92, Q93, Q94, Q95, Q96, Q97, Q98, Q99, Q100, Q101, Q102, Q103, Q104, Q105, Q106, Q107, Q108, Q109, Q110, Q111, Q112, Q113, Q114, Q115, Q116, Q117, Q118, Q119, Q120, Q121, Q122, Q123, Q124, Q125, Q126, Q127, Q128, Q129, Q130, Q131, Q132, Q133, Q134, Q135, Q136, Q137, Q138, Q139, Q140, Q141, Q142, Q143, Q144, Q145, Q146, Q147, Q148, Q149, Q150, Q151, Q152, Q153, Q154, Q155, Q156, Q157, Q158, Q159, Q160, Q161, Q162, Q163, Q164, Q165, Q166, Q167, Q168, Q169, Q170, Q171, Q172, Q173, Q174, Q175, Q176, Q177, Q178, Q179, Q180, Q181, Q182, Q183, Q184, Q185, Q186, Q187, Q188, Q189, Q190, Q191, Q192, Q193, Q194, Q195, Q196, Q197, Q198, Q199, Q200]), "depth" : -25.4 * mm, "offsetDistance" : 25.4 * mm});
        }
        {
            var Q0;
            {var subQ0=sQuery(id+"F0.wireOp",EDGE,"E3.37.0.0");var subQ1=sQuery(id+"F0.wireOp",EDGE,"E1.2.2.0");var subQ2=makeQuery(id+"F0.imprint","INTERSECT",VERTEX,{"disambiguationData":[OD(0.0)],"derivedFrom":[subQ1,subQ0]});Q0=makeQuery(id+"F0.imprint","IMPRINT",FACE,{"disambiguationData":[TD([[makeQuery(id+"F0.imprint","IMPRINT",EDGE,{"disambiguationData":[TD([[subQ2,-1.0]])],"derivedFrom":subQ1}),-1.0]])]});}
            var Q1;
            {var subQ0=sQuery(id+"F0.wireOp",EDGE,"E3.19.0.0");var subQ1=sQuery(id+"F0.wireOp",EDGE,"E1.1.2.0");var subQ2=makeQuery(id+"F0.imprint","INTERSECT",VERTEX,{"disambiguationData":[OD(0.0)],"derivedFrom":[subQ1,subQ0]});Q1=makeQuery(id+"F0.imprint","IMPRINT",FACE,{"disambiguationData":[TD([[makeQuery(id+"F0.imprint","IMPRINT",EDGE,{"disambiguationData":[TD([[subQ2,-1.0]])],"derivedFrom":subQ1}),1.0]])]});}
            var Q2;
            {var subQ0=sQuery(id+"F0.wireOp",EDGE,"E3.3.0.0");var subQ1=sQuery(id+"F0.wireOp",EDGE,"E1.0.2.0");var subQ2=makeQuery(id+"F0.imprint","INTERSECT",VERTEX,{"disambiguationData":[OD(0.0)],"derivedFrom":[subQ1,subQ0]});Q2=makeQuery(id+"F0.imprint","IMPRINT",FACE,{"disambiguationData":[TD([[makeQuery(id+"F0.imprint","IMPRINT",EDGE,{"disambiguationData":[TD([[subQ2,-1.0]])],"derivedFrom":subQ1}),-1.0]])]});}
            var Q3;
            {var subQ0=sQuery(id+"F0.wireOp",EDGE,"E3.27.0.0");var subQ1=sQuery(id+"F0.wireOp",EDGE,"E1.1.2.0");var subQ2=makeQuery(id+"F0.imprint","INTERSECT",VERTEX,{"disambiguationData":[OD(0.0)],"derivedFrom":[subQ1,subQ0]});Q3=makeQuery(id+"F0.imprint","IMPRINT",FACE,{"disambiguationData":[TD([[makeQuery(id+"F0.imprint","IMPRINT",EDGE,{"disambiguationData":[TD([[subQ2,-1.0]])],"derivedFrom":subQ1}),1.0]])]});}
            var Q4;
            {var subQ0=sQuery(id+"F0.wireOp",EDGE,"E3.34.0.0");var subQ1=sQuery(id+"F0.wireOp",EDGE,"E1.2.2.0");var subQ2=makeQuery(id+"F0.imprint","INTERSECT",VERTEX,{"disambiguationData":[OD(0.0)],"derivedFrom":[subQ1,subQ0]});Q4=makeQuery(id+"F0.imprint","IMPRINT",FACE,{"disambiguationData":[TD([[makeQuery(id+"F0.imprint","IMPRINT",EDGE,{"disambiguationData":[TD([[subQ2,-1.0]])],"derivedFrom":subQ1}),1.0]])]});}
            var Q5;
            {var subQ0=sQuery(id+"F0.wireOp",EDGE,"E3.4.0.0");var subQ1=sQuery(id+"F0.wireOp",EDGE,"E1.0.2.0");var subQ2=makeQuery(id+"F0.imprint","INTERSECT",VERTEX,{"disambiguationData":[OD(0.0)],"derivedFrom":[subQ1,subQ0]});Q5=makeQuery(id+"F0.imprint","IMPRINT",FACE,{"disambiguationData":[TD([[makeQuery(id+"F0.imprint","IMPRINT",EDGE,{"disambiguationData":[TD([[subQ2,-1.0]])],"derivedFrom":subQ1}),-1.0]])]});}
            var Q6;
            {var subQ0=sQuery(id+"F0.wireOp",EDGE,"E3.6.0.0");var subQ1=sQuery(id+"F0.wireOp",EDGE,"E1.0.2.0");var subQ2=makeQuery(id+"F0.imprint","INTERSECT",VERTEX,{"disambiguationData":[OD(0.0)],"derivedFrom":[subQ1,subQ0]});Q6=makeQuery(id+"F0.imprint","IMPRINT",FACE,{"disambiguationData":[TD([[makeQuery(id+"F0.imprint","IMPRINT",EDGE,{"disambiguationData":[TD([[subQ2,-1.0]])],"derivedFrom":subQ1}),-1.0]])]});}
            var Q7;
            {var subQ0=sQuery(id+"F0.wireOp",EDGE,"E3.25.0.0");var subQ1=sQuery(id+"F0.wireOp",EDGE,"E1.1.2.0");var subQ2=makeQuery(id+"F0.imprint","INTERSECT",VERTEX,{"disambiguationData":[OD(0.0)],"derivedFrom":[subQ1,subQ0]});Q7=makeQuery(id+"F0.imprint","IMPRINT",FACE,{"disambiguationData":[TD([[makeQuery(id+"F0.imprint","IMPRINT",EDGE,{"disambiguationData":[TD([[subQ2,-1.0]])],"derivedFrom":subQ1}),-1.0]])]});}
            var Q8;
            {var subQ0=sQuery(id+"F0.wireOp",EDGE,"E3.17.0.0");var subQ1=sQuery(id+"F0.wireOp",EDGE,"E1.1.2.0");var subQ2=makeQuery(id+"F0.imprint","INTERSECT",VERTEX,{"disambiguationData":[OD(0.0)],"derivedFrom":[subQ1,subQ0]});Q8=makeQuery(id+"F0.imprint","IMPRINT",FACE,{"disambiguationData":[TD([[makeQuery(id+"F0.imprint","IMPRINT",EDGE,{"disambiguationData":[TD([[subQ2,-1.0]])],"derivedFrom":subQ1}),-1.0]])]});}
            var Q9;
            {var subQ0=sQuery(id+"F0.wireOp",EDGE,"E3.11.0.0");var subQ1=sQuery(id+"F0.wireOp",EDGE,"E1.0.2.0");var subQ2=makeQuery(id+"F0.imprint","INTERSECT",VERTEX,{"disambiguationData":[OD(0.0)],"derivedFrom":[subQ1,subQ0]});Q9=makeQuery(id+"F0.imprint","IMPRINT",FACE,{"disambiguationData":[TD([[makeQuery(id+"F0.imprint","IMPRINT",EDGE,{"disambiguationData":[TD([[subQ2,-1.0]])],"derivedFrom":subQ1}),-1.0]])]});}
            var Q10;
            {var subQ0=sQuery(id+"F0.wireOp",EDGE,"E3.30.0.0");var subQ1=sQuery(id+"F0.wireOp",EDGE,"E1.2.2.0");var subQ2=makeQuery(id+"F0.imprint","INTERSECT",VERTEX,{"disambiguationData":[OD(0.0)],"derivedFrom":[subQ1,subQ0]});Q10=makeQuery(id+"F0.imprint","IMPRINT",FACE,{"disambiguationData":[TD([[makeQuery(id+"F0.imprint","IMPRINT",EDGE,{"disambiguationData":[TD([[subQ2,-1.0]])],"derivedFrom":subQ1}),-1.0]])]});}
            var Q11;
            {var subQ0=sQuery(id+"F0.wireOp",EDGE,"E3.28.0.0");var subQ1=sQuery(id+"F0.wireOp",EDGE,"E1.1.2.0");var subQ2=makeQuery(id+"F0.imprint","INTERSECT",VERTEX,{"disambiguationData":[OD(0.0)],"derivedFrom":[subQ1,subQ0]});Q11=makeQuery(id+"F0.imprint","IMPRINT",FACE,{"disambiguationData":[TD([[makeQuery(id+"F0.imprint","IMPRINT",EDGE,{"disambiguationData":[TD([[subQ2,-1.0]])],"derivedFrom":subQ1}),1.0]])]});}
            var Q12;
            {var subQ0=sQuery(id+"F0.wireOp",EDGE,"E3.36.0.0");var subQ1=sQuery(id+"F0.wireOp",EDGE,"E1.2.2.0");var subQ2=makeQuery(id+"F0.imprint","INTERSECT",VERTEX,{"disambiguationData":[OD(0.0)],"derivedFrom":[subQ1,subQ0]});Q12=makeQuery(id+"F0.imprint","IMPRINT",FACE,{"disambiguationData":[TD([[makeQuery(id+"F0.imprint","IMPRINT",EDGE,{"disambiguationData":[TD([[subQ2,-1.0]])],"derivedFrom":subQ1}),1.0]])]});}
            var Q13;
            {var subQ0=sQuery(id+"F0.wireOp",EDGE,"E3.6.0.0");var subQ1=sQuery(id+"F0.wireOp",EDGE,"E1.0.2.0");var subQ2=makeQuery(id+"F0.imprint","INTERSECT",VERTEX,{"disambiguationData":[OD(0.0)],"derivedFrom":[subQ1,subQ0]});Q13=makeQuery(id+"F0.imprint","IMPRINT",FACE,{"disambiguationData":[TD([[makeQuery(id+"F0.imprint","IMPRINT",EDGE,{"disambiguationData":[TD([[subQ2,-1.0]])],"derivedFrom":subQ1}),1.0]])]});}
            var Q14;
            {var subQ0=sQuery(id+"F0.wireOp",EDGE,"E3.10.0.0");var subQ1=sQuery(id+"F0.wireOp",EDGE,"E1.0.2.0");var subQ2=makeQuery(id+"F0.imprint","INTERSECT",VERTEX,{"disambiguationData":[OD(0.0)],"derivedFrom":[subQ1,subQ0]});Q14=makeQuery(id+"F0.imprint","IMPRINT",FACE,{"disambiguationData":[TD([[makeQuery(id+"F0.imprint","IMPRINT",EDGE,{"disambiguationData":[TD([[subQ2,-1.0]])],"derivedFrom":subQ1}),1.0]])]});}
            var Q15;
            {var subQ0=sQuery(id+"F0.wireOp",EDGE,"E3.37.0.0");var subQ1=sQuery(id+"F0.wireOp",EDGE,"E1.2.2.0");var subQ2=makeQuery(id+"F0.imprint","INTERSECT",VERTEX,{"disambiguationData":[OD(0.0)],"derivedFrom":[subQ1,subQ0]});Q15=makeQuery(id+"F0.imprint","IMPRINT",FACE,{"disambiguationData":[TD([[makeQuery(id+"F0.imprint","IMPRINT",EDGE,{"disambiguationData":[TD([[subQ2,-1.0]])],"derivedFrom":subQ1}),1.0]])]});}
            var Q16;
            {var subQ0=sQuery(id+"F0.wireOp",EDGE,"E3.1.0.0");var subQ1=sQuery(id+"F0.wireOp",EDGE,"E1.0.2.0");var subQ2=makeQuery(id+"F0.imprint","INTERSECT",VERTEX,{"disambiguationData":[OD(0.0)],"derivedFrom":[subQ1,subQ0]});Q16=makeQuery(id+"F0.imprint","IMPRINT",FACE,{"disambiguationData":[TD([[makeQuery(id+"F0.imprint","IMPRINT",EDGE,{"disambiguationData":[TD([[subQ2,-1.0]])],"derivedFrom":subQ1}),1.0]])]});}
            var Q17;
            {var subQ0=sQuery(id+"F0.wireOp",EDGE,"E3.20.0.0");var subQ1=sQuery(id+"F0.wireOp",EDGE,"E1.1.2.0");var subQ2=makeQuery(id+"F0.imprint","INTERSECT",VERTEX,{"disambiguationData":[OD(0.0)],"derivedFrom":[subQ1,subQ0]});Q17=makeQuery(id+"F0.imprint","IMPRINT",FACE,{"disambiguationData":[TD([[makeQuery(id+"F0.imprint","IMPRINT",EDGE,{"disambiguationData":[TD([[subQ2,-1.0]])],"derivedFrom":subQ1}),-1.0]])]});}
            var Q18;
            {var subQ1=sQuery(id+"F0.wireOp",EDGE,"E1.2.2.0");var subQ3=sQuery(id+"F0.wireOp",EDGE,"E3.29.0.0");var subQ4=makeQuery(id+"F0.imprint","INTERSECT",VERTEX,{"derivedFrom":[subQ1,subQ3]});Q18=makeQuery(id+"F0.imprint","IMPRINT",FACE,{"disambiguationData":[TD([[makeQuery(id+"F0.imprint","IMPRINT",EDGE,{"disambiguationData":[TD([[subQ4,-1.0]])],"derivedFrom":subQ3}),1.0]])]});}
            var Q19;
            {var subQ0=sQuery(id+"F0.wireOp",EDGE,"E3.26.0.0");var subQ1=sQuery(id+"F0.wireOp",EDGE,"E1.1.2.0");var subQ2=makeQuery(id+"F0.imprint","INTERSECT",VERTEX,{"disambiguationData":[OD(0.0)],"derivedFrom":[subQ1,subQ0]});Q19=makeQuery(id+"F0.imprint","IMPRINT",FACE,{"disambiguationData":[TD([[makeQuery(id+"F0.imprint","IMPRINT",EDGE,{"disambiguationData":[TD([[subQ2,-1.0]])],"derivedFrom":subQ1}),-1.0]])]});}
            var Q20;
            {var subQ0=sQuery(id+"F0.wireOp",EDGE,"E3.18.0.0");var subQ1=sQuery(id+"F0.wireOp",EDGE,"E1.1.2.0");var subQ2=makeQuery(id+"F0.imprint","INTERSECT",VERTEX,{"disambiguationData":[OD(0.0)],"derivedFrom":[subQ1,subQ0]});Q20=makeQuery(id+"F0.imprint","IMPRINT",FACE,{"disambiguationData":[TD([[makeQuery(id+"F0.imprint","IMPRINT",EDGE,{"disambiguationData":[TD([[subQ2,-1.0]])],"derivedFrom":subQ1}),-1.0]])]});}
            var Q21;
            {var subQ0=sQuery(id+"F0.wireOp",EDGE,"E3.26.0.0");var subQ1=sQuery(id+"F0.wireOp",EDGE,"E1.1.2.0");var subQ2=makeQuery(id+"F0.imprint","INTERSECT",VERTEX,{"disambiguationData":[OD(0.0)],"derivedFrom":[subQ1,subQ0]});Q21=makeQuery(id+"F0.imprint","IMPRINT",FACE,{"disambiguationData":[TD([[makeQuery(id+"F0.imprint","IMPRINT",EDGE,{"disambiguationData":[TD([[subQ2,-1.0]])],"derivedFrom":subQ1}),1.0]])]});}
            var Q22;
            {var subQ0=sQuery(id+"F0.wireOp",EDGE,"E3.9.0.0");var subQ1=sQuery(id+"F0.wireOp",EDGE,"E1.0.2.0");var subQ2=makeQuery(id+"F0.imprint","INTERSECT",VERTEX,{"disambiguationData":[OD(0.0)],"derivedFrom":[subQ1,subQ0]});Q22=makeQuery(id+"F0.imprint","IMPRINT",FACE,{"disambiguationData":[TD([[makeQuery(id+"F0.imprint","IMPRINT",EDGE,{"disambiguationData":[TD([[subQ2,-1.0]])],"derivedFrom":subQ1}),-1.0]])]});}
            var Q23;
            {var subQ0=sQuery(id+"F0.wireOp",EDGE,"E3.38.0.0");var subQ1=sQuery(id+"F0.wireOp",EDGE,"E1.2.2.0");var subQ2=makeQuery(id+"F0.imprint","INTERSECT",VERTEX,{"disambiguationData":[OD(0.0)],"derivedFrom":[subQ1,subQ0]});Q23=makeQuery(id+"F0.imprint","IMPRINT",FACE,{"disambiguationData":[TD([[makeQuery(id+"F0.imprint","IMPRINT",EDGE,{"disambiguationData":[TD([[subQ2,-1.0]])],"derivedFrom":subQ1}),-1.0]])]});}
            var Q24;
            {var subQ0=sQuery(id+"F0.wireOp",EDGE,"E3.9.0.0");var subQ1=sQuery(id+"F0.wireOp",EDGE,"E1.0.2.0");var subQ2=makeQuery(id+"F0.imprint","INTERSECT",VERTEX,{"disambiguationData":[OD(0.0)],"derivedFrom":[subQ1,subQ0]});Q24=makeQuery(id+"F0.imprint","IMPRINT",FACE,{"disambiguationData":[TD([[makeQuery(id+"F0.imprint","IMPRINT",EDGE,{"disambiguationData":[TD([[subQ2,-1.0]])],"derivedFrom":subQ1}),1.0]])]});}
            var Q25;
            {var subQ0=sQuery(id+"F0.wireOp",EDGE,"E3.10.0.0");var subQ1=sQuery(id+"F0.wireOp",EDGE,"E1.0.2.0");var subQ2=makeQuery(id+"F0.imprint","INTERSECT",VERTEX,{"disambiguationData":[OD(0.0)],"derivedFrom":[subQ1,subQ0]});Q25=makeQuery(id+"F0.imprint","IMPRINT",FACE,{"disambiguationData":[TD([[makeQuery(id+"F0.imprint","IMPRINT",EDGE,{"disambiguationData":[TD([[subQ2,-1.0]])],"derivedFrom":subQ1}),-1.0]])]});}
            var Q26;
            {var subQ0=sQuery(id+"F0.wireOp",EDGE,"E3.7.0.0");var subQ1=sQuery(id+"F0.wireOp",EDGE,"E1.0.2.0");var subQ2=makeQuery(id+"F0.imprint","INTERSECT",VERTEX,{"disambiguationData":[OD(0.0)],"derivedFrom":[subQ1,subQ0]});Q26=makeQuery(id+"F0.imprint","IMPRINT",FACE,{"disambiguationData":[TD([[makeQuery(id+"F0.imprint","IMPRINT",EDGE,{"disambiguationData":[TD([[subQ2,-1.0]])],"derivedFrom":subQ1}),1.0]])]});}
            var Q27;
            {var subQ0=sQuery(id+"F0.wireOp",EDGE,"E3.20.0.0");var subQ1=sQuery(id+"F0.wireOp",EDGE,"E1.1.2.0");var subQ2=makeQuery(id+"F0.imprint","INTERSECT",VERTEX,{"disambiguationData":[OD(0.0)],"derivedFrom":[subQ1,subQ0]});Q27=makeQuery(id+"F0.imprint","IMPRINT",FACE,{"disambiguationData":[TD([[makeQuery(id+"F0.imprint","IMPRINT",EDGE,{"disambiguationData":[TD([[subQ2,-1.0]])],"derivedFrom":subQ1}),1.0]])]});}
            var Q28;
            {var subQ0=sQuery(id+"F0.wireOp",EDGE,"E3.42.0.0");var subQ1=sQuery(id+"F0.wireOp",EDGE,"E1.2.2.0");var subQ2=makeQuery(id+"F0.imprint","INTERSECT",VERTEX,{"disambiguationData":[OD(0.0)],"derivedFrom":[subQ1,subQ0]});Q28=makeQuery(id+"F0.imprint","IMPRINT",FACE,{"disambiguationData":[TD([[makeQuery(id+"F0.imprint","IMPRINT",EDGE,{"disambiguationData":[TD([[subQ2,-1.0]])],"derivedFrom":subQ1}),1.0]])]});}
            var Q29;
            {var subQ0=sQuery(id+"F0.wireOp",EDGE,"E3.18.0.0");var subQ1=sQuery(id+"F0.wireOp",EDGE,"E1.1.2.0");var subQ2=makeQuery(id+"F0.imprint","INTERSECT",VERTEX,{"disambiguationData":[OD(0.0)],"derivedFrom":[subQ1,subQ0]});Q29=makeQuery(id+"F0.imprint","IMPRINT",FACE,{"disambiguationData":[TD([[makeQuery(id+"F0.imprint","IMPRINT",EDGE,{"disambiguationData":[TD([[subQ2,-1.0]])],"derivedFrom":subQ1}),1.0]])]});}
            var Q30;
            {var subQ0=sQuery(id+"F0.wireOp",EDGE,"E3.39.0.0");var subQ1=sQuery(id+"F0.wireOp",EDGE,"E1.2.2.0");var subQ2=makeQuery(id+"F0.imprint","INTERSECT",VERTEX,{"disambiguationData":[OD(0.0)],"derivedFrom":[subQ1,subQ0]});Q30=makeQuery(id+"F0.imprint","IMPRINT",FACE,{"disambiguationData":[TD([[makeQuery(id+"F0.imprint","IMPRINT",EDGE,{"disambiguationData":[TD([[subQ2,-1.0]])],"derivedFrom":subQ1}),1.0]])]});}
            var Q31;
            {var subQ0=sQuery(id+"F0.wireOp",EDGE,"E3.11.0.0");var subQ1=sQuery(id+"F0.wireOp",EDGE,"E1.0.2.0");var subQ2=makeQuery(id+"F0.imprint","INTERSECT",VERTEX,{"disambiguationData":[OD(0.0)],"derivedFrom":[subQ1,subQ0]});Q31=makeQuery(id+"F0.imprint","IMPRINT",FACE,{"disambiguationData":[TD([[makeQuery(id+"F0.imprint","IMPRINT",EDGE,{"disambiguationData":[TD([[subQ2,-1.0]])],"derivedFrom":subQ1}),1.0]])]});}
            var Q32;
            {var subQ0=sQuery(id+"F0.wireOp",EDGE,"E3.30.0.0");var subQ1=sQuery(id+"F0.wireOp",EDGE,"E1.2.2.0");var subQ2=makeQuery(id+"F0.imprint","INTERSECT",VERTEX,{"disambiguationData":[OD(0.0)],"derivedFrom":[subQ1,subQ0]});Q32=makeQuery(id+"F0.imprint","IMPRINT",FACE,{"disambiguationData":[TD([[makeQuery(id+"F0.imprint","IMPRINT",EDGE,{"disambiguationData":[TD([[subQ2,-1.0]])],"derivedFrom":subQ1}),1.0]])]});}
            var Q33;
            {var subQ0=sQuery(id+"F0.wireOp",EDGE,"E3.27.0.0");var subQ1=sQuery(id+"F0.wireOp",EDGE,"E1.1.2.0");var subQ2=makeQuery(id+"F0.imprint","INTERSECT",VERTEX,{"disambiguationData":[OD(0.0)],"derivedFrom":[subQ1,subQ0]});Q33=makeQuery(id+"F0.imprint","IMPRINT",FACE,{"disambiguationData":[TD([[makeQuery(id+"F0.imprint","IMPRINT",EDGE,{"disambiguationData":[TD([[subQ2,-1.0]])],"derivedFrom":subQ1}),-1.0]])]});}
            var Q34;
            {var subQ0=sQuery(id+"F0.wireOp",EDGE,"E3.36.0.0");var subQ1=sQuery(id+"F0.wireOp",EDGE,"E1.2.2.0");var subQ2=makeQuery(id+"F0.imprint","INTERSECT",VERTEX,{"disambiguationData":[OD(0.0)],"derivedFrom":[subQ1,subQ0]});Q34=makeQuery(id+"F0.imprint","IMPRINT",FACE,{"disambiguationData":[TD([[makeQuery(id+"F0.imprint","IMPRINT",EDGE,{"disambiguationData":[TD([[subQ2,-1.0]])],"derivedFrom":subQ1}),-1.0]])]});}
            var Q35;
            {var subQ0=sQuery(id+"F0.wireOp",EDGE,"E3.19.0.0");var subQ1=sQuery(id+"F0.wireOp",EDGE,"E1.1.2.0");var subQ2=makeQuery(id+"F0.imprint","INTERSECT",VERTEX,{"disambiguationData":[OD(0.0)],"derivedFrom":[subQ1,subQ0]});Q35=makeQuery(id+"F0.imprint","IMPRINT",FACE,{"disambiguationData":[TD([[makeQuery(id+"F0.imprint","IMPRINT",EDGE,{"disambiguationData":[TD([[subQ2,-1.0]])],"derivedFrom":subQ1}),-1.0]])]});}
            var Q36;
            {var subQ0=sQuery(id+"F0.wireOp",EDGE,"E3.12.0.0");var subQ1=sQuery(id+"F0.wireOp",EDGE,"E1.0.2.0");var subQ2=makeQuery(id+"F0.imprint","INTERSECT",VERTEX,{"disambiguationData":[OD(0.0)],"derivedFrom":[subQ1,subQ0]});Q36=makeQuery(id+"F0.imprint","IMPRINT",FACE,{"disambiguationData":[TD([[makeQuery(id+"F0.imprint","IMPRINT",EDGE,{"disambiguationData":[TD([[subQ2,-1.0]])],"derivedFrom":subQ1}),1.0]])]});}
            var Q37;
            {var subQ0=sQuery(id+"F0.wireOp",EDGE,"E3.2.0.0");var subQ1=sQuery(id+"F0.wireOp",EDGE,"E1.0.2.0");var subQ2=makeQuery(id+"F0.imprint","INTERSECT",VERTEX,{"disambiguationData":[OD(0.0)],"derivedFrom":[subQ1,subQ0]});Q37=makeQuery(id+"F0.imprint","IMPRINT",FACE,{"disambiguationData":[TD([[makeQuery(id+"F0.imprint","IMPRINT",EDGE,{"disambiguationData":[TD([[subQ2,-1.0]])],"derivedFrom":subQ1}),1.0]])]});}
            var Q38;
            {var subQ1=sQuery(id+"F0.wireOp",EDGE,"E1.2.1.1");var subQ3=sQuery(id+"F0.wireOp",EDGE,"E3.29.0.0");var subQ4=makeQuery(id+"F0.imprint","INTERSECT",VERTEX,{"derivedFrom":[subQ1,subQ3]});Q38=makeQuery(id+"F0.imprint","IMPRINT",FACE,{"disambiguationData":[TD([[makeQuery(id+"F0.imprint","IMPRINT",EDGE,{"disambiguationData":[TD([[subQ4,-1.0]])],"derivedFrom":subQ3}),1.0]])]});}
            var Q39;
            {var subQ0=sQuery(id+"F0.wireOp",EDGE,"E3.38.0.0");var subQ1=sQuery(id+"F0.wireOp",EDGE,"E1.2.2.0");var subQ2=makeQuery(id+"F0.imprint","INTERSECT",VERTEX,{"disambiguationData":[OD(0.0)],"derivedFrom":[subQ1,subQ0]});Q39=makeQuery(id+"F0.imprint","IMPRINT",FACE,{"disambiguationData":[TD([[makeQuery(id+"F0.imprint","IMPRINT",EDGE,{"disambiguationData":[TD([[subQ2,-1.0]])],"derivedFrom":subQ1}),1.0]])]});}
            var Q40;
            {var subQ0=sQuery(id+"F0.wireOp",EDGE,"E3.2.0.0");var subQ1=sQuery(id+"F0.wireOp",EDGE,"E1.0.2.0");var subQ2=makeQuery(id+"F0.imprint","INTERSECT",VERTEX,{"disambiguationData":[OD(0.0)],"derivedFrom":[subQ1,subQ0]});Q40=makeQuery(id+"F0.imprint","IMPRINT",FACE,{"disambiguationData":[TD([[makeQuery(id+"F0.imprint","IMPRINT",EDGE,{"disambiguationData":[TD([[subQ2,-1.0]])],"derivedFrom":subQ1}),-1.0]])]});}
            var Q41;
            {var subQ0=sQuery(id+"F0.wireOp",EDGE,"E3.3.0.0");var subQ1=sQuery(id+"F0.wireOp",EDGE,"E1.0.2.0");var subQ2=makeQuery(id+"F0.imprint","INTERSECT",VERTEX,{"disambiguationData":[OD(0.0)],"derivedFrom":[subQ1,subQ0]});Q41=makeQuery(id+"F0.imprint","IMPRINT",FACE,{"disambiguationData":[TD([[makeQuery(id+"F0.imprint","IMPRINT",EDGE,{"disambiguationData":[TD([[subQ2,-1.0]])],"derivedFrom":subQ1}),1.0]])]});}
            var Q42;
            {var subQ0=sQuery(id+"F0.wireOp",EDGE,"E3.4.0.0");var subQ1=sQuery(id+"F0.wireOp",EDGE,"E1.0.2.0");var subQ2=makeQuery(id+"F0.imprint","INTERSECT",VERTEX,{"disambiguationData":[OD(0.0)],"derivedFrom":[subQ1,subQ0]});Q42=makeQuery(id+"F0.imprint","IMPRINT",FACE,{"disambiguationData":[TD([[makeQuery(id+"F0.imprint","IMPRINT",EDGE,{"disambiguationData":[TD([[subQ2,-1.0]])],"derivedFrom":subQ1}),1.0]])]});}
            var Q43;
            {var subQ0=sQuery(id+"F0.wireOp",EDGE,"E3.5.0.0");var subQ1=sQuery(id+"F0.wireOp",EDGE,"E1.0.2.0");var subQ2=makeQuery(id+"F0.imprint","INTERSECT",VERTEX,{"disambiguationData":[OD(0.0)],"derivedFrom":[subQ1,subQ0]});Q43=makeQuery(id+"F0.imprint","IMPRINT",FACE,{"disambiguationData":[TD([[makeQuery(id+"F0.imprint","IMPRINT",EDGE,{"disambiguationData":[TD([[subQ2,-1.0]])],"derivedFrom":subQ1}),1.0]])]});}
            var Q44;
            {var subQ0=sQuery(id+"F0.wireOp",EDGE,"E3.5.0.0");var subQ1=sQuery(id+"F0.wireOp",EDGE,"E1.0.2.0");var subQ2=makeQuery(id+"F0.imprint","INTERSECT",VERTEX,{"disambiguationData":[OD(0.0)],"derivedFrom":[subQ1,subQ0]});Q44=makeQuery(id+"F0.imprint","IMPRINT",FACE,{"disambiguationData":[TD([[makeQuery(id+"F0.imprint","IMPRINT",EDGE,{"disambiguationData":[TD([[subQ2,-1.0]])],"derivedFrom":subQ1}),-1.0]])]});}
            var Q45;
            {var subQ0=sQuery(id+"F0.wireOp",EDGE,"E3.31.0.0");var subQ1=sQuery(id+"F0.wireOp",EDGE,"E1.2.2.0");var subQ2=makeQuery(id+"F0.imprint","INTERSECT",VERTEX,{"disambiguationData":[OD(0.0)],"derivedFrom":[subQ1,subQ0]});Q45=makeQuery(id+"F0.imprint","IMPRINT",FACE,{"disambiguationData":[TD([[makeQuery(id+"F0.imprint","IMPRINT",EDGE,{"disambiguationData":[TD([[subQ2,-1.0]])],"derivedFrom":subQ1}),1.0]])]});}
            var Q46;
            {var subQ0=sQuery(id+"F0.wireOp",EDGE,"E3.15.0.0");var subQ1=sQuery(id+"F0.wireOp",EDGE,"E1.1.2.0");var subQ2=makeQuery(id+"F0.imprint","INTERSECT",VERTEX,{"disambiguationData":[OD(0.0)],"derivedFrom":[subQ1,subQ0]});Q46=makeQuery(id+"F0.imprint","IMPRINT",FACE,{"disambiguationData":[TD([[makeQuery(id+"F0.imprint","IMPRINT",EDGE,{"disambiguationData":[TD([[subQ2,-1.0]])],"derivedFrom":subQ1}),-1.0]])]});}
            var Q47;
            {var subQ0=sQuery(id+"F0.wireOp",EDGE,"E3.23.0.0");var subQ1=sQuery(id+"F0.wireOp",EDGE,"E1.1.2.0");var subQ2=makeQuery(id+"F0.imprint","INTERSECT",VERTEX,{"disambiguationData":[OD(0.0)],"derivedFrom":[subQ1,subQ0]});Q47=makeQuery(id+"F0.imprint","IMPRINT",FACE,{"disambiguationData":[TD([[makeQuery(id+"F0.imprint","IMPRINT",EDGE,{"disambiguationData":[TD([[subQ2,-1.0]])],"derivedFrom":subQ1}),-1.0]])]});}
            var Q48;
            {var subQ0=sQuery(id+"F0.wireOp",EDGE,"E3.28.0.0");var subQ1=sQuery(id+"F0.wireOp",EDGE,"E1.1.2.0");var subQ2=makeQuery(id+"F0.imprint","INTERSECT",VERTEX,{"disambiguationData":[OD(0.0)],"derivedFrom":[subQ1,subQ0]});Q48=makeQuery(id+"F0.imprint","IMPRINT",FACE,{"disambiguationData":[TD([[makeQuery(id+"F0.imprint","IMPRINT",EDGE,{"disambiguationData":[TD([[subQ2,-1.0]])],"derivedFrom":subQ1}),-1.0]])]});}
            var Q49;
            {var subQ0=sQuery(id+"F0.wireOp",EDGE,"E3.35.0.0");var subQ1=sQuery(id+"F0.wireOp",EDGE,"E1.2.2.0");var subQ2=makeQuery(id+"F0.imprint","INTERSECT",VERTEX,{"disambiguationData":[OD(0.0)],"derivedFrom":[subQ1,subQ0]});Q49=makeQuery(id+"F0.imprint","IMPRINT",FACE,{"disambiguationData":[TD([[makeQuery(id+"F0.imprint","IMPRINT",EDGE,{"disambiguationData":[TD([[subQ2,-1.0]])],"derivedFrom":subQ1}),-1.0]])]});}
            var Q50;
            {var subQ0=sQuery(id+"F0.wireOp",EDGE,"E3.43.0.0");var subQ1=sQuery(id+"F0.wireOp",EDGE,"E1.2.2.0");var subQ2=makeQuery(id+"F0.imprint","INTERSECT",VERTEX,{"disambiguationData":[OD(0.0)],"derivedFrom":[subQ1,subQ0]});Q50=makeQuery(id+"F0.imprint","IMPRINT",FACE,{"disambiguationData":[TD([[makeQuery(id+"F0.imprint","IMPRINT",EDGE,{"disambiguationData":[TD([[subQ2,-1.0]])],"derivedFrom":subQ1}),-1.0]])]});}
            var Q51;
            {var subQ0=sQuery(id+"F0.wireOp",EDGE,"E3.17.0.0");var subQ1=sQuery(id+"F0.wireOp",EDGE,"E1.1.2.0");var subQ2=makeQuery(id+"F0.imprint","INTERSECT",VERTEX,{"disambiguationData":[OD(0.0)],"derivedFrom":[subQ1,subQ0]});Q51=makeQuery(id+"F0.imprint","IMPRINT",FACE,{"disambiguationData":[TD([[makeQuery(id+"F0.imprint","IMPRINT",EDGE,{"disambiguationData":[TD([[subQ2,-1.0]])],"derivedFrom":subQ1}),1.0]])]});}
            var Q52;
            {var subQ0=sQuery(id+"F0.wireOp",EDGE,"E3.25.0.0");var subQ1=sQuery(id+"F0.wireOp",EDGE,"E1.1.2.0");var subQ2=makeQuery(id+"F0.imprint","INTERSECT",VERTEX,{"disambiguationData":[OD(0.0)],"derivedFrom":[subQ1,subQ0]});Q52=makeQuery(id+"F0.imprint","IMPRINT",FACE,{"disambiguationData":[TD([[makeQuery(id+"F0.imprint","IMPRINT",EDGE,{"disambiguationData":[TD([[subQ2,-1.0]])],"derivedFrom":subQ1}),1.0]])]});}
            var Q53;
            {var subQ0=sQuery(id+"F0.wireOp",EDGE,"E3.8.0.0");var subQ1=sQuery(id+"F0.wireOp",EDGE,"E1.0.2.0");var subQ2=makeQuery(id+"F0.imprint","INTERSECT",VERTEX,{"disambiguationData":[OD(0.0)],"derivedFrom":[subQ1,subQ0]});Q53=makeQuery(id+"F0.imprint","IMPRINT",FACE,{"disambiguationData":[TD([[makeQuery(id+"F0.imprint","IMPRINT",EDGE,{"disambiguationData":[TD([[subQ2,-1.0]])],"derivedFrom":subQ1}),-1.0]])]});}
            var Q54;
            {var subQ0=sQuery(id+"F0.wireOp",EDGE,"E3.35.0.0");var subQ1=sQuery(id+"F0.wireOp",EDGE,"E1.2.2.0");var subQ2=makeQuery(id+"F0.imprint","INTERSECT",VERTEX,{"disambiguationData":[OD(0.0)],"derivedFrom":[subQ1,subQ0]});Q54=makeQuery(id+"F0.imprint","IMPRINT",FACE,{"disambiguationData":[TD([[makeQuery(id+"F0.imprint","IMPRINT",EDGE,{"disambiguationData":[TD([[subQ2,-1.0]])],"derivedFrom":subQ1}),1.0]])]});}
            var Q55;
            {var subQ0=sQuery(id+"F0.wireOp",EDGE,"E3.43.0.0");var subQ1=sQuery(id+"F0.wireOp",EDGE,"E1.2.2.0");var subQ2=makeQuery(id+"F0.imprint","INTERSECT",VERTEX,{"disambiguationData":[OD(0.0)],"derivedFrom":[subQ1,subQ0]});Q55=makeQuery(id+"F0.imprint","IMPRINT",FACE,{"disambiguationData":[TD([[makeQuery(id+"F0.imprint","IMPRINT",EDGE,{"disambiguationData":[TD([[subQ2,-1.0]])],"derivedFrom":subQ1}),1.0]])]});}
            var Q56;
            {var subQ0=sQuery(id+"F0.wireOp",EDGE,"E3.16.0.0");var subQ1=sQuery(id+"F0.wireOp",EDGE,"E1.1.2.0");var subQ2=makeQuery(id+"F0.imprint","INTERSECT",VERTEX,{"disambiguationData":[OD(0.0)],"derivedFrom":[subQ1,subQ0]});Q56=makeQuery(id+"F0.imprint","IMPRINT",FACE,{"disambiguationData":[TD([[makeQuery(id+"F0.imprint","IMPRINT",EDGE,{"disambiguationData":[TD([[subQ2,-1.0]])],"derivedFrom":subQ1}),-1.0]])]});}
            var Q57;
            {var subQ0=sQuery(id+"F0.wireOp",EDGE,"E3.24.0.0");var subQ1=sQuery(id+"F0.wireOp",EDGE,"E1.1.2.0");var subQ2=makeQuery(id+"F0.imprint","INTERSECT",VERTEX,{"disambiguationData":[OD(0.0)],"derivedFrom":[subQ1,subQ0]});Q57=makeQuery(id+"F0.imprint","IMPRINT",FACE,{"disambiguationData":[TD([[makeQuery(id+"F0.imprint","IMPRINT",EDGE,{"disambiguationData":[TD([[subQ2,-1.0]])],"derivedFrom":subQ1}),-1.0]])]});}
            var Q58;
            {var subQ0=sQuery(id+"F0.wireOp",EDGE,"E3.8.0.0");var subQ1=sQuery(id+"F0.wireOp",EDGE,"E1.0.2.0");var subQ2=makeQuery(id+"F0.imprint","INTERSECT",VERTEX,{"disambiguationData":[OD(0.0)],"derivedFrom":[subQ1,subQ0]});Q58=makeQuery(id+"F0.imprint","IMPRINT",FACE,{"disambiguationData":[TD([[makeQuery(id+"F0.imprint","IMPRINT",EDGE,{"disambiguationData":[TD([[subQ2,-1.0]])],"derivedFrom":subQ1}),1.0]])]});}
            var Q59;
            {var subQ0=sQuery(id+"F0.wireOp",EDGE,"E3.34.0.0");var subQ1=sQuery(id+"F0.wireOp",EDGE,"E1.2.2.0");var subQ2=makeQuery(id+"F0.imprint","INTERSECT",VERTEX,{"disambiguationData":[OD(0.0)],"derivedFrom":[subQ1,subQ0]});Q59=makeQuery(id+"F0.imprint","IMPRINT",FACE,{"disambiguationData":[TD([[makeQuery(id+"F0.imprint","IMPRINT",EDGE,{"disambiguationData":[TD([[subQ2,-1.0]])],"derivedFrom":subQ1}),-1.0]])]});}
            var Q60;
            {var subQ0=sQuery(id+"F0.wireOp",EDGE,"E3.42.0.0");var subQ1=sQuery(id+"F0.wireOp",EDGE,"E1.2.2.0");var subQ2=makeQuery(id+"F0.imprint","INTERSECT",VERTEX,{"disambiguationData":[OD(0.0)],"derivedFrom":[subQ1,subQ0]});Q60=makeQuery(id+"F0.imprint","IMPRINT",FACE,{"disambiguationData":[TD([[makeQuery(id+"F0.imprint","IMPRINT",EDGE,{"disambiguationData":[TD([[subQ2,-1.0]])],"derivedFrom":subQ1}),-1.0]])]});}
            var Q61;
            {var subQ0=sQuery(id+"F0.wireOp",EDGE,"E3.16.0.0");var subQ1=sQuery(id+"F0.wireOp",EDGE,"E1.1.2.0");var subQ2=makeQuery(id+"F0.imprint","INTERSECT",VERTEX,{"disambiguationData":[OD(0.0)],"derivedFrom":[subQ1,subQ0]});Q61=makeQuery(id+"F0.imprint","IMPRINT",FACE,{"disambiguationData":[TD([[makeQuery(id+"F0.imprint","IMPRINT",EDGE,{"disambiguationData":[TD([[subQ2,-1.0]])],"derivedFrom":subQ1}),1.0]])]});}
            var Q62;
            {var subQ0=sQuery(id+"F0.wireOp",EDGE,"E3.24.0.0");var subQ1=sQuery(id+"F0.wireOp",EDGE,"E1.1.2.0");var subQ2=makeQuery(id+"F0.imprint","INTERSECT",VERTEX,{"disambiguationData":[OD(0.0)],"derivedFrom":[subQ1,subQ0]});Q62=makeQuery(id+"F0.imprint","IMPRINT",FACE,{"disambiguationData":[TD([[makeQuery(id+"F0.imprint","IMPRINT",EDGE,{"disambiguationData":[TD([[subQ2,-1.0]])],"derivedFrom":subQ1}),1.0]])]});}
            var Q63;
            {var subQ0=sQuery(id+"F0.wireOp",EDGE,"E3.7.0.0");var subQ1=sQuery(id+"F0.wireOp",EDGE,"E1.0.2.0");var subQ2=makeQuery(id+"F0.imprint","INTERSECT",VERTEX,{"disambiguationData":[OD(0.0)],"derivedFrom":[subQ1,subQ0]});Q63=makeQuery(id+"F0.imprint","IMPRINT",FACE,{"disambiguationData":[TD([[makeQuery(id+"F0.imprint","IMPRINT",EDGE,{"disambiguationData":[TD([[subQ2,-1.0]])],"derivedFrom":subQ1}),-1.0]])]});}
            var Q64;
            {var subQ0=sQuery(id+"F0.wireOp",EDGE,"E3.40.0.0");var subQ1=sQuery(id+"F0.wireOp",EDGE,"E1.2.2.0");var subQ2=makeQuery(id+"F0.imprint","INTERSECT",VERTEX,{"disambiguationData":[OD(0.0)],"derivedFrom":[subQ1,subQ0]});Q64=makeQuery(id+"F0.imprint","IMPRINT",FACE,{"disambiguationData":[TD([[makeQuery(id+"F0.imprint","IMPRINT",EDGE,{"disambiguationData":[TD([[subQ2,-1.0]])],"derivedFrom":subQ1}),-1.0]])]});}
            var Q65;
            {var subQ0=sQuery(id+"F0.wireOp",EDGE,"E3.22.0.0");var subQ1=sQuery(id+"F0.wireOp",EDGE,"E1.1.2.0");var subQ2=makeQuery(id+"F0.imprint","INTERSECT",VERTEX,{"disambiguationData":[OD(0.0)],"derivedFrom":[subQ1,subQ0]});Q65=makeQuery(id+"F0.imprint","IMPRINT",FACE,{"disambiguationData":[TD([[makeQuery(id+"F0.imprint","IMPRINT",EDGE,{"disambiguationData":[TD([[subQ2,-1.0]])],"derivedFrom":subQ1}),1.0]])]});}
            var Q66;
            {var subQ0=sQuery(id+"F0.wireOp",EDGE,"E3.32.0.0");var subQ1=sQuery(id+"F0.wireOp",EDGE,"E1.2.2.0");var subQ2=makeQuery(id+"F0.imprint","INTERSECT",VERTEX,{"disambiguationData":[OD(0.0)],"derivedFrom":[subQ1,subQ0]});Q66=makeQuery(id+"F0.imprint","IMPRINT",FACE,{"disambiguationData":[TD([[makeQuery(id+"F0.imprint","IMPRINT",EDGE,{"disambiguationData":[TD([[subQ2,-1.0]])],"derivedFrom":subQ1}),-1.0]])]});}
            var Q67;
            {var subQ0=sQuery(id+"F0.wireOp",EDGE,"E3.13.0.0");var subQ1=sQuery(id+"F0.wireOp",EDGE,"E1.0.2.0");var subQ2=makeQuery(id+"F0.imprint","INTERSECT",VERTEX,{"disambiguationData":[OD(0.0)],"derivedFrom":[subQ1,subQ0]});Q67=makeQuery(id+"F0.imprint","IMPRINT",FACE,{"disambiguationData":[TD([[makeQuery(id+"F0.imprint","IMPRINT",EDGE,{"disambiguationData":[TD([[subQ2,-1.0]])],"derivedFrom":subQ1}),-1.0]])]});}
            var Q68;
            {var subQ0=sQuery(id+"F0.wireOp",EDGE,"E3.33.0.0");var subQ1=sQuery(id+"F0.wireOp",EDGE,"E1.2.2.0");var subQ2=makeQuery(id+"F0.imprint","INTERSECT",VERTEX,{"disambiguationData":[OD(0.0)],"derivedFrom":[subQ1,subQ0]});Q68=makeQuery(id+"F0.imprint","IMPRINT",FACE,{"disambiguationData":[TD([[makeQuery(id+"F0.imprint","IMPRINT",EDGE,{"disambiguationData":[TD([[subQ2,-1.0]])],"derivedFrom":subQ1}),-1.0]])]});}
            var Q69;
            {var subQ0=sQuery(id+"F0.wireOp",EDGE,"E3.41.0.0");var subQ1=sQuery(id+"F0.wireOp",EDGE,"E1.2.2.0");var subQ2=makeQuery(id+"F0.imprint","INTERSECT",VERTEX,{"disambiguationData":[OD(0.0)],"derivedFrom":[subQ1,subQ0]});Q69=makeQuery(id+"F0.imprint","IMPRINT",FACE,{"disambiguationData":[TD([[makeQuery(id+"F0.imprint","IMPRINT",EDGE,{"disambiguationData":[TD([[subQ2,-1.0]])],"derivedFrom":subQ1}),-1.0]])]});}
            var Q70;
            {var subQ0=sQuery(id+"F0.wireOp",EDGE,"E3.14.0.0");var subQ1=sQuery(id+"F0.wireOp",EDGE,"E1.0.2.0");var subQ2=makeQuery(id+"F0.imprint","INTERSECT",VERTEX,{"disambiguationData":[OD(0.0)],"derivedFrom":[subQ1,subQ0]});Q70=makeQuery(id+"F0.imprint","IMPRINT",FACE,{"disambiguationData":[TD([[makeQuery(id+"F0.imprint","IMPRINT",EDGE,{"disambiguationData":[TD([[subQ2,-1.0]])],"derivedFrom":subQ1}),-1.0]])]});}
            var Q71;
            {var subQ0=sQuery(id+"F0.wireOp",EDGE,"E3.15.0.0");var subQ1=sQuery(id+"F0.wireOp",EDGE,"E1.1.2.0");var subQ2=makeQuery(id+"F0.imprint","INTERSECT",VERTEX,{"disambiguationData":[OD(0.0)],"derivedFrom":[subQ1,subQ0]});Q71=makeQuery(id+"F0.imprint","IMPRINT",FACE,{"disambiguationData":[TD([[makeQuery(id+"F0.imprint","IMPRINT",EDGE,{"disambiguationData":[TD([[subQ2,-1.0]])],"derivedFrom":subQ1}),1.0]])]});}
            var Q72;
            {var subQ0=sQuery(id+"F0.wireOp",EDGE,"E3.23.0.0");var subQ1=sQuery(id+"F0.wireOp",EDGE,"E1.1.2.0");var subQ2=makeQuery(id+"F0.imprint","INTERSECT",VERTEX,{"disambiguationData":[OD(0.0)],"derivedFrom":[subQ1,subQ0]});Q72=makeQuery(id+"F0.imprint","IMPRINT",FACE,{"disambiguationData":[TD([[makeQuery(id+"F0.imprint","IMPRINT",EDGE,{"disambiguationData":[TD([[subQ2,-1.0]])],"derivedFrom":subQ1}),1.0]])]});}
            var Q73;
            {var subQ0=sQuery(id+"F0.wireOp",EDGE,"E3.40.0.0");var subQ1=sQuery(id+"F0.wireOp",EDGE,"E1.2.2.0");var subQ2=makeQuery(id+"F0.imprint","INTERSECT",VERTEX,{"disambiguationData":[OD(0.0)],"derivedFrom":[subQ1,subQ0]});Q73=makeQuery(id+"F0.imprint","IMPRINT",FACE,{"disambiguationData":[TD([[makeQuery(id+"F0.imprint","IMPRINT",EDGE,{"disambiguationData":[TD([[subQ2,-1.0]])],"derivedFrom":subQ1}),1.0]])]});}
            var Q74;
            {var subQ0=sQuery(id+"F0.wireOp",EDGE,"E3.21.0.0");var subQ1=sQuery(id+"F0.wireOp",EDGE,"E1.1.2.0");var subQ2=makeQuery(id+"F0.imprint","INTERSECT",VERTEX,{"disambiguationData":[OD(0.0)],"derivedFrom":[subQ1,subQ0]});Q74=makeQuery(id+"F0.imprint","IMPRINT",FACE,{"disambiguationData":[TD([[makeQuery(id+"F0.imprint","IMPRINT",EDGE,{"disambiguationData":[TD([[subQ2,-1.0]])],"derivedFrom":subQ1}),-1.0]])]});}
            var Q75;
            {var subQ0=sQuery(id+"F0.wireOp",EDGE,"E3.32.0.0");var subQ1=sQuery(id+"F0.wireOp",EDGE,"E1.2.2.0");var subQ2=makeQuery(id+"F0.imprint","INTERSECT",VERTEX,{"disambiguationData":[OD(0.0)],"derivedFrom":[subQ1,subQ0]});Q75=makeQuery(id+"F0.imprint","IMPRINT",FACE,{"disambiguationData":[TD([[makeQuery(id+"F0.imprint","IMPRINT",EDGE,{"disambiguationData":[TD([[subQ2,-1.0]])],"derivedFrom":subQ1}),1.0]])]});}
            var Q76;
            {var subQ0=sQuery(id+"F0.wireOp",EDGE,"E3.13.0.0");var subQ1=sQuery(id+"F0.wireOp",EDGE,"E1.0.2.0");var subQ2=makeQuery(id+"F0.imprint","INTERSECT",VERTEX,{"disambiguationData":[OD(0.0)],"derivedFrom":[subQ1,subQ0]});Q76=makeQuery(id+"F0.imprint","IMPRINT",FACE,{"disambiguationData":[TD([[makeQuery(id+"F0.imprint","IMPRINT",EDGE,{"disambiguationData":[TD([[subQ2,-1.0]])],"derivedFrom":subQ1}),1.0]])]});}
            var Q77;
            {var subQ0=sQuery(id+"F0.wireOp",EDGE,"E3.33.0.0");var subQ1=sQuery(id+"F0.wireOp",EDGE,"E1.2.2.0");var subQ2=makeQuery(id+"F0.imprint","INTERSECT",VERTEX,{"disambiguationData":[OD(0.0)],"derivedFrom":[subQ1,subQ0]});Q77=makeQuery(id+"F0.imprint","IMPRINT",FACE,{"disambiguationData":[TD([[makeQuery(id+"F0.imprint","IMPRINT",EDGE,{"disambiguationData":[TD([[subQ2,-1.0]])],"derivedFrom":subQ1}),1.0]])]});}
            var Q78;
            {var subQ0=sQuery(id+"F0.wireOp",EDGE,"E3.41.0.0");var subQ1=sQuery(id+"F0.wireOp",EDGE,"E1.2.2.0");var subQ2=makeQuery(id+"F0.imprint","INTERSECT",VERTEX,{"disambiguationData":[OD(0.0)],"derivedFrom":[subQ1,subQ0]});Q78=makeQuery(id+"F0.imprint","IMPRINT",FACE,{"disambiguationData":[TD([[makeQuery(id+"F0.imprint","IMPRINT",EDGE,{"disambiguationData":[TD([[subQ2,-1.0]])],"derivedFrom":subQ1}),1.0]])]});}
            var Q79;
            {var subQ0=sQuery(id+"F0.wireOp",EDGE,"E3.14.0.0");var subQ1=sQuery(id+"F0.wireOp",EDGE,"E1.0.2.0");var subQ2=makeQuery(id+"F0.imprint","INTERSECT",VERTEX,{"disambiguationData":[OD(0.0)],"derivedFrom":[subQ1,subQ0]});Q79=makeQuery(id+"F0.imprint","IMPRINT",FACE,{"disambiguationData":[TD([[makeQuery(id+"F0.imprint","IMPRINT",EDGE,{"disambiguationData":[TD([[subQ2,-1.0]])],"derivedFrom":subQ1}),1.0]])]});}
            var Q80;
            {var subQ0=sQuery(id+"F0.wireOp",EDGE,"E3.22.0.0");var subQ1=sQuery(id+"F0.wireOp",EDGE,"E1.1.2.0");var subQ2=makeQuery(id+"F0.imprint","INTERSECT",VERTEX,{"disambiguationData":[OD(0.0)],"derivedFrom":[subQ1,subQ0]});Q80=makeQuery(id+"F0.imprint","IMPRINT",FACE,{"disambiguationData":[TD([[makeQuery(id+"F0.imprint","IMPRINT",EDGE,{"disambiguationData":[TD([[subQ2,-1.0]])],"derivedFrom":subQ1}),-1.0]])]});}
            var Q81;
            {var subQ0=sQuery(id+"F0.wireOp",EDGE,"E3.39.0.0");var subQ1=sQuery(id+"F0.wireOp",EDGE,"E1.2.2.0");var subQ2=makeQuery(id+"F0.imprint","INTERSECT",VERTEX,{"disambiguationData":[OD(0.0)],"derivedFrom":[subQ1,subQ0]});Q81=makeQuery(id+"F0.imprint","IMPRINT",FACE,{"disambiguationData":[TD([[makeQuery(id+"F0.imprint","IMPRINT",EDGE,{"disambiguationData":[TD([[subQ2,-1.0]])],"derivedFrom":subQ1}),-1.0]])]});}
            var Q82;
            {var subQ0=sQuery(id+"F0.wireOp",EDGE,"E3.21.0.0");var subQ1=sQuery(id+"F0.wireOp",EDGE,"E1.1.2.0");var subQ2=makeQuery(id+"F0.imprint","INTERSECT",VERTEX,{"disambiguationData":[OD(0.0)],"derivedFrom":[subQ1,subQ0]});Q82=makeQuery(id+"F0.imprint","IMPRINT",FACE,{"disambiguationData":[TD([[makeQuery(id+"F0.imprint","IMPRINT",EDGE,{"disambiguationData":[TD([[subQ2,-1.0]])],"derivedFrom":subQ1}),1.0]])]});}
            var Q83;
            {var subQ0=sQuery(id+"F0.wireOp",EDGE,"E3.31.0.0");var subQ1=sQuery(id+"F0.wireOp",EDGE,"E1.2.2.0");var subQ2=makeQuery(id+"F0.imprint","INTERSECT",VERTEX,{"disambiguationData":[OD(0.0)],"derivedFrom":[subQ1,subQ0]});Q83=makeQuery(id+"F0.imprint","IMPRINT",FACE,{"disambiguationData":[TD([[makeQuery(id+"F0.imprint","IMPRINT",EDGE,{"disambiguationData":[TD([[subQ2,-1.0]])],"derivedFrom":subQ1}),-1.0]])]});}
            var Q84;
            {var subQ0=sQuery(id+"F0.wireOp",EDGE,"E3.12.0.0");var subQ1=sQuery(id+"F0.wireOp",EDGE,"E1.0.2.0");var subQ2=makeQuery(id+"F0.imprint","INTERSECT",VERTEX,{"disambiguationData":[OD(0.0)],"derivedFrom":[subQ1,subQ0]});Q84=makeQuery(id+"F0.imprint","IMPRINT",FACE,{"disambiguationData":[TD([[makeQuery(id+"F0.imprint","IMPRINT",EDGE,{"disambiguationData":[TD([[subQ2,-1.0]])],"derivedFrom":subQ1}),-1.0]])]});}
            var Q85;
            {var subQ0=sQuery(id+"F0.wireOp",EDGE,"E2");var subQ1=sQuery(id+"F0.wireOp",EDGE,"E1.0.2.0");var subQ2=makeQuery(id+"F0.imprint","INTERSECT",VERTEX,{"disambiguationData":[OD(0.0)],"derivedFrom":[subQ1,subQ0]});Q85=makeQuery(id+"F0.imprint","IMPRINT",FACE,{"disambiguationData":[TD([[makeQuery(id+"F0.imprint","IMPRINT",EDGE,{"disambiguationData":[TD([[subQ2,-1.0]])],"derivedFrom":subQ1}),1.0]])]});}
            var Q86;
            {var subQ0=sQuery(id+"F0.wireOp",EDGE,"E3.1.0.0");var subQ1=sQuery(id+"F0.wireOp",EDGE,"E1.0.2.0");var subQ2=makeQuery(id+"F0.imprint","INTERSECT",VERTEX,{"disambiguationData":[OD(0.0)],"derivedFrom":[subQ1,subQ0]});Q86=makeQuery(id+"F0.imprint","IMPRINT",FACE,{"disambiguationData":[TD([[makeQuery(id+"F0.imprint","IMPRINT",EDGE,{"disambiguationData":[TD([[subQ2,-1.0]])],"derivedFrom":subQ1}),-1.0]])]});}
            var Q87;
            {var subQ0=sQuery(id+"F0.wireOp",EDGE,"E2");var subQ1=sQuery(id+"F0.wireOp",EDGE,"E1.0.2.0");var subQ2=makeQuery(id+"F0.imprint","INTERSECT",VERTEX,{"disambiguationData":[OD(0.0)],"derivedFrom":[subQ1,subQ0]});Q87=makeQuery(id+"F0.imprint","IMPRINT",FACE,{"disambiguationData":[TD([[makeQuery(id+"F0.imprint","IMPRINT",EDGE,{"disambiguationData":[TD([[subQ2,-1.0]])],"derivedFrom":subQ1}),-1.0]])]});}
            var Q88;
            {var subQ1=sQuery(id+"F0.wireOp",EDGE,"E1.1.2.0");var subQ3=sQuery(id+"F0.wireOp",EDGE,"E3.29.0.0");var subQ4=makeQuery(id+"F0.imprint","INTERSECT",VERTEX,{"derivedFrom":[subQ1,subQ3]});Q88=makeQuery(id+"F0.imprint","IMPRINT",FACE,{"disambiguationData":[TD([[makeQuery(id+"F0.imprint","IMPRINT",EDGE,{"disambiguationData":[TD([[subQ4,1.0]])],"derivedFrom":subQ3}),1.0]])]});}
            var Q89;
            {var subQ1=sQuery(id+"F0.wireOp",EDGE,"E1.1.2.0");var subQ3=sQuery(id+"F0.wireOp",EDGE,"E3.29.0.0");var subQ4=makeQuery(id+"F0.imprint","INTERSECT",VERTEX,{"derivedFrom":[subQ1,subQ3]});Q89=makeQuery(id+"F0.imprint","IMPRINT",FACE,{"disambiguationData":[TD([[makeQuery(id+"F0.imprint","IMPRINT",EDGE,{"disambiguationData":[TD([[subQ4,-1.0]])],"derivedFrom":subQ3}),1.0]])]});}
            var Q90;
            {var subQ0=sQuery(id+"F0.wireOp",EDGE,"E3.21.1.0");var subQ1=sQuery(id+"F0.wireOp",EDGE,"E1.1.5.0");var subQ2=makeQuery(id+"F0.imprint","INTERSECT",VERTEX,{"disambiguationData":[OD(0.0)],"derivedFrom":[subQ1,subQ0]});Q90=makeQuery(id+"F0.imprint","IMPRINT",FACE,{"disambiguationData":[TD([[makeQuery(id+"F0.imprint","IMPRINT",EDGE,{"disambiguationData":[TD([[subQ2,-1.0]])],"derivedFrom":subQ1}),1.0]])]});}
            var Q91;
            {var subQ0=sQuery(id+"F0.wireOp",EDGE,"E3.22.1.0");var subQ1=sQuery(id+"F0.wireOp",EDGE,"E1.1.5.0");var subQ2=makeQuery(id+"F0.imprint","INTERSECT",VERTEX,{"disambiguationData":[OD(0.0)],"derivedFrom":[subQ1,subQ0]});Q91=makeQuery(id+"F0.imprint","IMPRINT",FACE,{"disambiguationData":[TD([[makeQuery(id+"F0.imprint","IMPRINT",EDGE,{"disambiguationData":[TD([[subQ2,-1.0]])],"derivedFrom":subQ1}),1.0]])]});}
            var Q92;
            {var subQ0=sQuery(id+"F0.wireOp",EDGE,"E3.2.1.0");var subQ1=sQuery(id+"F0.wireOp",EDGE,"E1.0.5.0");var subQ2=makeQuery(id+"F0.imprint","INTERSECT",VERTEX,{"disambiguationData":[OD(0.0)],"derivedFrom":[subQ1,subQ0]});Q92=makeQuery(id+"F0.imprint","IMPRINT",FACE,{"disambiguationData":[TD([[makeQuery(id+"F0.imprint","IMPRINT",EDGE,{"disambiguationData":[TD([[subQ2,-1.0]])],"derivedFrom":subQ1}),1.0]])]});}
            var Q93;
            {var subQ0=sQuery(id+"F0.wireOp",EDGE,"E3.30.1.0");var subQ1=sQuery(id+"F0.wireOp",EDGE,"E1.2.5.0");var subQ2=makeQuery(id+"F0.imprint","INTERSECT",VERTEX,{"disambiguationData":[OD(0.0)],"derivedFrom":[subQ1,subQ0]});Q93=makeQuery(id+"F0.imprint","IMPRINT",FACE,{"disambiguationData":[TD([[makeQuery(id+"F0.imprint","IMPRINT",EDGE,{"disambiguationData":[TD([[subQ2,-1.0]])],"derivedFrom":subQ1}),1.0]])]});}
            var Q94;
            {var subQ0=sQuery(id+"F0.wireOp",EDGE,"E3.40.1.0");var subQ1=sQuery(id+"F0.wireOp",EDGE,"E1.2.5.0");var subQ2=makeQuery(id+"F0.imprint","INTERSECT",VERTEX,{"disambiguationData":[OD(0.0)],"derivedFrom":[subQ1,subQ0]});Q94=makeQuery(id+"F0.imprint","IMPRINT",FACE,{"disambiguationData":[TD([[makeQuery(id+"F0.imprint","IMPRINT",EDGE,{"disambiguationData":[TD([[subQ2,-1.0]])],"derivedFrom":subQ1}),1.0]])]});}
            var Q95;
            {var subQ0=sQuery(id+"F0.wireOp",EDGE,"E3.41.1.0");var subQ1=sQuery(id+"F0.wireOp",EDGE,"E1.2.5.0");var subQ2=makeQuery(id+"F0.imprint","INTERSECT",VERTEX,{"disambiguationData":[OD(0.0)],"derivedFrom":[subQ1,subQ0]});Q95=makeQuery(id+"F0.imprint","IMPRINT",FACE,{"disambiguationData":[TD([[makeQuery(id+"F0.imprint","IMPRINT",EDGE,{"disambiguationData":[TD([[subQ2,-1.0]])],"derivedFrom":subQ1}),1.0]])]});}
            var Q96;
            {var subQ0=sQuery(id+"F0.wireOp",EDGE,"E3.10.1.0");var subQ1=sQuery(id+"F0.wireOp",EDGE,"E1.0.5.0");var subQ2=makeQuery(id+"F0.imprint","INTERSECT",VERTEX,{"disambiguationData":[OD(0.0)],"derivedFrom":[subQ1,subQ0]});Q96=makeQuery(id+"F0.imprint","IMPRINT",FACE,{"disambiguationData":[TD([[makeQuery(id+"F0.imprint","IMPRINT",EDGE,{"disambiguationData":[TD([[subQ2,-1.0]])],"derivedFrom":subQ1}),1.0]])]});}
            var Q97;
            {var subQ0=sQuery(id+"F0.wireOp",EDGE,"E3.39.1.0");var subQ1=sQuery(id+"F0.wireOp",EDGE,"E1.2.5.0");var subQ2=makeQuery(id+"F0.imprint","INTERSECT",VERTEX,{"disambiguationData":[OD(0.0)],"derivedFrom":[subQ1,subQ0]});Q97=makeQuery(id+"F0.imprint","IMPRINT",FACE,{"disambiguationData":[TD([[makeQuery(id+"F0.imprint","IMPRINT",EDGE,{"disambiguationData":[TD([[subQ2,-1.0]])],"derivedFrom":subQ1}),1.0]])]});}
            var Q98;
            {var subQ0=sQuery(id+"F0.wireOp",EDGE,"E3.36.1.0");var subQ1=sQuery(id+"F0.wireOp",EDGE,"E1.2.5.0");var subQ2=makeQuery(id+"F0.imprint","INTERSECT",VERTEX,{"disambiguationData":[OD(0.0)],"derivedFrom":[subQ1,subQ0]});Q98=makeQuery(id+"F0.imprint","IMPRINT",FACE,{"disambiguationData":[TD([[makeQuery(id+"F0.imprint","IMPRINT",EDGE,{"disambiguationData":[TD([[subQ2,-1.0]])],"derivedFrom":subQ1}),1.0]])]});}
            var Q99;
            {var subQ0=sQuery(id+"F0.wireOp",EDGE,"E3.38.1.0");var subQ1=sQuery(id+"F0.wireOp",EDGE,"E1.2.5.0");var subQ2=makeQuery(id+"F0.imprint","INTERSECT",VERTEX,{"disambiguationData":[OD(0.0)],"derivedFrom":[subQ1,subQ0]});Q99=makeQuery(id+"F0.imprint","IMPRINT",FACE,{"disambiguationData":[TD([[makeQuery(id+"F0.imprint","IMPRINT",EDGE,{"disambiguationData":[TD([[subQ2,-1.0]])],"derivedFrom":subQ1}),1.0]])]});}
            var Q100;
            {var subQ0=sQuery(id+"F0.wireOp",EDGE,"E3.3.1.0");var subQ1=sQuery(id+"F0.wireOp",EDGE,"E1.0.5.0");var subQ2=makeQuery(id+"F0.imprint","INTERSECT",VERTEX,{"disambiguationData":[OD(0.0)],"derivedFrom":[subQ1,subQ0]});Q100=makeQuery(id+"F0.imprint","IMPRINT",FACE,{"disambiguationData":[TD([[makeQuery(id+"F0.imprint","IMPRINT",EDGE,{"disambiguationData":[TD([[subQ2,-1.0]])],"derivedFrom":subQ1}),1.0]])]});}
            var Q101;
            {var subQ0=sQuery(id+"F0.wireOp",EDGE,"E3.11.1.0");var subQ1=sQuery(id+"F0.wireOp",EDGE,"E1.0.5.0");var subQ2=makeQuery(id+"F0.imprint","INTERSECT",VERTEX,{"disambiguationData":[OD(0.0)],"derivedFrom":[subQ1,subQ0]});Q101=makeQuery(id+"F0.imprint","IMPRINT",FACE,{"disambiguationData":[TD([[makeQuery(id+"F0.imprint","IMPRINT",EDGE,{"disambiguationData":[TD([[subQ2,-1.0]])],"derivedFrom":subQ1}),1.0]])]});}
            var Q102;
            {var subQ0=sQuery(id+"F0.wireOp",EDGE,"E3.31.1.0");var subQ1=sQuery(id+"F0.wireOp",EDGE,"E1.2.5.0");var subQ2=makeQuery(id+"F0.imprint","INTERSECT",VERTEX,{"disambiguationData":[OD(0.0)],"derivedFrom":[subQ1,subQ0]});Q102=makeQuery(id+"F0.imprint","IMPRINT",FACE,{"disambiguationData":[TD([[makeQuery(id+"F0.imprint","IMPRINT",EDGE,{"disambiguationData":[TD([[subQ2,-1.0]])],"derivedFrom":subQ1}),1.0]])]});}
            var Q103;
            {var subQ0=sQuery(id+"F0.wireOp",EDGE,"E3.4.1.0");var subQ1=sQuery(id+"F0.wireOp",EDGE,"E1.0.5.0");var subQ2=makeQuery(id+"F0.imprint","INTERSECT",VERTEX,{"disambiguationData":[OD(0.0)],"derivedFrom":[subQ1,subQ0]});Q103=makeQuery(id+"F0.imprint","IMPRINT",FACE,{"disambiguationData":[TD([[makeQuery(id+"F0.imprint","IMPRINT",EDGE,{"disambiguationData":[TD([[subQ2,-1.0]])],"derivedFrom":subQ1}),1.0]])]});}
            var Q104;
            {var subQ0=sQuery(id+"F0.wireOp",EDGE,"E3.33.1.0");var subQ1=sQuery(id+"F0.wireOp",EDGE,"E1.2.5.0");var subQ2=makeQuery(id+"F0.imprint","INTERSECT",VERTEX,{"disambiguationData":[OD(0.0)],"derivedFrom":[subQ1,subQ0]});Q104=makeQuery(id+"F0.imprint","IMPRINT",FACE,{"disambiguationData":[TD([[makeQuery(id+"F0.imprint","IMPRINT",EDGE,{"disambiguationData":[TD([[subQ2,-1.0]])],"derivedFrom":subQ1}),1.0]])]});}
            var Q105;
            {var subQ0=sQuery(id+"F0.wireOp",EDGE,"E3.12.1.0");var subQ1=sQuery(id+"F0.wireOp",EDGE,"E1.0.5.0");var subQ2=makeQuery(id+"F0.imprint","INTERSECT",VERTEX,{"disambiguationData":[OD(0.0)],"derivedFrom":[subQ1,subQ0]});Q105=makeQuery(id+"F0.imprint","IMPRINT",FACE,{"disambiguationData":[TD([[makeQuery(id+"F0.imprint","IMPRINT",EDGE,{"disambiguationData":[TD([[subQ2,-1.0]])],"derivedFrom":subQ1}),1.0]])]});}
            var Q106;
            {var subQ0=sQuery(id+"F0.wireOp",EDGE,"E3.28.1.0");var subQ1=sQuery(id+"F0.wireOp",EDGE,"E1.1.5.0");var subQ2=makeQuery(id+"F0.imprint","INTERSECT",VERTEX,{"disambiguationData":[OD(0.0)],"derivedFrom":[subQ1,subQ0]});Q106=makeQuery(id+"F0.imprint","IMPRINT",FACE,{"disambiguationData":[TD([[makeQuery(id+"F0.imprint","IMPRINT",EDGE,{"disambiguationData":[TD([[subQ2,-1.0]])],"derivedFrom":subQ1}),1.0]])]});}
            var Q107;
            {var subQ0=sQuery(id+"F0.wireOp",EDGE,"E3.20.1.0");var subQ1=sQuery(id+"F0.wireOp",EDGE,"E1.1.5.0");var subQ2=makeQuery(id+"F0.imprint","INTERSECT",VERTEX,{"disambiguationData":[OD(0.0)],"derivedFrom":[subQ1,subQ0]});Q107=makeQuery(id+"F0.imprint","IMPRINT",FACE,{"disambiguationData":[TD([[makeQuery(id+"F0.imprint","IMPRINT",EDGE,{"disambiguationData":[TD([[subQ2,-1.0]])],"derivedFrom":subQ1}),1.0]])]});}
            var Q108;
            {var subQ0=sQuery(id+"F0.wireOp",EDGE,"E3.13.1.0");var subQ1=sQuery(id+"F0.wireOp",EDGE,"E1.0.5.0");var subQ2=makeQuery(id+"F0.imprint","INTERSECT",VERTEX,{"disambiguationData":[OD(0.0)],"derivedFrom":[subQ1,subQ0]});Q108=makeQuery(id+"F0.imprint","IMPRINT",FACE,{"disambiguationData":[TD([[makeQuery(id+"F0.imprint","IMPRINT",EDGE,{"disambiguationData":[TD([[subQ2,-1.0]])],"derivedFrom":subQ1}),1.0]])]});}
            var Q109;
            {var subQ0=sQuery(id+"F0.wireOp",EDGE,"E3.5.1.0");var subQ1=sQuery(id+"F0.wireOp",EDGE,"E1.0.5.0");var subQ2=makeQuery(id+"F0.imprint","INTERSECT",VERTEX,{"disambiguationData":[OD(0.0)],"derivedFrom":[subQ1,subQ0]});Q109=makeQuery(id+"F0.imprint","IMPRINT",FACE,{"disambiguationData":[TD([[makeQuery(id+"F0.imprint","IMPRINT",EDGE,{"disambiguationData":[TD([[subQ2,-1.0]])],"derivedFrom":subQ1}),1.0]])]});}
            var Q110;
            {var subQ0=sQuery(id+"F0.wireOp",EDGE,"E3.32.1.0");var subQ1=sQuery(id+"F0.wireOp",EDGE,"E1.2.5.0");var subQ2=makeQuery(id+"F0.imprint","INTERSECT",VERTEX,{"disambiguationData":[OD(0.0)],"derivedFrom":[subQ1,subQ0]});Q110=makeQuery(id+"F0.imprint","IMPRINT",FACE,{"disambiguationData":[TD([[makeQuery(id+"F0.imprint","IMPRINT",EDGE,{"disambiguationData":[TD([[subQ2,-1.0]])],"derivedFrom":subQ1}),1.0]])]});}
            var Q111;
            {var subQ0=sQuery(id+"F0.wireOp",EDGE,"E3.8.1.0");var subQ1=sQuery(id+"F0.wireOp",EDGE,"E1.0.5.0");var subQ2=makeQuery(id+"F0.imprint","INTERSECT",VERTEX,{"disambiguationData":[OD(0.0)],"derivedFrom":[subQ1,subQ0]});Q111=makeQuery(id+"F0.imprint","IMPRINT",FACE,{"disambiguationData":[TD([[makeQuery(id+"F0.imprint","IMPRINT",EDGE,{"disambiguationData":[TD([[subQ2,-1.0]])],"derivedFrom":subQ1}),1.0]])]});}
            var Q112;
            {var subQ0=sQuery(id+"F0.wireOp",EDGE,"E3.19.1.0");var subQ1=sQuery(id+"F0.wireOp",EDGE,"E1.1.5.0");var subQ2=makeQuery(id+"F0.imprint","INTERSECT",VERTEX,{"disambiguationData":[OD(0.0)],"derivedFrom":[subQ1,subQ0]});Q112=makeQuery(id+"F0.imprint","IMPRINT",FACE,{"disambiguationData":[TD([[makeQuery(id+"F0.imprint","IMPRINT",EDGE,{"disambiguationData":[TD([[subQ2,-1.0]])],"derivedFrom":subQ1}),1.0]])]});}
            var Q113;
            {var subQ0=sQuery(id+"F0.wireOp",EDGE,"E3.27.1.0");var subQ1=sQuery(id+"F0.wireOp",EDGE,"E1.1.5.0");var subQ2=makeQuery(id+"F0.imprint","INTERSECT",VERTEX,{"disambiguationData":[OD(0.0)],"derivedFrom":[subQ1,subQ0]});Q113=makeQuery(id+"F0.imprint","IMPRINT",FACE,{"disambiguationData":[TD([[makeQuery(id+"F0.imprint","IMPRINT",EDGE,{"disambiguationData":[TD([[subQ2,-1.0]])],"derivedFrom":subQ1}),1.0]])]});}
            var Q114;
            {var subQ0=sQuery(id+"F0.wireOp",EDGE,"E3.37.1.0");var subQ1=sQuery(id+"F0.wireOp",EDGE,"E1.2.5.0");var subQ2=makeQuery(id+"F0.imprint","INTERSECT",VERTEX,{"disambiguationData":[OD(0.0)],"derivedFrom":[subQ1,subQ0]});Q114=makeQuery(id+"F0.imprint","IMPRINT",FACE,{"disambiguationData":[TD([[makeQuery(id+"F0.imprint","IMPRINT",EDGE,{"disambiguationData":[TD([[subQ2,-1.0]])],"derivedFrom":subQ1}),1.0]])]});}
            var Q115;
            {var subQ0=sQuery(id+"F0.wireOp",EDGE,"E3.1.1.0");var subQ1=sQuery(id+"F0.wireOp",EDGE,"E1.0.5.0");var subQ2=makeQuery(id+"F0.imprint","INTERSECT",VERTEX,{"disambiguationData":[OD(0.0)],"derivedFrom":[subQ1,subQ0]});Q115=makeQuery(id+"F0.imprint","IMPRINT",FACE,{"disambiguationData":[TD([[makeQuery(id+"F0.imprint","IMPRINT",EDGE,{"disambiguationData":[TD([[subQ2,-1.0]])],"derivedFrom":subQ1}),1.0]])]});}
            var Q116;
            {var subQ0=sQuery(id+"F0.wireOp",EDGE,"E3.9.1.0");var subQ1=sQuery(id+"F0.wireOp",EDGE,"E1.0.5.0");var subQ2=makeQuery(id+"F0.imprint","INTERSECT",VERTEX,{"disambiguationData":[OD(0.0)],"derivedFrom":[subQ1,subQ0]});Q116=makeQuery(id+"F0.imprint","IMPRINT",FACE,{"disambiguationData":[TD([[makeQuery(id+"F0.imprint","IMPRINT",EDGE,{"disambiguationData":[TD([[subQ2,-1.0]])],"derivedFrom":subQ1}),1.0]])]});}
            var Q117;
            {var subQ0=sQuery(id+"F0.wireOp",EDGE,"E3.18.1.0");var subQ1=sQuery(id+"F0.wireOp",EDGE,"E1.1.5.0");var subQ2=makeQuery(id+"F0.imprint","INTERSECT",VERTEX,{"disambiguationData":[OD(0.0)],"derivedFrom":[subQ1,subQ0]});Q117=makeQuery(id+"F0.imprint","IMPRINT",FACE,{"disambiguationData":[TD([[makeQuery(id+"F0.imprint","IMPRINT",EDGE,{"disambiguationData":[TD([[subQ2,-1.0]])],"derivedFrom":subQ1}),1.0]])]});}
            var Q118;
            {var subQ0=sQuery(id+"F0.wireOp",EDGE,"E3.26.1.0");var subQ1=sQuery(id+"F0.wireOp",EDGE,"E1.1.5.0");var subQ2=makeQuery(id+"F0.imprint","INTERSECT",VERTEX,{"disambiguationData":[OD(0.0)],"derivedFrom":[subQ1,subQ0]});Q118=makeQuery(id+"F0.imprint","IMPRINT",FACE,{"disambiguationData":[TD([[makeQuery(id+"F0.imprint","IMPRINT",EDGE,{"disambiguationData":[TD([[subQ2,-1.0]])],"derivedFrom":subQ1}),1.0]])]});}
            var Q119;
            {var subQ0=sQuery(id+"F0.wireOp",EDGE,"E3.16.1.0");var subQ1=sQuery(id+"F0.wireOp",EDGE,"E1.1.5.0");var subQ2=makeQuery(id+"F0.imprint","INTERSECT",VERTEX,{"disambiguationData":[OD(0.0)],"derivedFrom":[subQ1,subQ0]});Q119=makeQuery(id+"F0.imprint","IMPRINT",FACE,{"disambiguationData":[TD([[makeQuery(id+"F0.imprint","IMPRINT",EDGE,{"disambiguationData":[TD([[subQ2,-1.0]])],"derivedFrom":subQ1}),1.0]])]});}
            var Q120;
            {var subQ0=sQuery(id+"F0.wireOp",EDGE,"E3.24.1.0");var subQ1=sQuery(id+"F0.wireOp",EDGE,"E1.1.5.0");var subQ2=makeQuery(id+"F0.imprint","INTERSECT",VERTEX,{"disambiguationData":[OD(0.0)],"derivedFrom":[subQ1,subQ0]});Q120=makeQuery(id+"F0.imprint","IMPRINT",FACE,{"disambiguationData":[TD([[makeQuery(id+"F0.imprint","IMPRINT",EDGE,{"disambiguationData":[TD([[subQ2,-1.0]])],"derivedFrom":subQ1}),1.0]])]});}
            var Q121;
            {var subQ0=sQuery(id+"F0.wireOp",EDGE,"E3.17.1.0");var subQ1=sQuery(id+"F0.wireOp",EDGE,"E1.1.5.0");var subQ2=makeQuery(id+"F0.imprint","INTERSECT",VERTEX,{"disambiguationData":[OD(0.0)],"derivedFrom":[subQ1,subQ0]});Q121=makeQuery(id+"F0.imprint","IMPRINT",FACE,{"disambiguationData":[TD([[makeQuery(id+"F0.imprint","IMPRINT",EDGE,{"disambiguationData":[TD([[subQ2,-1.0]])],"derivedFrom":subQ1}),1.0]])]});}
            var Q122;
            {var subQ0=sQuery(id+"F0.wireOp",EDGE,"E3.25.1.0");var subQ1=sQuery(id+"F0.wireOp",EDGE,"E1.1.5.0");var subQ2=makeQuery(id+"F0.imprint","INTERSECT",VERTEX,{"disambiguationData":[OD(0.0)],"derivedFrom":[subQ1,subQ0]});Q122=makeQuery(id+"F0.imprint","IMPRINT",FACE,{"disambiguationData":[TD([[makeQuery(id+"F0.imprint","IMPRINT",EDGE,{"disambiguationData":[TD([[subQ2,-1.0]])],"derivedFrom":subQ1}),1.0]])]});}
            var Q123;
            {var subQ0=sQuery(id+"F0.wireOp",EDGE,"E3.34.1.0");var subQ1=sQuery(id+"F0.wireOp",EDGE,"E1.2.5.0");var subQ2=makeQuery(id+"F0.imprint","INTERSECT",VERTEX,{"disambiguationData":[OD(0.0)],"derivedFrom":[subQ1,subQ0]});Q123=makeQuery(id+"F0.imprint","IMPRINT",FACE,{"disambiguationData":[TD([[makeQuery(id+"F0.imprint","IMPRINT",EDGE,{"disambiguationData":[TD([[subQ2,-1.0]])],"derivedFrom":subQ1}),1.0]])]});}
            var Q124;
            {var subQ0=sQuery(id+"F0.wireOp",EDGE,"E3.42.1.0");var subQ1=sQuery(id+"F0.wireOp",EDGE,"E1.2.5.0");var subQ2=makeQuery(id+"F0.imprint","INTERSECT",VERTEX,{"disambiguationData":[OD(0.0)],"derivedFrom":[subQ1,subQ0]});Q124=makeQuery(id+"F0.imprint","IMPRINT",FACE,{"disambiguationData":[TD([[makeQuery(id+"F0.imprint","IMPRINT",EDGE,{"disambiguationData":[TD([[subQ2,-1.0]])],"derivedFrom":subQ1}),1.0]])]});}
            var Q125;
            {var subQ0=sQuery(id+"F0.wireOp",EDGE,"E3.6.1.0");var subQ1=sQuery(id+"F0.wireOp",EDGE,"E1.0.5.0");var subQ2=makeQuery(id+"F0.imprint","INTERSECT",VERTEX,{"disambiguationData":[OD(0.0)],"derivedFrom":[subQ1,subQ0]});Q125=makeQuery(id+"F0.imprint","IMPRINT",FACE,{"disambiguationData":[TD([[makeQuery(id+"F0.imprint","IMPRINT",EDGE,{"disambiguationData":[TD([[subQ2,-1.0]])],"derivedFrom":subQ1}),1.0]])]});}
            var Q126;
            {var subQ0=sQuery(id+"F0.wireOp",EDGE,"E3.35.1.0");var subQ1=sQuery(id+"F0.wireOp",EDGE,"E1.2.5.0");var subQ2=makeQuery(id+"F0.imprint","INTERSECT",VERTEX,{"disambiguationData":[OD(0.0)],"derivedFrom":[subQ1,subQ0]});Q126=makeQuery(id+"F0.imprint","IMPRINT",FACE,{"disambiguationData":[TD([[makeQuery(id+"F0.imprint","IMPRINT",EDGE,{"disambiguationData":[TD([[subQ2,-1.0]])],"derivedFrom":subQ1}),1.0]])]});}
            var Q127;
            {var subQ0=sQuery(id+"F0.wireOp",EDGE,"E3.7.1.0");var subQ1=sQuery(id+"F0.wireOp",EDGE,"E1.0.5.0");var subQ2=makeQuery(id+"F0.imprint","INTERSECT",VERTEX,{"disambiguationData":[OD(0.0)],"derivedFrom":[subQ1,subQ0]});Q127=makeQuery(id+"F0.imprint","IMPRINT",FACE,{"disambiguationData":[TD([[makeQuery(id+"F0.imprint","IMPRINT",EDGE,{"disambiguationData":[TD([[subQ2,-1.0]])],"derivedFrom":subQ1}),1.0]])]});}
            var Q128;
            {var subQ0=sQuery(id+"F0.wireOp",EDGE,"E3.15.1.0");var subQ1=sQuery(id+"F0.wireOp",EDGE,"E1.1.5.0");var subQ2=makeQuery(id+"F0.imprint","INTERSECT",VERTEX,{"disambiguationData":[OD(0.0)],"derivedFrom":[subQ1,subQ0]});Q128=makeQuery(id+"F0.imprint","IMPRINT",FACE,{"disambiguationData":[TD([[makeQuery(id+"F0.imprint","IMPRINT",EDGE,{"disambiguationData":[TD([[subQ2,-1.0]])],"derivedFrom":subQ1}),1.0]])]});}
            var Q129;
            {var subQ0=sQuery(id+"F0.wireOp",EDGE,"E3.23.1.0");var subQ1=sQuery(id+"F0.wireOp",EDGE,"E1.1.5.0");var subQ2=makeQuery(id+"F0.imprint","INTERSECT",VERTEX,{"disambiguationData":[OD(0.0)],"derivedFrom":[subQ1,subQ0]});Q129=makeQuery(id+"F0.imprint","IMPRINT",FACE,{"disambiguationData":[TD([[makeQuery(id+"F0.imprint","IMPRINT",EDGE,{"disambiguationData":[TD([[subQ2,-1.0]])],"derivedFrom":subQ1}),1.0]])]});}
            var Q130;
            {var subQ0=sQuery(id+"F0.wireOp",EDGE,"E3.39.1.0");var subQ1=sQuery(id+"F0.wireOp",EDGE,"E1.2.5.0");var subQ2=makeQuery(id+"F0.imprint","INTERSECT",VERTEX,{"disambiguationData":[OD(0.0)],"derivedFrom":[subQ1,subQ0]});Q130=makeQuery(id+"F0.imprint","IMPRINT",FACE,{"disambiguationData":[TD([[makeQuery(id+"F0.imprint","IMPRINT",EDGE,{"disambiguationData":[TD([[subQ2,-1.0]])],"derivedFrom":subQ1}),-1.0]])]});}
            var Q131;
            {var subQ0=sQuery(id+"F0.wireOp",EDGE,"E3.20.1.0");var subQ1=sQuery(id+"F0.wireOp",EDGE,"E1.1.5.0");var subQ2=makeQuery(id+"F0.imprint","INTERSECT",VERTEX,{"disambiguationData":[OD(0.0)],"derivedFrom":[subQ1,subQ0]});Q131=makeQuery(id+"F0.imprint","IMPRINT",FACE,{"disambiguationData":[TD([[makeQuery(id+"F0.imprint","IMPRINT",EDGE,{"disambiguationData":[TD([[subQ2,-1.0]])],"derivedFrom":subQ1}),-1.0]])]});}
            var Q132;
            {var subQ0=sQuery(id+"F0.wireOp",EDGE,"E3.27.1.0");var subQ1=sQuery(id+"F0.wireOp",EDGE,"E1.1.5.0");var subQ2=makeQuery(id+"F0.imprint","INTERSECT",VERTEX,{"disambiguationData":[OD(0.0)],"derivedFrom":[subQ1,subQ0]});Q132=makeQuery(id+"F0.imprint","IMPRINT",FACE,{"disambiguationData":[TD([[makeQuery(id+"F0.imprint","IMPRINT",EDGE,{"disambiguationData":[TD([[subQ2,-1.0]])],"derivedFrom":subQ1}),-1.0]])]});}
            var Q133;
            {var subQ0=sQuery(id+"F0.wireOp",EDGE,"E3.2.1.0");var subQ1=sQuery(id+"F0.wireOp",EDGE,"E1.0.5.0");var subQ2=makeQuery(id+"F0.imprint","INTERSECT",VERTEX,{"disambiguationData":[OD(0.0)],"derivedFrom":[subQ1,subQ0]});Q133=makeQuery(id+"F0.imprint","IMPRINT",FACE,{"disambiguationData":[TD([[makeQuery(id+"F0.imprint","IMPRINT",EDGE,{"disambiguationData":[TD([[subQ2,-1.0]])],"derivedFrom":subQ1}),-1.0]])]});}
            var Q134;
            {var subQ0=sQuery(id+"F0.wireOp",EDGE,"E3.32.1.0");var subQ1=sQuery(id+"F0.wireOp",EDGE,"E1.2.5.0");var subQ2=makeQuery(id+"F0.imprint","INTERSECT",VERTEX,{"disambiguationData":[OD(0.0)],"derivedFrom":[subQ1,subQ0]});Q134=makeQuery(id+"F0.imprint","IMPRINT",FACE,{"disambiguationData":[TD([[makeQuery(id+"F0.imprint","IMPRINT",EDGE,{"disambiguationData":[TD([[subQ2,-1.0]])],"derivedFrom":subQ1}),-1.0]])]});}
            var Q135;
            {var subQ0=sQuery(id+"F0.wireOp",EDGE,"E3.10.1.0");var subQ1=sQuery(id+"F0.wireOp",EDGE,"E1.0.5.0");var subQ2=makeQuery(id+"F0.imprint","INTERSECT",VERTEX,{"disambiguationData":[OD(0.0)],"derivedFrom":[subQ1,subQ0]});Q135=makeQuery(id+"F0.imprint","IMPRINT",FACE,{"disambiguationData":[TD([[makeQuery(id+"F0.imprint","IMPRINT",EDGE,{"disambiguationData":[TD([[subQ2,-1.0]])],"derivedFrom":subQ1}),-1.0]])]});}
            var Q136;
            {var subQ0=sQuery(id+"F0.wireOp",EDGE,"E3.30.1.0");var subQ1=sQuery(id+"F0.wireOp",EDGE,"E1.2.5.0");var subQ2=makeQuery(id+"F0.imprint","INTERSECT",VERTEX,{"disambiguationData":[OD(0.0)],"derivedFrom":[subQ1,subQ0]});Q136=makeQuery(id+"F0.imprint","IMPRINT",FACE,{"disambiguationData":[TD([[makeQuery(id+"F0.imprint","IMPRINT",EDGE,{"disambiguationData":[TD([[subQ2,-1.0]])],"derivedFrom":subQ1}),-1.0]])]});}
            var Q137;
            {var subQ0=sQuery(id+"F0.wireOp",EDGE,"E3.31.1.0");var subQ1=sQuery(id+"F0.wireOp",EDGE,"E1.2.5.0");var subQ2=makeQuery(id+"F0.imprint","INTERSECT",VERTEX,{"disambiguationData":[OD(0.0)],"derivedFrom":[subQ1,subQ0]});Q137=makeQuery(id+"F0.imprint","IMPRINT",FACE,{"disambiguationData":[TD([[makeQuery(id+"F0.imprint","IMPRINT",EDGE,{"disambiguationData":[TD([[subQ2,-1.0]])],"derivedFrom":subQ1}),-1.0]])]});}
            var Q138;
            {var subQ0=sQuery(id+"F0.wireOp",EDGE,"E3.11.1.0");var subQ1=sQuery(id+"F0.wireOp",EDGE,"E1.0.5.0");var subQ2=makeQuery(id+"F0.imprint","INTERSECT",VERTEX,{"disambiguationData":[OD(0.0)],"derivedFrom":[subQ1,subQ0]});Q138=makeQuery(id+"F0.imprint","IMPRINT",FACE,{"disambiguationData":[TD([[makeQuery(id+"F0.imprint","IMPRINT",EDGE,{"disambiguationData":[TD([[subQ2,-1.0]])],"derivedFrom":subQ1}),-1.0]])]});}
            var Q139;
            {var subQ0=sQuery(id+"F0.wireOp",EDGE,"E3.3.1.0");var subQ1=sQuery(id+"F0.wireOp",EDGE,"E1.0.5.0");var subQ2=makeQuery(id+"F0.imprint","INTERSECT",VERTEX,{"disambiguationData":[OD(0.0)],"derivedFrom":[subQ1,subQ0]});Q139=makeQuery(id+"F0.imprint","IMPRINT",FACE,{"disambiguationData":[TD([[makeQuery(id+"F0.imprint","IMPRINT",EDGE,{"disambiguationData":[TD([[subQ2,-1.0]])],"derivedFrom":subQ1}),-1.0]])]});}
            var Q140;
            {var subQ0=sQuery(id+"F0.wireOp",EDGE,"E3.12.1.0");var subQ1=sQuery(id+"F0.wireOp",EDGE,"E1.0.5.0");var subQ2=makeQuery(id+"F0.imprint","INTERSECT",VERTEX,{"disambiguationData":[OD(0.0)],"derivedFrom":[subQ1,subQ0]});Q140=makeQuery(id+"F0.imprint","IMPRINT",FACE,{"disambiguationData":[TD([[makeQuery(id+"F0.imprint","IMPRINT",EDGE,{"disambiguationData":[TD([[subQ2,-1.0]])],"derivedFrom":subQ1}),-1.0]])]});}
            var Q141;
            {var subQ0=sQuery(id+"F0.wireOp",EDGE,"E3.4.1.0");var subQ1=sQuery(id+"F0.wireOp",EDGE,"E1.0.5.0");var subQ2=makeQuery(id+"F0.imprint","INTERSECT",VERTEX,{"disambiguationData":[OD(0.0)],"derivedFrom":[subQ1,subQ0]});Q141=makeQuery(id+"F0.imprint","IMPRINT",FACE,{"disambiguationData":[TD([[makeQuery(id+"F0.imprint","IMPRINT",EDGE,{"disambiguationData":[TD([[subQ2,-1.0]])],"derivedFrom":subQ1}),-1.0]])]});}
            var Q142;
            {var subQ0=sQuery(id+"F0.wireOp",EDGE,"E3.19.1.0");var subQ1=sQuery(id+"F0.wireOp",EDGE,"E1.1.5.0");var subQ2=makeQuery(id+"F0.imprint","INTERSECT",VERTEX,{"disambiguationData":[OD(0.0)],"derivedFrom":[subQ1,subQ0]});Q142=makeQuery(id+"F0.imprint","IMPRINT",FACE,{"disambiguationData":[TD([[makeQuery(id+"F0.imprint","IMPRINT",EDGE,{"disambiguationData":[TD([[subQ2,-1.0]])],"derivedFrom":subQ1}),-1.0]])]});}
            var Q143;
            {var subQ0=sQuery(id+"F0.wireOp",EDGE,"E3.40.1.0");var subQ1=sQuery(id+"F0.wireOp",EDGE,"E1.2.5.0");var subQ2=makeQuery(id+"F0.imprint","INTERSECT",VERTEX,{"disambiguationData":[OD(0.0)],"derivedFrom":[subQ1,subQ0]});Q143=makeQuery(id+"F0.imprint","IMPRINT",FACE,{"disambiguationData":[TD([[makeQuery(id+"F0.imprint","IMPRINT",EDGE,{"disambiguationData":[TD([[subQ2,-1.0]])],"derivedFrom":subQ1}),-1.0]])]});}
            var Q144;
            {var subQ0=sQuery(id+"F0.wireOp",EDGE,"E3.21.1.0");var subQ1=sQuery(id+"F0.wireOp",EDGE,"E1.1.5.0");var subQ2=makeQuery(id+"F0.imprint","INTERSECT",VERTEX,{"disambiguationData":[OD(0.0)],"derivedFrom":[subQ1,subQ0]});Q144=makeQuery(id+"F0.imprint","IMPRINT",FACE,{"disambiguationData":[TD([[makeQuery(id+"F0.imprint","IMPRINT",EDGE,{"disambiguationData":[TD([[subQ2,-1.0]])],"derivedFrom":subQ1}),-1.0]])]});}
            var Q145;
            {var subQ0=sQuery(id+"F0.wireOp",EDGE,"E3.28.1.0");var subQ1=sQuery(id+"F0.wireOp",EDGE,"E1.1.5.0");var subQ2=makeQuery(id+"F0.imprint","INTERSECT",VERTEX,{"disambiguationData":[OD(0.0)],"derivedFrom":[subQ1,subQ0]});Q145=makeQuery(id+"F0.imprint","IMPRINT",FACE,{"disambiguationData":[TD([[makeQuery(id+"F0.imprint","IMPRINT",EDGE,{"disambiguationData":[TD([[subQ2,-1.0]])],"derivedFrom":subQ1}),-1.0]])]});}
            var Q146;
            {var subQ0=sQuery(id+"F0.wireOp",EDGE,"E3.38.1.0");var subQ1=sQuery(id+"F0.wireOp",EDGE,"E1.2.5.0");var subQ2=makeQuery(id+"F0.imprint","INTERSECT",VERTEX,{"disambiguationData":[OD(0.0)],"derivedFrom":[subQ1,subQ0]});Q146=makeQuery(id+"F0.imprint","IMPRINT",FACE,{"disambiguationData":[TD([[makeQuery(id+"F0.imprint","IMPRINT",EDGE,{"disambiguationData":[TD([[subQ2,-1.0]])],"derivedFrom":subQ1}),-1.0]])]});}
            var Q147;
            {var subQ0=sQuery(id+"F0.wireOp",EDGE,"E3.25.1.0");var subQ1=sQuery(id+"F0.wireOp",EDGE,"E1.1.5.0");var subQ2=makeQuery(id+"F0.imprint","INTERSECT",VERTEX,{"disambiguationData":[OD(0.0)],"derivedFrom":[subQ1,subQ0]});Q147=makeQuery(id+"F0.imprint","IMPRINT",FACE,{"disambiguationData":[TD([[makeQuery(id+"F0.imprint","IMPRINT",EDGE,{"disambiguationData":[TD([[subQ2,-1.0]])],"derivedFrom":subQ1}),-1.0]])]});}
            var Q148;
            {var subQ0=sQuery(id+"F0.wireOp",EDGE,"E3.17.1.0");var subQ1=sQuery(id+"F0.wireOp",EDGE,"E1.1.5.0");var subQ2=makeQuery(id+"F0.imprint","INTERSECT",VERTEX,{"disambiguationData":[OD(0.0)],"derivedFrom":[subQ1,subQ0]});Q148=makeQuery(id+"F0.imprint","IMPRINT",FACE,{"disambiguationData":[TD([[makeQuery(id+"F0.imprint","IMPRINT",EDGE,{"disambiguationData":[TD([[subQ2,-1.0]])],"derivedFrom":subQ1}),-1.0]])]});}
            var Q149;
            {var subQ0=sQuery(id+"F0.wireOp",EDGE,"E3.22.1.0");var subQ1=sQuery(id+"F0.wireOp",EDGE,"E1.1.5.0");var subQ2=makeQuery(id+"F0.imprint","INTERSECT",VERTEX,{"disambiguationData":[OD(0.0)],"derivedFrom":[subQ1,subQ0]});Q149=makeQuery(id+"F0.imprint","IMPRINT",FACE,{"disambiguationData":[TD([[makeQuery(id+"F0.imprint","IMPRINT",EDGE,{"disambiguationData":[TD([[subQ2,-1.0]])],"derivedFrom":subQ1}),-1.0]])]});}
            var Q150;
            {var subQ0=sQuery(id+"F0.wireOp",EDGE,"E3.37.1.0");var subQ1=sQuery(id+"F0.wireOp",EDGE,"E1.2.5.0");var subQ2=makeQuery(id+"F0.imprint","INTERSECT",VERTEX,{"disambiguationData":[OD(0.0)],"derivedFrom":[subQ1,subQ0]});Q150=makeQuery(id+"F0.imprint","IMPRINT",FACE,{"disambiguationData":[TD([[makeQuery(id+"F0.imprint","IMPRINT",EDGE,{"disambiguationData":[TD([[subQ2,-1.0]])],"derivedFrom":subQ1}),-1.0]])]});}
            var Q151;
            {var subQ0=sQuery(id+"F0.wireOp",EDGE,"E3.1.1.0");var subQ1=sQuery(id+"F0.wireOp",EDGE,"E1.0.5.0");var subQ2=makeQuery(id+"F0.imprint","INTERSECT",VERTEX,{"disambiguationData":[OD(0.0)],"derivedFrom":[subQ1,subQ0]});Q151=makeQuery(id+"F0.imprint","IMPRINT",FACE,{"disambiguationData":[TD([[makeQuery(id+"F0.imprint","IMPRINT",EDGE,{"disambiguationData":[TD([[subQ2,-1.0]])],"derivedFrom":subQ1}),-1.0]])]});}
            var Q152;
            {var subQ0=sQuery(id+"F0.wireOp",EDGE,"E3.9.1.0");var subQ1=sQuery(id+"F0.wireOp",EDGE,"E1.0.5.0");var subQ2=makeQuery(id+"F0.imprint","INTERSECT",VERTEX,{"disambiguationData":[OD(0.0)],"derivedFrom":[subQ1,subQ0]});Q152=makeQuery(id+"F0.imprint","IMPRINT",FACE,{"disambiguationData":[TD([[makeQuery(id+"F0.imprint","IMPRINT",EDGE,{"disambiguationData":[TD([[subQ2,-1.0]])],"derivedFrom":subQ1}),-1.0]])]});}
            var Q153;
            {var subQ0=sQuery(id+"F0.wireOp",EDGE,"E3.18.1.0");var subQ1=sQuery(id+"F0.wireOp",EDGE,"E1.1.5.0");var subQ2=makeQuery(id+"F0.imprint","INTERSECT",VERTEX,{"disambiguationData":[OD(0.0)],"derivedFrom":[subQ1,subQ0]});Q153=makeQuery(id+"F0.imprint","IMPRINT",FACE,{"disambiguationData":[TD([[makeQuery(id+"F0.imprint","IMPRINT",EDGE,{"disambiguationData":[TD([[subQ2,-1.0]])],"derivedFrom":subQ1}),-1.0]])]});}
            var Q154;
            {var subQ0=sQuery(id+"F0.wireOp",EDGE,"E3.26.1.0");var subQ1=sQuery(id+"F0.wireOp",EDGE,"E1.1.5.0");var subQ2=makeQuery(id+"F0.imprint","INTERSECT",VERTEX,{"disambiguationData":[OD(0.0)],"derivedFrom":[subQ1,subQ0]});Q154=makeQuery(id+"F0.imprint","IMPRINT",FACE,{"disambiguationData":[TD([[makeQuery(id+"F0.imprint","IMPRINT",EDGE,{"disambiguationData":[TD([[subQ2,-1.0]])],"derivedFrom":subQ1}),-1.0]])]});}
            var Q155;
            {var subQ0=sQuery(id+"F0.wireOp",EDGE,"E3.36.1.0");var subQ1=sQuery(id+"F0.wireOp",EDGE,"E1.2.5.0");var subQ2=makeQuery(id+"F0.imprint","INTERSECT",VERTEX,{"disambiguationData":[OD(0.0)],"derivedFrom":[subQ1,subQ0]});Q155=makeQuery(id+"F0.imprint","IMPRINT",FACE,{"disambiguationData":[TD([[makeQuery(id+"F0.imprint","IMPRINT",EDGE,{"disambiguationData":[TD([[subQ2,-1.0]])],"derivedFrom":subQ1}),-1.0]])]});}
            var Q156;
            {var subQ0=sQuery(id+"F0.wireOp",EDGE,"E3.8.1.0");var subQ1=sQuery(id+"F0.wireOp",EDGE,"E1.0.5.0");var subQ2=makeQuery(id+"F0.imprint","INTERSECT",VERTEX,{"disambiguationData":[OD(0.0)],"derivedFrom":[subQ1,subQ0]});Q156=makeQuery(id+"F0.imprint","IMPRINT",FACE,{"disambiguationData":[TD([[makeQuery(id+"F0.imprint","IMPRINT",EDGE,{"disambiguationData":[TD([[subQ2,-1.0]])],"derivedFrom":subQ1}),-1.0]])]});}
            var Q157;
            {var subQ0=sQuery(id+"F0.wireOp",EDGE,"E3.34.1.0");var subQ1=sQuery(id+"F0.wireOp",EDGE,"E1.2.5.0");var subQ2=makeQuery(id+"F0.imprint","INTERSECT",VERTEX,{"disambiguationData":[OD(0.0)],"derivedFrom":[subQ1,subQ0]});Q157=makeQuery(id+"F0.imprint","IMPRINT",FACE,{"disambiguationData":[TD([[makeQuery(id+"F0.imprint","IMPRINT",EDGE,{"disambiguationData":[TD([[subQ2,-1.0]])],"derivedFrom":subQ1}),-1.0]])]});}
            var Q158;
            {var subQ0=sQuery(id+"F0.wireOp",EDGE,"E3.42.1.0");var subQ1=sQuery(id+"F0.wireOp",EDGE,"E1.2.5.0");var subQ2=makeQuery(id+"F0.imprint","INTERSECT",VERTEX,{"disambiguationData":[OD(0.0)],"derivedFrom":[subQ1,subQ0]});Q158=makeQuery(id+"F0.imprint","IMPRINT",FACE,{"disambiguationData":[TD([[makeQuery(id+"F0.imprint","IMPRINT",EDGE,{"disambiguationData":[TD([[subQ2,-1.0]])],"derivedFrom":subQ1}),-1.0]])]});}
            var Q159;
            {var subQ0=sQuery(id+"F0.wireOp",EDGE,"E3.6.1.0");var subQ1=sQuery(id+"F0.wireOp",EDGE,"E1.0.5.0");var subQ2=makeQuery(id+"F0.imprint","INTERSECT",VERTEX,{"disambiguationData":[OD(0.0)],"derivedFrom":[subQ1,subQ0]});Q159=makeQuery(id+"F0.imprint","IMPRINT",FACE,{"disambiguationData":[TD([[makeQuery(id+"F0.imprint","IMPRINT",EDGE,{"disambiguationData":[TD([[subQ2,-1.0]])],"derivedFrom":subQ1}),-1.0]])]});}
            var Q160;
            {var subQ0=sQuery(id+"F0.wireOp",EDGE,"E3.35.1.0");var subQ1=sQuery(id+"F0.wireOp",EDGE,"E1.2.5.0");var subQ2=makeQuery(id+"F0.imprint","INTERSECT",VERTEX,{"disambiguationData":[OD(0.0)],"derivedFrom":[subQ1,subQ0]});Q160=makeQuery(id+"F0.imprint","IMPRINT",FACE,{"disambiguationData":[TD([[makeQuery(id+"F0.imprint","IMPRINT",EDGE,{"disambiguationData":[TD([[subQ2,-1.0]])],"derivedFrom":subQ1}),-1.0]])]});}
            var Q161;
            {var subQ0=sQuery(id+"F0.wireOp",EDGE,"E3.7.1.0");var subQ1=sQuery(id+"F0.wireOp",EDGE,"E1.0.5.0");var subQ2=makeQuery(id+"F0.imprint","INTERSECT",VERTEX,{"disambiguationData":[OD(0.0)],"derivedFrom":[subQ1,subQ0]});Q161=makeQuery(id+"F0.imprint","IMPRINT",FACE,{"disambiguationData":[TD([[makeQuery(id+"F0.imprint","IMPRINT",EDGE,{"disambiguationData":[TD([[subQ2,-1.0]])],"derivedFrom":subQ1}),-1.0]])]});}
            var Q162;
            {var subQ0=sQuery(id+"F0.wireOp",EDGE,"E3.15.1.0");var subQ1=sQuery(id+"F0.wireOp",EDGE,"E1.1.5.0");var subQ2=makeQuery(id+"F0.imprint","INTERSECT",VERTEX,{"disambiguationData":[OD(0.0)],"derivedFrom":[subQ1,subQ0]});Q162=makeQuery(id+"F0.imprint","IMPRINT",FACE,{"disambiguationData":[TD([[makeQuery(id+"F0.imprint","IMPRINT",EDGE,{"disambiguationData":[TD([[subQ2,-1.0]])],"derivedFrom":subQ1}),-1.0]])]});}
            var Q163;
            {var subQ0=sQuery(id+"F0.wireOp",EDGE,"E3.23.1.0");var subQ1=sQuery(id+"F0.wireOp",EDGE,"E1.1.5.0");var subQ2=makeQuery(id+"F0.imprint","INTERSECT",VERTEX,{"disambiguationData":[OD(0.0)],"derivedFrom":[subQ1,subQ0]});Q163=makeQuery(id+"F0.imprint","IMPRINT",FACE,{"disambiguationData":[TD([[makeQuery(id+"F0.imprint","IMPRINT",EDGE,{"disambiguationData":[TD([[subQ2,-1.0]])],"derivedFrom":subQ1}),-1.0]])]});}
            var Q164;
            {var subQ0=sQuery(id+"F0.wireOp",EDGE,"E3.16.1.0");var subQ1=sQuery(id+"F0.wireOp",EDGE,"E1.1.5.0");var subQ2=makeQuery(id+"F0.imprint","INTERSECT",VERTEX,{"disambiguationData":[OD(0.0)],"derivedFrom":[subQ1,subQ0]});Q164=makeQuery(id+"F0.imprint","IMPRINT",FACE,{"disambiguationData":[TD([[makeQuery(id+"F0.imprint","IMPRINT",EDGE,{"disambiguationData":[TD([[subQ2,-1.0]])],"derivedFrom":subQ1}),-1.0]])]});}
            var Q165;
            {var subQ0=sQuery(id+"F0.wireOp",EDGE,"E3.24.1.0");var subQ1=sQuery(id+"F0.wireOp",EDGE,"E1.1.5.0");var subQ2=makeQuery(id+"F0.imprint","INTERSECT",VERTEX,{"disambiguationData":[OD(0.0)],"derivedFrom":[subQ1,subQ0]});Q165=makeQuery(id+"F0.imprint","IMPRINT",FACE,{"disambiguationData":[TD([[makeQuery(id+"F0.imprint","IMPRINT",EDGE,{"disambiguationData":[TD([[subQ2,-1.0]])],"derivedFrom":subQ1}),-1.0]])]});}
            var Q166;
            {var subQ0=sQuery(id+"F0.wireOp",EDGE,"E3.33.1.0");var subQ1=sQuery(id+"F0.wireOp",EDGE,"E1.2.5.0");var subQ2=makeQuery(id+"F0.imprint","INTERSECT",VERTEX,{"disambiguationData":[OD(0.0)],"derivedFrom":[subQ1,subQ0]});Q166=makeQuery(id+"F0.imprint","IMPRINT",FACE,{"disambiguationData":[TD([[makeQuery(id+"F0.imprint","IMPRINT",EDGE,{"disambiguationData":[TD([[subQ2,-1.0]])],"derivedFrom":subQ1}),-1.0]])]});}
            var Q167;
            {var subQ0=sQuery(id+"F0.wireOp",EDGE,"E3.41.1.0");var subQ1=sQuery(id+"F0.wireOp",EDGE,"E1.2.5.0");var subQ2=makeQuery(id+"F0.imprint","INTERSECT",VERTEX,{"disambiguationData":[OD(0.0)],"derivedFrom":[subQ1,subQ0]});Q167=makeQuery(id+"F0.imprint","IMPRINT",FACE,{"disambiguationData":[TD([[makeQuery(id+"F0.imprint","IMPRINT",EDGE,{"disambiguationData":[TD([[subQ2,-1.0]])],"derivedFrom":subQ1}),-1.0]])]});}
            var Q168;
            {var subQ0=sQuery(id+"F0.wireOp",EDGE,"E3.5.1.0");var subQ1=sQuery(id+"F0.wireOp",EDGE,"E1.0.5.0");var subQ2=makeQuery(id+"F0.imprint","INTERSECT",VERTEX,{"disambiguationData":[OD(0.0)],"derivedFrom":[subQ1,subQ0]});Q168=makeQuery(id+"F0.imprint","IMPRINT",FACE,{"disambiguationData":[TD([[makeQuery(id+"F0.imprint","IMPRINT",EDGE,{"disambiguationData":[TD([[subQ2,-1.0]])],"derivedFrom":subQ1}),-1.0]])]});}
            var Q169;
            {var subQ0=sQuery(id+"F0.wireOp",EDGE,"E3.13.1.0");var subQ1=sQuery(id+"F0.wireOp",EDGE,"E1.0.5.0");var subQ2=makeQuery(id+"F0.imprint","INTERSECT",VERTEX,{"disambiguationData":[OD(0.0)],"derivedFrom":[subQ1,subQ0]});Q169=makeQuery(id+"F0.imprint","IMPRINT",FACE,{"disambiguationData":[TD([[makeQuery(id+"F0.imprint","IMPRINT",EDGE,{"disambiguationData":[TD([[subQ2,-1.0]])],"derivedFrom":subQ1}),-1.0]])]});}
            var Q170;
            {var subQ0=sQuery(id+"F0.wireOp",EDGE,"E3.0.1.0");var subQ1=sQuery(id+"F0.wireOp",EDGE,"E1.0.5.0");var subQ2=makeQuery(id+"F0.imprint","INTERSECT",VERTEX,{"disambiguationData":[OD(0.0)],"derivedFrom":[subQ1,subQ0]});Q170=makeQuery(id+"F0.imprint","IMPRINT",FACE,{"disambiguationData":[TD([[makeQuery(id+"F0.imprint","IMPRINT",EDGE,{"disambiguationData":[TD([[subQ2,-1.0]])],"derivedFrom":subQ1}),1.0]])]});}
            var Q171;
            {var subQ0=sQuery(id+"F0.wireOp",EDGE,"E3.0.1.0");var subQ1=sQuery(id+"F0.wireOp",EDGE,"E1.0.5.0");var subQ2=makeQuery(id+"F0.imprint","INTERSECT",VERTEX,{"disambiguationData":[OD(0.0)],"derivedFrom":[subQ1,subQ0]});Q171=makeQuery(id+"F0.imprint","IMPRINT",FACE,{"disambiguationData":[TD([[makeQuery(id+"F0.imprint","IMPRINT",EDGE,{"disambiguationData":[TD([[subQ2,-1.0]])],"derivedFrom":subQ1}),-1.0]])]});}
            var Q172;
            {var subQ0=sQuery(id+"F0.wireOp",EDGE,"E3.43.1.0");var subQ1=sQuery(id+"F0.wireOp",EDGE,"E1.2.5.0");var subQ2=makeQuery(id+"F0.imprint","INTERSECT",VERTEX,{"disambiguationData":[OD(0.0)],"derivedFrom":[subQ1,subQ0]});Q172=makeQuery(id+"F0.imprint","IMPRINT",FACE,{"disambiguationData":[TD([[makeQuery(id+"F0.imprint","IMPRINT",EDGE,{"disambiguationData":[TD([[subQ2,-1.0]])],"derivedFrom":subQ1}),1.0]])]});}
            var Q173;
            {var subQ0=sQuery(id+"F0.wireOp",EDGE,"E3.43.1.0");var subQ1=sQuery(id+"F0.wireOp",EDGE,"E1.2.5.0");var subQ2=makeQuery(id+"F0.imprint","INTERSECT",VERTEX,{"disambiguationData":[OD(0.0)],"derivedFrom":[subQ1,subQ0]});Q173=makeQuery(id+"F0.imprint","IMPRINT",FACE,{"disambiguationData":[TD([[makeQuery(id+"F0.imprint","IMPRINT",EDGE,{"disambiguationData":[TD([[subQ2,-1.0]])],"derivedFrom":subQ1}),-1.0]])]});}
            var Q174;
            {var subQ0=sQuery(id+"F0.wireOp",EDGE,"E3.14.1.0");var subQ1=sQuery(id+"F0.wireOp",EDGE,"E1.0.5.0");var subQ2=makeQuery(id+"F0.imprint","INTERSECT",VERTEX,{"disambiguationData":[OD(0.0)],"derivedFrom":[subQ1,subQ0]});Q174=makeQuery(id+"F0.imprint","IMPRINT",FACE,{"disambiguationData":[TD([[makeQuery(id+"F0.imprint","IMPRINT",EDGE,{"disambiguationData":[TD([[subQ2,-1.0]])],"derivedFrom":subQ1}),1.0]])]});}
            var Q175;
            {var subQ0=sQuery(id+"F0.wireOp",EDGE,"E3.14.1.0");var subQ1=sQuery(id+"F0.wireOp",EDGE,"E1.0.5.0");var subQ2=makeQuery(id+"F0.imprint","INTERSECT",VERTEX,{"disambiguationData":[OD(0.0)],"derivedFrom":[subQ1,subQ0]});Q175=makeQuery(id+"F0.imprint","IMPRINT",FACE,{"disambiguationData":[TD([[makeQuery(id+"F0.imprint","IMPRINT",EDGE,{"disambiguationData":[TD([[subQ2,-1.0]])],"derivedFrom":subQ1}),-1.0]])]});}
            var Q176;
            {var subQ1=sQuery(id+"F0.wireOp",EDGE,"E1.2.5.0");var subQ3=sQuery(id+"F0.wireOp",EDGE,"E3.29.1.0");var subQ4=makeQuery(id+"F0.imprint","INTERSECT",VERTEX,{"derivedFrom":[subQ1,subQ3]});Q176=makeQuery(id+"F0.imprint","IMPRINT",FACE,{"disambiguationData":[TD([[makeQuery(id+"F0.imprint","IMPRINT",EDGE,{"disambiguationData":[TD([[subQ4,-1.0]])],"derivedFrom":subQ3}),1.0]])]});}
            var Q177;
            {var subQ1=sQuery(id+"F0.wireOp",EDGE,"E1.2.4.1");var subQ3=sQuery(id+"F0.wireOp",EDGE,"E3.29.1.0");var subQ4=makeQuery(id+"F0.imprint","INTERSECT",VERTEX,{"derivedFrom":[subQ1,subQ3]});Q177=makeQuery(id+"F0.imprint","IMPRINT",FACE,{"disambiguationData":[TD([[makeQuery(id+"F0.imprint","IMPRINT",EDGE,{"disambiguationData":[TD([[subQ4,-1.0]])],"derivedFrom":subQ3}),1.0]])]});}
            var Q178;
            {var subQ1=sQuery(id+"F0.wireOp",EDGE,"E1.1.5.0");var subQ3=sQuery(id+"F0.wireOp",EDGE,"E3.29.1.0");var subQ4=makeQuery(id+"F0.imprint","INTERSECT",VERTEX,{"derivedFrom":[subQ1,subQ3]});Q178=makeQuery(id+"F0.imprint","IMPRINT",FACE,{"disambiguationData":[TD([[makeQuery(id+"F0.imprint","IMPRINT",EDGE,{"disambiguationData":[TD([[subQ4,1.0]])],"derivedFrom":subQ3}),1.0]])]});}
            var Q179;
            {var subQ1=sQuery(id+"F0.wireOp",EDGE,"E1.1.5.0");var subQ3=sQuery(id+"F0.wireOp",EDGE,"E3.29.1.0");var subQ4=makeQuery(id+"F0.imprint","INTERSECT",VERTEX,{"derivedFrom":[subQ1,subQ3]});Q179=makeQuery(id+"F0.imprint","IMPRINT",FACE,{"disambiguationData":[TD([[makeQuery(id+"F0.imprint","IMPRINT",EDGE,{"disambiguationData":[TD([[subQ4,-1.0]])],"derivedFrom":subQ3}),1.0]])]});}
            extrude(context, id + "F2", {"entities" : qUnion([Q0, Q1, Q2, Q3, Q4, Q5, Q6, Q7, Q8, Q9, Q10, Q11, Q12, Q13, Q14, Q15, Q16, Q17, Q18, Q19, Q20, Q21, Q22, Q23, Q24, Q25, Q26, Q27, Q28, Q29, Q30, Q31, Q32, Q33, Q34, Q35, Q36, Q37, Q38, Q39, Q40, Q41, Q42, Q43, Q44, Q45, Q46, Q47, Q48, Q49, Q50, Q51, Q52, Q53, Q54, Q55, Q56, Q57, Q58, Q59, Q60, Q61, Q62, Q63, Q64, Q65, Q66, Q67, Q68, Q69, Q70, Q71, Q72, Q73, Q74, Q75, Q76, Q77, Q78, Q79, Q80, Q81, Q82, Q83, Q84, Q85, Q86, Q87, Q88, Q89, Q90, Q91, Q92, Q93, Q94, Q95, Q96, Q97, Q98, Q99, Q100, Q101, Q102, Q103, Q104, Q105, Q106, Q107, Q108, Q109, Q110, Q111, Q112, Q113, Q114, Q115, Q116, Q117, Q118, Q119, Q120, Q121, Q122, Q123, Q124, Q125, Q126, Q127, Q128, Q129, Q130, Q131, Q132, Q133, Q134, Q135, Q136, Q137, Q138, Q139, Q140, Q141, Q142, Q143, Q144, Q145, Q146, Q147, Q148, Q149, Q150, Q151, Q152, Q153, Q154, Q155, Q156, Q157, Q158, Q159, Q160, Q161, Q162, Q163, Q164, Q165, Q166, Q167, Q168, Q169, Q170, Q171, Q172, Q173, Q174, Q175, Q176, Q177, Q178, Q179]), "operationType" : NewBodyOperationType.ADD, "depth" : 3048 * mm, "offsetDistance" : 25.4 * mm});
        }
        {
            var Q0;
            Q0=makeQuery(id+"F1.opExtrude","SWEPT_FACE",FACE,{"disambiguationData":[OSD([sQuery(id+"F0.wireOp",EDGE,"E0.top"),sQuery(id+"F0.wireOp",EDGE,"E1.1.0.0"),sQuery(id+"F0.wireOp",EDGE,"E1.2.0.0")])]});
            var sketch = newSketch(context, id + "F3", { "sketchPlane" : qUnion([Q0])});
            skLineSegment(sketch, "E4.bottom", {"start": v(1062.27, 0) * mm, "end": v(1976.67, 0) * mm});
            skLineSegment(sketch, "E4.top", {"start": v(1062.27, 1828.8) * mm, "end": v(1976.67, 1828.8) * mm});
            skLineSegment(sketch, "E4.left", {"start": v(1062.27, 0) * mm, "end": v(1062.27, 1828.8) * mm});
            skLineSegment(sketch, "E4.right", {"start": v(1976.67, 0) * mm, "end": v(1976.67, 1828.8) * mm});
            skSolve(sketch);
        }
        {
            var Q0;
            Q0 = qSketchRegion(id + "F3", true);
            extrude(context, id + "F4", {"entities" : qUnion([Q0]), "oppositeDirection" : true, "depth" : 7639.05 * mm, "offsetDistance" : 25.4 * mm});
        }
        {
            var Q0;
            Q0=makeQuery(id+"F4.opExtrude","CAP_FACE",FACE,{"disambiguationData":[OSD([sQuery(id+"F3.wireOp",EDGE,"E4.bottom"),sQuery(id+"F3.wireOp",EDGE,"E4.top"),sQuery(id+"F3.wireOp",EDGE,"E4.left"),sQuery(id+"F3.wireOp",EDGE,"E4.right")])],"isStart":true});
            var Q1;
            Q1=makeQuery(id+"F4.opExtrude","SWEPT_FACE",FACE,{"disambiguationData":[OSD([sQuery(id+"F3.wireOp",EDGE,"E4.bottom")])]});
            var Q2;
            Q2=makeQuery(id+"F4.opExtrude","CAP_FACE",FACE,{"disambiguationData":[OSD([sQuery(id+"F3.wireOp",EDGE,"E4.bottom"),sQuery(id+"F3.wireOp",EDGE,"E4.top"),sQuery(id+"F3.wireOp",EDGE,"E4.left"),sQuery(id+"F3.wireOp",EDGE,"E4.right")])],"isStart":false});
            shell(context, id + "F5", {"entities" : qUnion([Q0, Q1, Q2]), "thickness" : 25.4 * mm});
        }
        {
            var Q0;
            Q0=makeQuery(id+"F4.opExtrude","SWEPT_FACE",FACE,{"disambiguationData":[OSD([sQuery(id+"F3.wireOp",EDGE,"E4.left")])]});
            var sketch = newSketch(context, id + "F6", { "sketchPlane" : qUnion([Q0])});
            skLineSegment(sketch, "E5.bottom", {"start": v(-2274.45, 1828.8) * mm, "end": v(-2236.35, 1828.8) * mm});
            skLineSegment(sketch, "E5.top", {"start": v(-2274.45, 0) * mm, "end": v(-2236.35, 0) * mm});
            skLineSegment(sketch, "E5.left", {"start": v(-2274.45, 1828.8) * mm, "end": v(-2274.45, 0) * mm});
            skLineSegment(sketch, "E5.right", {"start": v(-2236.35, 1828.8) * mm, "end": v(-2236.35, 0) * mm});
            skLineSegment(sketch, "E6.bottom", {"start": v(-6846.68, 1828.8) * mm, "end": v(-6808.58, 1828.8) * mm});
            skLineSegment(sketch, "E6.top", {"start": v(-6846.68, 0) * mm, "end": v(-6808.58, 0) * mm});
            skLineSegment(sketch, "E6.left", {"start": v(-6846.68, 1828.8) * mm, "end": v(-6846.68, 0) * mm});
            skLineSegment(sketch, "E6.right", {"start": v(-6808.58, 1828.8) * mm, "end": v(-6808.58, 0) * mm});
            skSolve(sketch);
        }
        {
            var Q0;
            {var subQ0=sQuery(id+"F6.wireOp",EDGE,"E5.right");Q0=makeQuery(id+"F6.imprint","IMPRINT",FACE,{"disambiguationData":[TD([[makeQuery(id+"F6.imprint","IMPRINT",EDGE,{"derivedFrom":subQ0}),1.0]])]});}
            var Q1;
            {var subQ0=sQuery(id+"F6.wireOp",EDGE,"E5.left");Q1=makeQuery(id+"F6.imprint","IMPRINT",FACE,{"disambiguationData":[TD([[makeQuery(id+"F6.imprint","IMPRINT",EDGE,{"derivedFrom":subQ0}),-1.0]])]});}
            extrude(context, id + "F7", {"entities" : qUnion([Q0, Q1]), "operationType" : NewBodyOperationType.REMOVE, "oppositeDirection" : true, "depth" : 914.4 * mm, "offsetDistance" : 25.4 * mm});
        }
        {
            var Q0;
            Q0=makeQuery(id+"F1.opExtrude","SWEPT_FACE",FACE,{"disambiguationData":[OSD([sQuery(id+"F0.wireOp",EDGE,"E0.left"),sQuery(id+"F0.wireOp",EDGE,"E1.0.1.1"),sQuery(id+"F0.wireOp",EDGE,"E1.0.2.1"),sQuery(id+"F0.wireOp",EDGE,"E1.0.3.1"),sQuery(id+"F0.wireOp",EDGE,"E1.0.4.1"),sQuery(id+"F0.wireOp",EDGE,"E1.0.5.1"),sQuery(id+"F0.wireOp",EDGE,"E1.0.6.1")])]});
            var sketch = newSketch(context, id + "F8", { "sketchPlane" : qUnion([Q0])});
            skLineSegment(sketch, "E7.bottom", {"start": v(-4998.83, 0) * mm, "end": v(-4084.43, 0) * mm});
            skLineSegment(sketch, "E7.top", {"start": v(-4998.83, -25.4) * mm, "end": v(-4084.43, -25.4) * mm});
            skLineSegment(sketch, "E7.left", {"start": v(-4998.83, 0) * mm, "end": v(-4998.83, -25.4) * mm});
            skLineSegment(sketch, "E7.right", {"start": v(-4084.43, 0) * mm, "end": v(-4084.43, -25.4) * mm});
            skSolve(sketch);
        }
        {
            var Q0;
            Q0 = qSketchRegion(id + "F8", true);
            extrude(context, id + "F9", {"entities" : qUnion([Q0]), "operationType" : NewBodyOperationType.ADD, "depth" : 25.4 * mm, "offsetDistance" : 25.4 * mm});
        }
    });
